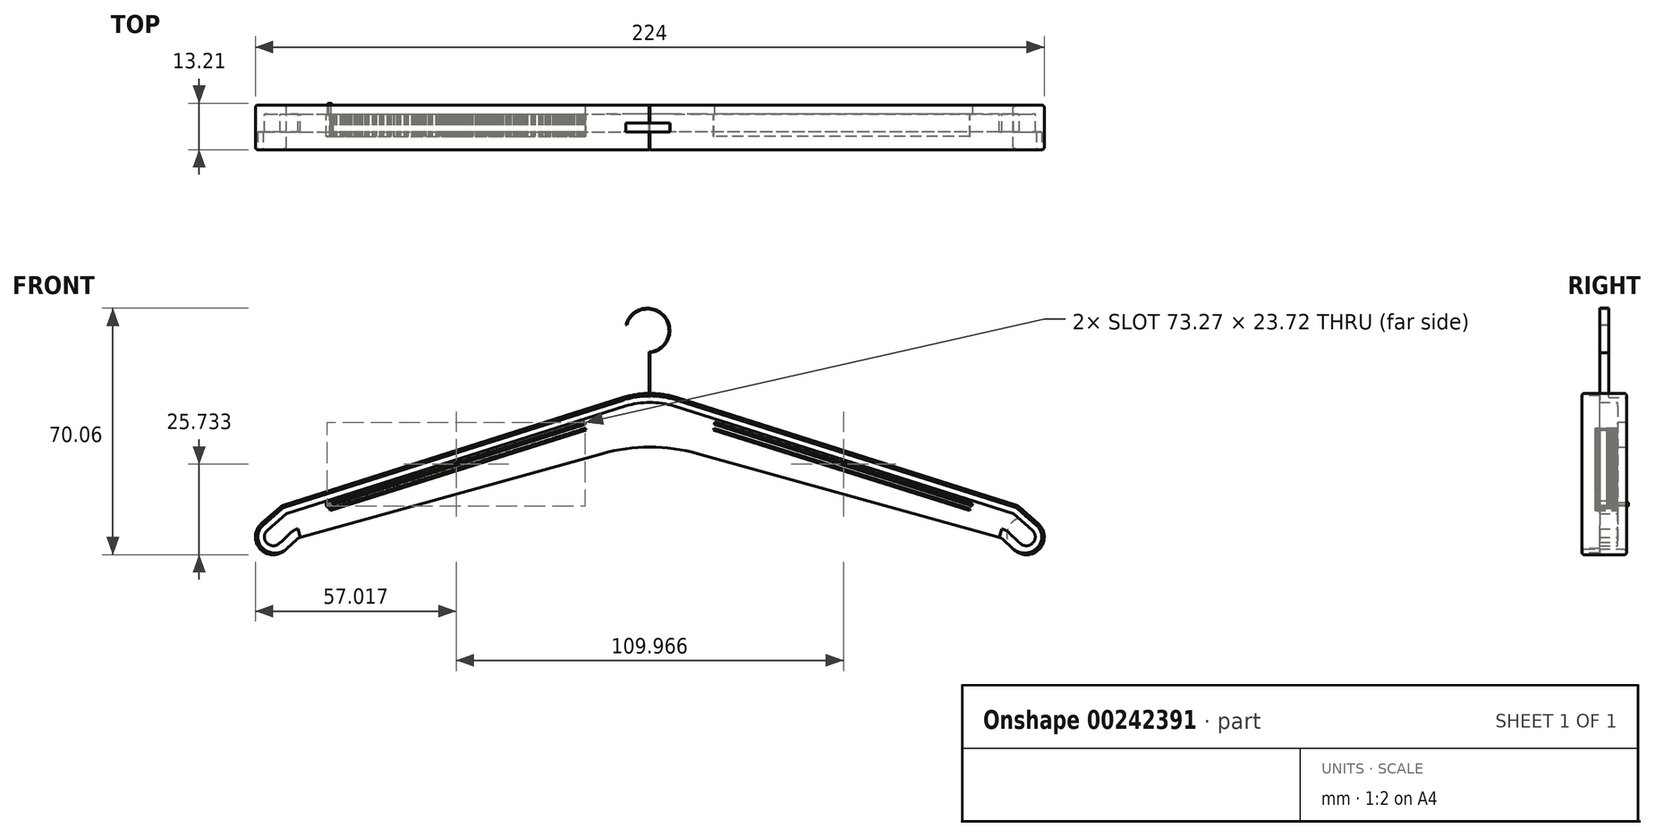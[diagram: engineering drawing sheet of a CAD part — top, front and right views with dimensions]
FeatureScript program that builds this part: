
annotation { "Feature Type Name" : "Feature", "Feature Type Description" : "" }
export const myFeature = defineFeature(function(context is Context, id is Id, definition is map)
    precondition{}
    {
        {
            var Q0;
            Q0=qCreatedBy(makeId("Front.planeOp"),FACE);
            var sketch = newSketch(context, id + "F0", { "sketchPlane" : qUnion([Q0])});
            skLineSegment(sketch, "E0", {"start": v(-104.02, 0.16) * mm, "end": v(-7.68, 30.71) * mm});
            skLineSegment(sketch, "E1", {"start": v(-99.25, -8.96) * mm, "end": v(-13.59, 14.81) * mm});
            skLineSegment(sketch, "E2.MirrorCS", {"start": v(104.52, 0) * mm, "end": v(7.68, 30.71) * mm});
            skLineSegment(sketch, "E3.MirrorCS", {"start": v(99.25, -8.96) * mm, "end": v(13.59, 14.81) * mm});
            skPoint(sketch, "E4.visualSharp", {"position": v(0, 18.58) * mm});
            skArc(sketch, "E5.filletArc", {"start": v(0.38, 28.89) * mm, "mid": v(0, 28.89) * mm, "end": v(-0.38, 28.89) * mm});
            skArc(sketch, "E6.filletArc", {"start": v(7.68, 30.71) * mm, "mid": v(0, 31.9) * mm, "end": v(-7.68, 30.71) * mm});
            skArc(sketch, "E7.filletArc", {"start": v(13.59, 14.81) * mm, "mid": v(0, 16.66) * mm, "end": v(-13.59, 14.81) * mm});
            skPoint(sketch, "E8.endSnap0", {"position": v(0, 31.9) * mm});
            skLineSegment(sketch, "E9", {"start": v(-104.92, -0.35) * mm, "end": v(-110.26, -5) * mm});
            skLineSegment(sketch, "E10", {"start": v(-102.91, -12.04) * mm, "end": v(-100.32, -9.57) * mm});
            skPoint(sketch, "E11.visualSharp", {"position": v(-111.4, -6) * mm});
            skArc(sketch, "E11.filletArc", {"start": v(-110.26, -5) * mm, "mid": v(-103.65, -12.72) * mm, "end": v(-110.13, -4.9) * mm});
            skPoint(sketch, "E12.visualSharp", {"position": v(-104.52, 0) * mm});
            skArc(sketch, "E12.filletArc", {"start": v(-104.02, 0.16) * mm, "mid": v(-104.5, -0.05) * mm, "end": v(-104.92, -0.35) * mm});
            skPoint(sketch, "E13.visualSharp", {"position": v(-107.27, -16.2) * mm});
            skArc(sketch, "E13.filletArc", {"start": v(-107.95, -13.2) * mm, "mid": v(-105.27, -13.31) * mm, "end": v(-102.91, -12.04) * mm});
            skPoint(sketch, "E14.visualSharp", {"position": v(-99.86, -9.13) * mm});
            skArc(sketch, "E14.filletArc", {"start": v(-99.25, -8.96) * mm, "mid": v(-99.82, -9.2) * mm, "end": v(-100.32, -9.57) * mm});
            skLineSegment(sketch, "E15", {"start": v(0, 16.66) * mm, "end": v(0, 31.9) * mm});
            skArc(sketch, "E16.MirrorCS", {"start": v(110.26, -5) * mm, "mid": v(103.65, -12.72) * mm, "end": v(110.13, -4.9) * mm});
            skLineSegment(sketch, "E17.MirrorCS", {"start": v(104.92, -0.35) * mm, "end": v(110.26, -5) * mm});
            skArc(sketch, "E18.MirrorCS", {"start": v(107.95, -13.2) * mm, "mid": v(105.27, -13.31) * mm, "end": v(102.91, -12.04) * mm});
            skLineSegment(sketch, "E19.MirrorCS", {"start": v(102.91, -12.04) * mm, "end": v(100.32, -9.57) * mm});
            skArc(sketch, "E20.MirrorCS", {"start": v(104.02, 0.16) * mm, "mid": v(104.5, -0.05) * mm, "end": v(104.92, -0.35) * mm});
            skArc(sketch, "E21.MirrorCS", {"start": v(99.25, -8.96) * mm, "mid": v(99.82, -9.2) * mm, "end": v(100.32, -9.57) * mm});
            skSolve(sketch);
        }
        {
            var Q0;
            {var subQ0=sQuery(id+"F0.wireOp",EDGE,"E0");Q0=makeQuery(id+"F0.imprint","IMPRINT",FACE,{"disambiguationData":[TD([[makeQuery(id+"F0.imprint","IMPRINT",EDGE,{"derivedFrom":subQ0}),-1.0]])]});}
            var Q1;
            {var subQ1=sQuery(id+"F0.wireOp",EDGE,"E3.MirrorCS");Q1=makeQuery(id+"F0.imprint","IMPRINT",FACE,{"disambiguationData":[TD([[makeQuery(id+"F0.imprint","IMPRINT",EDGE,{"derivedFrom":subQ1}),-1.0]])]});}
            var Q2;
            Q2=makeQuery(id+"F0.imprint","IMPRINT",FACE,{"disambiguationData":[TD([[makeQuery(id+"F0.imprint","IMPRINT",EDGE,{"derivedFrom":sQuery(id+"F0.wireOp",EDGE,"k7vzQUjf-RRhZ-hYac-MGxp-3dl7KEoSQEHl")}),1.0]])]});
            extrude(context, id + "F1", {"entities" : qUnion([Q0, Q1, Q2]), "depth" : 12.7 * mm});
        }
        {
            var Q0;
            Q0=makeQuery(id+"F1.opExtrude","CAP_EDGE",EDGE,{"disambiguationData":[OSD([sQuery(id+"F0.wireOp",EDGE,"E0")])],"isStart":true});
            var Q1;
            Q1=makeQuery(id+"F1.opExtrude","CAP_EDGE",EDGE,{"disambiguationData":[OSD([sQuery(id+"F0.wireOp",EDGE,"E0")])],"isStart":false});
            var Q2;
            Q2=makeQuery(id+"F1.opExtrude","CAP_EDGE",EDGE,{"disambiguationData":[OSD([sQuery(id+"F0.wireOp",EDGE,"E2.MirrorCS")])],"isStart":true});
            var Q3;
            Q3=makeQuery(id+"F1.opExtrude","CAP_EDGE",EDGE,{"disambiguationData":[OSD([sQuery(id+"F0.wireOp",EDGE,"E2.MirrorCS")])],"isStart":false});
            fillet(context, id + "F2", {"entities" : qUnion([Q0, Q1, Q2, Q3]), "radius" : 0.69 * mm, "tangentPropagation" : true, "allowEdgeOverflow" : false});
        }
        {
            var Q0;
            Q0=makeQuery(id+"F1.opExtrude","SWEPT_FACE",FACE,{"disambiguationData":[OSD([sQuery(id+"F0.wireOp",EDGE,"E7.filletArc")])]});
            var Q1;
            Q1=makeQuery(id+"F1.opExtrude","SWEPT_FACE",FACE,{"disambiguationData":[OSD([sQuery(id+"F0.wireOp",EDGE,"E1")])]});
            var Q2;
            Q2=makeQuery(id+"F1.opExtrude","SWEPT_FACE",FACE,{"disambiguationData":[OSD([sQuery(id+"F0.wireOp",EDGE,"E3.MirrorCS")])]});
            shell(context, id + "F3", {"entities" : qUnion([Q0, Q1, Q2]), "thickness" : 2.54 * mm});
        }
        {
            var Q0;
            Q0=qCreatedBy(makeId("Front.planeOp"),FACE);
            var sketch = newSketch(context, id + "F4", { "sketchPlane" : qUnion([Q0])});
            skLineSegment(sketch, "E22", {"start": v(0, 30.78) * mm, "end": v(0, 43.48) * mm});
            skArc(sketch, "E23", {"start": v(0, 43.48) * mm, "mid": v(4.18, 53.9) * mm, "end": v(-6.78, 51.45) * mm});
            skArc(sketch, "E24.0", {"start": v(-0.25, 43.71) * mm, "mid": v(4.06, 53.66) * mm, "end": v(-6.54, 51.39) * mm});
            skLineSegment(sketch, "E24.1", {"start": v(-0.25, 30.78) * mm, "end": v(-0.25, 43.71) * mm});
            skLineSegment(sketch, "E25", {"start": v(-6.78, 51.45) * mm, "end": v(-6.54, 51.39) * mm});
            skLineSegment(sketch, "E26", {"start": v(-0.25, 30.78) * mm, "end": v(0, 30.78) * mm});
            skSolve(sketch);
        }
        {
            var Q0;
            Q0 = qSketchRegion(id + "F4", true);
            extrude(context, id + "F5", {"entities" : qUnion([Q0]), "operationType" : NewBodyOperationType.ADD, "depth" : 12.7 * mm});
        }
        {
            var Q0;
            Q0 = qSketchRegion(id + "F4", true);
            extrude(context, id + "F6", {"entities" : qUnion([Q0]), "operationType" : NewBodyOperationType.REMOVE, "depth" : 5.08 * mm});
        }
        {
            var Q0;
            Q0=makeQuery(id+"F5.boolean.opBoolean","MERGE",FACE,{"derivedFrom":[makeQuery(id+"F1.opExtrude","CAP_FACE",FACE,{"disambiguationData":[OSD([sQuery(id+"F0.wireOp",EDGE,"E0"),sQuery(id+"F0.wireOp",EDGE,"E1"),sQuery(id+"F0.wireOp",EDGE,"E2.MirrorCS"),sQuery(id+"F0.wireOp",EDGE,"E3.MirrorCS"),sQuery(id+"F0.wireOp",EDGE,"E6.filletArc"),sQuery(id+"F0.wireOp",EDGE,"E7.filletArc"),sQuery(id+"F0.wireOp",EDGE,"E9"),sQuery(id+"F0.wireOp",EDGE,"E10"),sQuery(id+"F0.wireOp",EDGE,"E11.filletArc"),sQuery(id+"F0.wireOp",EDGE,"E12.filletArc"),sQuery(id+"F0.wireOp",EDGE,"E13.filletArc"),sQuery(id+"F0.wireOp",EDGE,"E14.filletArc"),sQuery(id+"F0.wireOp",EDGE,"E16.MirrorCS"),sQuery(id+"F0.wireOp",EDGE,"E17.MirrorCS"),sQuery(id+"F0.wireOp",EDGE,"E18.MirrorCS"),sQuery(id+"F0.wireOp",EDGE,"E19.MirrorCS"),sQuery(id+"F0.wireOp",EDGE,"E20.MirrorCS"),sQuery(id+"F0.wireOp",EDGE,"E21.MirrorCS")])],"isStart":false}),makeQuery(id+"F5.opExtrude","CAP_FACE",FACE,{"disambiguationData":[OSD([sQuery(id+"F4.wireOp",EDGE,"E22"),sQuery(id+"F4.wireOp",EDGE,"E23"),sQuery(id+"F4.wireOp",EDGE,"E24.0"),sQuery(id+"F4.wireOp",EDGE,"E24.1"),sQuery(id+"F4.wireOp",EDGE,"E25"),sQuery(id+"F4.wireOp",EDGE,"E26")])],"isStart":false})]});
            extrude(context, id + "F7", {"entities" : qUnion([Q0]), "operationType" : NewBodyOperationType.REMOVE, "oppositeDirection" : true, "depth" : 5.08 * mm});
        }
        {
            var Q0;
            {var subQ0=sQuery(id+"F0.wireOp",EDGE,"E21.MirrorCS");var subQ1=sQuery(id+"F0.wireOp",EDGE,"E20.MirrorCS");var subQ2=sQuery(id+"F0.wireOp",EDGE,"E19.MirrorCS");var subQ3=sQuery(id+"F0.wireOp",EDGE,"E18.MirrorCS");var subQ4=sQuery(id+"F0.wireOp",EDGE,"E17.MirrorCS");var subQ5=sQuery(id+"F0.wireOp",EDGE,"E16.MirrorCS");var subQ6=sQuery(id+"F0.wireOp",EDGE,"E14.filletArc");var subQ7=sQuery(id+"F0.wireOp",EDGE,"E13.filletArc");var subQ8=sQuery(id+"F0.wireOp",EDGE,"E12.filletArc");var subQ9=sQuery(id+"F0.wireOp",EDGE,"E11.filletArc");var subQ10=sQuery(id+"F0.wireOp",EDGE,"E10");var subQ11=sQuery(id+"F0.wireOp",EDGE,"E9");var subQ12=sQuery(id+"F0.wireOp",EDGE,"E7.filletArc");var subQ13=sQuery(id+"F0.wireOp",EDGE,"E6.filletArc");var subQ14=sQuery(id+"F0.wireOp",EDGE,"E3.MirrorCS");var subQ15=sQuery(id+"F0.wireOp",EDGE,"E2.MirrorCS");var subQ16=sQuery(id+"F0.wireOp",EDGE,"E1");var subQ17=sQuery(id+"F0.wireOp",EDGE,"E0");Q0=makeQuery(id+"F3.opShell","OFFSET_FACE",FACE,{"disambiguationData":[OSD([subQ17,subQ16,subQ15,subQ14,subQ13,subQ12,subQ11,subQ10,subQ9,subQ8,subQ7,subQ6,subQ5,subQ4,subQ3,subQ2,subQ1,subQ0]),TDD([makeQuery(id+"F1.opExtrude","CAP_FACE",FACE,{"disambiguationData":[OSD([subQ17,subQ16,subQ15,subQ14,subQ13,subQ12,subQ11,subQ10,subQ9,subQ8,subQ7,subQ6,subQ5,subQ4,subQ3,subQ2,subQ1,subQ0])],"isStart":true})])]});}
            var sketch = newSketch(context, id + "F8", { "sketchPlane" : qUnion([Q0])});
            skLineSegment(sketch, "E27", {"start": v(-90.8, -1.3) * mm, "end": v(-18.08, 21.46) * mm});
            skLineSegment(sketch, "E28.MirrorCS", {"start": v(90.8, -1.3) * mm, "end": v(18.08, 21.46) * mm});
            skLineSegment(sketch, "E29.0", {"start": v(90.95, -0.82) * mm, "end": v(18.23, 21.95) * mm});
            skLineSegment(sketch, "E30.0", {"start": v(-90.95, -0.82) * mm, "end": v(-18.23, 21.95) * mm});
            skLineSegment(sketch, "E31", {"start": v(-90.8, -1.3) * mm, "end": v(-90.95, -0.82) * mm});
            skLineSegment(sketch, "E32", {"start": v(-18.08, 21.46) * mm, "end": v(-18.23, 21.95) * mm});
            skLineSegment(sketch, "E33", {"start": v(18.08, 21.46) * mm, "end": v(18.23, 21.95) * mm});
            skLineSegment(sketch, "E34", {"start": v(90.8, -1.3) * mm, "end": v(90.95, -0.82) * mm});
            skSolve(sketch);
        }
        {
            var Q0;
            Q0 = qSketchRegion(id + "F8", true);
            var Q1;
            Q1=sQuery(id+"F8.wireOp",EDGE,"E27");
            var Q2;
            Q2=sQuery(id+"F8.wireOp",EDGE,"E28.MirrorCS");
            extrude(context, id + "F9", {"entities" : qUnion([Q0]), "surfaceEntities" : qUnion([Q1, Q2]), "depth" : 6.35 * mm});
        }
        {
            var Q0;
            Q0=makeQuery(id+"F9.opExtrude","CAP_FACE",FACE,{"disambiguationData":[OSD([sQuery(id+"F8.wireOp",EDGE,"E27"),sQuery(id+"F8.wireOp",EDGE,"E30.0"),sQuery(id+"F8.wireOp",EDGE,"E31"),sQuery(id+"F8.wireOp",EDGE,"E32")])],"isStart":false});
            var sketch = newSketch(context, id + "F10", { "sketchPlane" : qUnion([Q0])});
            skLineSegment(sketch, "E35", {"start": v(-90.95, -0.82) * mm, "end": v(-90.92, -0.67) * mm});
            skLineSegment(sketch, "E36", {"start": v(-90.92, -0.67) * mm, "end": v(-90.77, -0.63) * mm});
            skLineSegment(sketch, "E37", {"start": v(-90.77, -0.63) * mm, "end": v(-90.66, -0.73) * mm});
            skLineSegment(sketch, "E38", {"start": v(-90.66, -0.73) * mm, "end": v(-90.52, -0.69) * mm});
            skLineSegment(sketch, "E39.MirrorCS", {"start": v(-90.49, -0.54) * mm, "end": v(-90.52, -0.69) * mm});
            skLineSegment(sketch, "E40.MirrorCS", {"start": v(-90.34, -0.5) * mm, "end": v(-90.49, -0.54) * mm});
            skLineSegment(sketch, "E41.MirrorCS", {"start": v(-90.23, -0.6) * mm, "end": v(-90.34, -0.5) * mm});
            skLineSegment(sketch, "E42.MirrorCS", {"start": v(-90.34, -0.5) * mm, "end": v(-90.23, -0.6) * mm});
            skLineSegment(sketch, "E43.MirrorCS", {"start": v(-90.09, -0.55) * mm, "end": v(-90.23, -0.6) * mm});
            skLineSegment(sketch, "E44.MirrorCS", {"start": v(-90.06, -0.4) * mm, "end": v(-90.09, -0.55) * mm});
            skLineSegment(sketch, "E45.MirrorCS", {"start": v(-89.91, -0.36) * mm, "end": v(-90.06, -0.4) * mm});
            skLineSegment(sketch, "E46.MirrorCS", {"start": v(-89.8, -0.46) * mm, "end": v(-89.91, -0.36) * mm});
            skLineSegment(sketch, "E47.MirrorCS", {"start": v(-89.63, -0.27) * mm, "end": v(-89.65, -0.42) * mm});
            skLineSegment(sketch, "E48.MirrorCS", {"start": v(-89.65, -0.42) * mm, "end": v(-89.8, -0.46) * mm});
            skLineSegment(sketch, "E49.MirrorCS", {"start": v(-89.48, -0.22) * mm, "end": v(-89.63, -0.27) * mm});
            skLineSegment(sketch, "E50.MirrorCS", {"start": v(-89.37, -0.33) * mm, "end": v(-89.48, -0.22) * mm});
            skLineSegment(sketch, "E51.MirrorCS", {"start": v(-88.8, -0.15) * mm, "end": v(-88.76, 0) * mm});
            skLineSegment(sketch, "E52.MirrorCS", {"start": v(-88.76, 0) * mm, "end": v(-88.8, -0.15) * mm});
            skLineSegment(sketch, "E53.MirrorCS", {"start": v(-88.94, -0.2) * mm, "end": v(-88.8, -0.15) * mm});
            skLineSegment(sketch, "E54.MirrorCS", {"start": v(-88.76, 0) * mm, "end": v(-88.62, 0.05) * mm});
            skLineSegment(sketch, "E55.MirrorCS", {"start": v(-89.05, -0.09) * mm, "end": v(-88.94, -0.2) * mm});
            skLineSegment(sketch, "E56.MirrorCS", {"start": v(-88.36, -0.01) * mm, "end": v(-88.5, -0.06) * mm});
            skLineSegment(sketch, "E57.MirrorCS", {"start": v(-88.62, 0.05) * mm, "end": v(-88.5, -0.06) * mm});
            skLineSegment(sketch, "E58.MirrorCS", {"start": v(-88.33, 0.14) * mm, "end": v(-88.36, -0.01) * mm});
            skLineSegment(sketch, "E59.MirrorCS", {"start": v(-88.19, 0.18) * mm, "end": v(-88.33, 0.14) * mm});
            skLineSegment(sketch, "E60.MirrorCS", {"start": v(-88.08, 0.08) * mm, "end": v(-88.19, 0.18) * mm});
            skLineSegment(sketch, "E61.MirrorCS", {"start": v(-89.2, -0.13) * mm, "end": v(-89.05, -0.09) * mm});
            skLineSegment(sketch, "E62.MirrorCS", {"start": v(-89.22, -0.28) * mm, "end": v(-89.2, -0.13) * mm});
            skLineSegment(sketch, "E63.MirrorCS", {"start": v(-89.37, -0.33) * mm, "end": v(-89.22, -0.28) * mm});
            skLineSegment(sketch, "E64.MirrorCS", {"start": v(-88.19, 0.18) * mm, "end": v(-88.08, 0.08) * mm});
            skLineSegment(sketch, "E65.MirrorCS", {"start": v(-86.64, 0.53) * mm, "end": v(-86.61, 0.68) * mm});
            skLineSegment(sketch, "E66.MirrorCS", {"start": v(-86.61, 0.68) * mm, "end": v(-86.64, 0.53) * mm});
            skLineSegment(sketch, "E67.MirrorCS", {"start": v(-87.5, 0.26) * mm, "end": v(-87.65, 0.21) * mm});
            skLineSegment(sketch, "E68.MirrorCS", {"start": v(-87.47, 0.4) * mm, "end": v(-87.33, 0.45) * mm});
            skLineSegment(sketch, "E69.MirrorCS", {"start": v(-86.9, 0.59) * mm, "end": v(-86.79, 0.48) * mm});
            skLineSegment(sketch, "E70.MirrorCS", {"start": v(-87.04, 0.54) * mm, "end": v(-86.9, 0.59) * mm});
            skLineSegment(sketch, "E71.MirrorCS", {"start": v(-87.07, 0.4) * mm, "end": v(-87.04, 0.54) * mm});
            skLineSegment(sketch, "E72.MirrorCS", {"start": v(-85.93, 0.75) * mm, "end": v(-86.04, 0.86) * mm});
            skLineSegment(sketch, "E73.MirrorCS", {"start": v(-86.04, 0.86) * mm, "end": v(-86.18, 0.81) * mm});
            skLineSegment(sketch, "E74.MirrorCS", {"start": v(-86.18, 0.81) * mm, "end": v(-86.21, 0.66) * mm});
            skLineSegment(sketch, "E75.MirrorCS", {"start": v(-87.33, 0.45) * mm, "end": v(-87.22, 0.35) * mm});
            skLineSegment(sketch, "E76.MirrorCS", {"start": v(-86.21, 0.66) * mm, "end": v(-86.36, 0.62) * mm});
            skLineSegment(sketch, "E77.MirrorCS", {"start": v(-87.76, 0.32) * mm, "end": v(-87.9, 0.27) * mm});
            skLineSegment(sketch, "E78.MirrorCS", {"start": v(-87.22, 0.35) * mm, "end": v(-87.07, 0.4) * mm});
            skLineSegment(sketch, "E79.MirrorCS", {"start": v(-87.9, 0.27) * mm, "end": v(-87.93, 0.12) * mm});
            skLineSegment(sketch, "E80.MirrorCS", {"start": v(-86.47, 0.72) * mm, "end": v(-86.36, 0.62) * mm});
            skLineSegment(sketch, "E81.MirrorCS", {"start": v(-86.61, 0.68) * mm, "end": v(-86.47, 0.72) * mm});
            skLineSegment(sketch, "E82.MirrorCS", {"start": v(-87.93, 0.12) * mm, "end": v(-88.08, 0.08) * mm});
            skLineSegment(sketch, "E83.MirrorCS", {"start": v(-87.65, 0.21) * mm, "end": v(-87.76, 0.32) * mm});
            skLineSegment(sketch, "E84.MirrorCS", {"start": v(-87.5, 0.26) * mm, "end": v(-87.47, 0.4) * mm});
            skLineSegment(sketch, "E85.MirrorCS", {"start": v(-86.79, 0.48) * mm, "end": v(-86.64, 0.53) * mm});
            skLineSegment(sketch, "E86.MirrorCS", {"start": v(-84.46, 1.35) * mm, "end": v(-84.49, 1.2) * mm});
            skLineSegment(sketch, "E87.MirrorCS", {"start": v(-83.88, 1.53) * mm, "end": v(-83.77, 1.42) * mm});
            skLineSegment(sketch, "E88.MirrorCS", {"start": v(-82.34, 1.87) * mm, "end": v(-82.3, 2.02) * mm});
            skLineSegment(sketch, "E89.MirrorCS", {"start": v(-85.6, 1) * mm, "end": v(-85.75, 0.94) * mm});
            skLineSegment(sketch, "E90.MirrorCS", {"start": v(-84.49, 1.2) * mm, "end": v(-84.46, 1.35) * mm});
            skLineSegment(sketch, "E91.MirrorCS", {"start": v(-86.04, 0.86) * mm, "end": v(-85.93, 0.75) * mm});
            skLineSegment(sketch, "E92.MirrorCS", {"start": v(-82.74, 1.89) * mm, "end": v(-82.6, 1.93) * mm});
            skLineSegment(sketch, "E93.MirrorCS", {"start": v(-84.46, 1.35) * mm, "end": v(-84.31, 1.4) * mm});
            skLineSegment(sketch, "E94.MirrorCS", {"start": v(-81.9, 2) * mm, "end": v(-82.05, 1.96) * mm});
            skLineSegment(sketch, "E95.MirrorCS", {"start": v(-82.3, 2.02) * mm, "end": v(-82.34, 1.87) * mm});
            skLineSegment(sketch, "E96.MirrorCS", {"start": v(-82.91, 1.7) * mm, "end": v(-82.77, 1.74) * mm});
            skLineSegment(sketch, "E97.MirrorCS", {"start": v(-84.2, 1.29) * mm, "end": v(-84.06, 1.33) * mm});
            skLineSegment(sketch, "E98.MirrorCS", {"start": v(-83.77, 1.42) * mm, "end": v(-83.88, 1.53) * mm});
            skLineSegment(sketch, "E99.MirrorCS", {"start": v(-83.88, 1.53) * mm, "end": v(-84.03, 1.48) * mm});
            skLineSegment(sketch, "E100.MirrorCS", {"start": v(-85.18, 1.13) * mm, "end": v(-85.32, 1.08) * mm});
            skLineSegment(sketch, "E101.MirrorCS", {"start": v(-84.64, 1.15) * mm, "end": v(-84.49, 1.2) * mm});
            skLineSegment(sketch, "E102.MirrorCS", {"start": v(-83.17, 1.75) * mm, "end": v(-83.02, 1.8) * mm});
            skLineSegment(sketch, "E103.MirrorCS", {"start": v(-85.35, 0.93) * mm, "end": v(-85.5, 0.88) * mm});
            skLineSegment(sketch, "E104.MirrorCS", {"start": v(-85.78, 0.8) * mm, "end": v(-85.93, 0.75) * mm});
            skLineSegment(sketch, "E105.MirrorCS", {"start": v(-84.31, 1.4) * mm, "end": v(-84.2, 1.29) * mm});
            skLineSegment(sketch, "E106.MirrorCS", {"start": v(-82.48, 1.83) * mm, "end": v(-82.34, 1.87) * mm});
            skLineSegment(sketch, "E107.MirrorCS", {"start": v(-83.63, 1.47) * mm, "end": v(-83.77, 1.42) * mm});
            skLineSegment(sketch, "E108.MirrorCS", {"start": v(-82.3, 2.02) * mm, "end": v(-82.16, 2.07) * mm});
            skLineSegment(sketch, "E109.MirrorCS", {"start": v(-83.34, 1.56) * mm, "end": v(-83.45, 1.66) * mm});
            skLineSegment(sketch, "E110.MirrorCS", {"start": v(-83.02, 1.8) * mm, "end": v(-82.91, 1.7) * mm});
            skLineSegment(sketch, "E111.MirrorCS", {"start": v(-85.07, 1.02) * mm, "end": v(-84.92, 1.06) * mm});
            skLineSegment(sketch, "E112.MirrorCS", {"start": v(-83.45, 1.66) * mm, "end": v(-83.6, 1.62) * mm});
            skLineSegment(sketch, "E113.MirrorCS", {"start": v(-85.75, 0.94) * mm, "end": v(-85.78, 0.8) * mm});
            skLineSegment(sketch, "E114.MirrorCS", {"start": v(-84.9, 1.21) * mm, "end": v(-84.75, 1.26) * mm});
            skLineSegment(sketch, "E115.MirrorCS", {"start": v(-83.6, 1.62) * mm, "end": v(-83.63, 1.47) * mm});
            skLineSegment(sketch, "E116.MirrorCS", {"start": v(-84.75, 1.26) * mm, "end": v(-84.64, 1.15) * mm});
            skLineSegment(sketch, "E117.MirrorCS", {"start": v(-85.5, 0.88) * mm, "end": v(-85.6, 1) * mm});
            skLineSegment(sketch, "E118.MirrorCS", {"start": v(-83.2, 1.6) * mm, "end": v(-83.34, 1.56) * mm});
            skLineSegment(sketch, "E119.MirrorCS", {"start": v(-85.32, 1.08) * mm, "end": v(-85.35, 0.93) * mm});
            skLineSegment(sketch, "E120.MirrorCS", {"start": v(-83.2, 1.6) * mm, "end": v(-83.17, 1.75) * mm});
            skLineSegment(sketch, "E121.MirrorCS", {"start": v(-84.92, 1.06) * mm, "end": v(-84.9, 1.21) * mm});
            skLineSegment(sketch, "E122.MirrorCS", {"start": v(-82.77, 1.74) * mm, "end": v(-82.74, 1.89) * mm});
            skLineSegment(sketch, "E123.MirrorCS", {"start": v(-82.6, 1.93) * mm, "end": v(-82.48, 1.83) * mm});
            skLineSegment(sketch, "E124.MirrorCS", {"start": v(-84.03, 1.48) * mm, "end": v(-84.06, 1.33) * mm});
            skLineSegment(sketch, "E125.MirrorCS", {"start": v(-82.16, 2.07) * mm, "end": v(-82.05, 1.96) * mm});
            skLineSegment(sketch, "E126.MirrorCS", {"start": v(-85.07, 1.02) * mm, "end": v(-85.18, 1.13) * mm});
            skLineSegment(sketch, "E127.MirrorCS", {"start": v(-81.88, 2.16) * mm, "end": v(-81.9, 2) * mm});
            skLineSegment(sketch, "E128.MirrorCS", {"start": v(-81.73, 2.2) * mm, "end": v(-81.88, 2.16) * mm});
            skLineSegment(sketch, "E129", {"start": v(-90.84, -0.65) * mm, "end": v(-90.77, -0.89) * mm, "construction": true});
            skLineSegment(sketch, "E130", {"start": v(-81.8, 2.18) * mm, "end": v(-81.71, 1.88) * mm, "construction": true});
            skLineSegment(sketch, "E131.MirrorCS", {"start": v(-77.57, 3.5) * mm, "end": v(-77.6, 3.36) * mm});
            skLineSegment(sketch, "E132.MirrorCS", {"start": v(-75.45, 4.03) * mm, "end": v(-75.42, 4.18) * mm});
            skLineSegment(sketch, "E133.MirrorCS", {"start": v(-79.04, 2.9) * mm, "end": v(-79.15, 3.01) * mm});
            skLineSegment(sketch, "E134.MirrorCS", {"start": v(-77.6, 3.36) * mm, "end": v(-77.57, 3.5) * mm});
            skLineSegment(sketch, "E135.MirrorCS", {"start": v(-79.15, 3.01) * mm, "end": v(-79.04, 2.9) * mm});
            skLineSegment(sketch, "E136.MirrorCS", {"start": v(-77, 3.69) * mm, "end": v(-76.89, 3.58) * mm});
            skLineSegment(sketch, "E137.MirrorCS", {"start": v(-73.3, 4.7) * mm, "end": v(-73.27, 4.85) * mm});
            skLineSegment(sketch, "E138.MirrorCS", {"start": v(-79.73, 2.83) * mm, "end": v(-79.76, 2.68) * mm});
            skLineSegment(sketch, "E139.MirrorCS", {"start": v(-74.85, 4.36) * mm, "end": v(-74.74, 4.25) * mm});
            skLineSegment(sketch, "E140.MirrorCS", {"start": v(-75.42, 4.18) * mm, "end": v(-75.45, 4.03) * mm});
            skLineSegment(sketch, "E141.MirrorCS", {"start": v(-81.3, 2.34) * mm, "end": v(-81.2, 2.23) * mm});
            skLineSegment(sketch, "E142.MirrorCS", {"start": v(-73.27, 4.85) * mm, "end": v(-73.3, 4.7) * mm});
            skLineSegment(sketch, "E143.MirrorCS", {"start": v(-79.76, 2.68) * mm, "end": v(-79.73, 2.83) * mm});
            skLineSegment(sketch, "E144.MirrorCS", {"start": v(-74.74, 4.25) * mm, "end": v(-74.85, 4.36) * mm});
            skLineSegment(sketch, "E145.MirrorCS", {"start": v(-76.89, 3.58) * mm, "end": v(-77, 3.69) * mm});
            skLineSegment(sketch, "E146.MirrorCS", {"start": v(-79.15, 3.01) * mm, "end": v(-79.3, 2.97) * mm});
            skLineSegment(sketch, "E147.MirrorCS", {"start": v(-81.2, 2.23) * mm, "end": v(-81.3, 2.34) * mm});
            skLineSegment(sketch, "E148.MirrorCS", {"start": v(-77.57, 3.5) * mm, "end": v(-77.43, 3.55) * mm});
            skLineSegment(sketch, "E149.MirrorCS", {"start": v(-75.42, 4.18) * mm, "end": v(-75.28, 4.22) * mm});
            skLineSegment(sketch, "E150.MirrorCS", {"start": v(-77.43, 3.55) * mm, "end": v(-77.32, 3.45) * mm});
            skLineSegment(sketch, "E151.MirrorCS", {"start": v(-75.28, 4.22) * mm, "end": v(-75.17, 4.12) * mm});
            skLineSegment(sketch, "E152.MirrorCS", {"start": v(-79.3, 2.97) * mm, "end": v(-79.32, 2.82) * mm});
            skLineSegment(sketch, "E153.MirrorCS", {"start": v(-81.62, 2.1) * mm, "end": v(-81.48, 2.14) * mm});
            skLineSegment(sketch, "E154.MirrorCS", {"start": v(-74.85, 4.36) * mm, "end": v(-75, 4.31) * mm});
            skLineSegment(sketch, "E155.MirrorCS", {"start": v(-78, 3.37) * mm, "end": v(-77.86, 3.42) * mm});
            skLineSegment(sketch, "E156.MirrorCS", {"start": v(-77.86, 3.42) * mm, "end": v(-77.75, 3.31) * mm});
            skLineSegment(sketch, "E157.MirrorCS", {"start": v(-81.45, 2.3) * mm, "end": v(-81.48, 2.14) * mm});
            skLineSegment(sketch, "E158.MirrorCS", {"start": v(-78.86, 3.1) * mm, "end": v(-78.9, 2.95) * mm});
            skLineSegment(sketch, "E159.MirrorCS", {"start": v(-75.6, 3.98) * mm, "end": v(-75.45, 4.03) * mm});
            skLineSegment(sketch, "E160.MirrorCS", {"start": v(-75.17, 4.12) * mm, "end": v(-75.02, 4.16) * mm});
            skLineSegment(sketch, "E161.MirrorCS", {"start": v(-79.58, 2.88) * mm, "end": v(-79.47, 2.77) * mm});
            skLineSegment(sketch, "E162.MirrorCS", {"start": v(-80.16, 2.7) * mm, "end": v(-80.01, 2.74) * mm});
            skLineSegment(sketch, "E163.MirrorCS", {"start": v(-77, 3.69) * mm, "end": v(-77.14, 3.64) * mm});
            skLineSegment(sketch, "E164.MirrorCS", {"start": v(-74.56, 4.45) * mm, "end": v(-74.6, 4.3) * mm});
            skLineSegment(sketch, "E165.MirrorCS", {"start": v(-78.46, 3.09) * mm, "end": v(-78.6, 3.04) * mm});
            skLineSegment(sketch, "E166.MirrorCS", {"start": v(-81.02, 2.43) * mm, "end": v(-81.05, 2.28) * mm});
            skLineSegment(sketch, "E167.MirrorCS", {"start": v(-74.16, 4.43) * mm, "end": v(-74.13, 4.58) * mm});
            skLineSegment(sketch, "E168.MirrorCS", {"start": v(-76.03, 3.85) * mm, "end": v(-75.88, 3.9) * mm});
            skLineSegment(sketch, "E169.MirrorCS", {"start": v(-77.75, 3.31) * mm, "end": v(-77.6, 3.36) * mm});
            skLineSegment(sketch, "E170.MirrorCS", {"start": v(-79.73, 2.83) * mm, "end": v(-79.58, 2.88) * mm});
            skLineSegment(sketch, "E171.MirrorCS", {"start": v(-80.59, 2.56) * mm, "end": v(-80.62, 2.41) * mm});
            skLineSegment(sketch, "E172.MirrorCS", {"start": v(-80.76, 2.37) * mm, "end": v(-80.87, 2.47) * mm});
            skLineSegment(sketch, "E173.MirrorCS", {"start": v(-74.13, 4.58) * mm, "end": v(-73.98, 4.63) * mm});
            skLineSegment(sketch, "E174.MirrorCS", {"start": v(-74.16, 4.43) * mm, "end": v(-74.3, 4.39) * mm});
            skLineSegment(sketch, "E175.MirrorCS", {"start": v(-80.19, 2.55) * mm, "end": v(-80.16, 2.7) * mm});
            skLineSegment(sketch, "E176.MirrorCS", {"start": v(-78.6, 3.04) * mm, "end": v(-78.72, 3.15) * mm});
            skLineSegment(sketch, "E177.MirrorCS", {"start": v(-74.42, 4.5) * mm, "end": v(-74.56, 4.45) * mm});
            skLineSegment(sketch, "E178.MirrorCS", {"start": v(-76.46, 3.71) * mm, "end": v(-76.57, 3.82) * mm});
            skLineSegment(sketch, "E179.MirrorCS", {"start": v(-73.12, 4.9) * mm, "end": v(-73.01, 4.8) * mm});
            skLineSegment(sketch, "E180.MirrorCS", {"start": v(-75, 4.31) * mm, "end": v(-75.02, 4.16) * mm});
            skLineSegment(sketch, "E181.MirrorCS", {"start": v(-78.43, 3.24) * mm, "end": v(-78.29, 3.28) * mm});
            skLineSegment(sketch, "E182.MirrorCS", {"start": v(-77.32, 3.45) * mm, "end": v(-77.17, 3.5) * mm});
            skLineSegment(sketch, "E183.MirrorCS", {"start": v(-81.05, 2.28) * mm, "end": v(-81.2, 2.23) * mm});
            skLineSegment(sketch, "E184.MirrorCS", {"start": v(-73.27, 4.85) * mm, "end": v(-73.12, 4.9) * mm});
            skLineSegment(sketch, "E185.MirrorCS", {"start": v(-75.88, 3.9) * mm, "end": v(-75.85, 4.04) * mm});
            skLineSegment(sketch, "E186.MirrorCS", {"start": v(-76.14, 3.96) * mm, "end": v(-76.28, 3.9) * mm});
            skLineSegment(sketch, "E187.MirrorCS", {"start": v(-78.03, 3.22) * mm, "end": v(-78, 3.37) * mm});
            skLineSegment(sketch, "E188.MirrorCS", {"start": v(-78.46, 3.09) * mm, "end": v(-78.43, 3.24) * mm});
            skLineSegment(sketch, "E189.MirrorCS", {"start": v(-80.33, 2.5) * mm, "end": v(-80.44, 2.6) * mm});
            skLineSegment(sketch, "E190.MirrorCS", {"start": v(-81.3, 2.34) * mm, "end": v(-81.45, 2.3) * mm});
            skLineSegment(sketch, "E191.MirrorCS", {"start": v(-79.32, 2.82) * mm, "end": v(-79.47, 2.77) * mm});
            skLineSegment(sketch, "E192.MirrorCS", {"start": v(-78.9, 2.95) * mm, "end": v(-79.04, 2.9) * mm});
            skLineSegment(sketch, "E193.MirrorCS", {"start": v(-76.71, 3.77) * mm, "end": v(-76.74, 3.63) * mm});
            skLineSegment(sketch, "E194.MirrorCS", {"start": v(-76.74, 3.63) * mm, "end": v(-76.89, 3.58) * mm});
            skLineSegment(sketch, "E195.MirrorCS", {"start": v(-78.29, 3.28) * mm, "end": v(-78.18, 3.18) * mm});
            skLineSegment(sketch, "E196.MirrorCS", {"start": v(-79.9, 2.64) * mm, "end": v(-79.76, 2.68) * mm});
            skLineSegment(sketch, "E197.MirrorCS", {"start": v(-80.62, 2.41) * mm, "end": v(-80.76, 2.37) * mm});
            skLineSegment(sketch, "E198.MirrorCS", {"start": v(-76.03, 3.85) * mm, "end": v(-76.14, 3.96) * mm});
            skLineSegment(sketch, "E199.MirrorCS", {"start": v(-73.44, 4.66) * mm, "end": v(-73.3, 4.7) * mm});
            skLineSegment(sketch, "E200.MirrorCS", {"start": v(-73.55, 4.76) * mm, "end": v(-73.44, 4.66) * mm});
            skLineSegment(sketch, "E201.MirrorCS", {"start": v(-73.7, 4.72) * mm, "end": v(-73.55, 4.76) * mm});
            skLineSegment(sketch, "E202.MirrorCS", {"start": v(-76.31, 3.76) * mm, "end": v(-76.46, 3.71) * mm});
            skLineSegment(sketch, "E203.MirrorCS", {"start": v(-76.57, 3.82) * mm, "end": v(-76.71, 3.77) * mm});
            skLineSegment(sketch, "E204.MirrorCS", {"start": v(-75.85, 4.04) * mm, "end": v(-75.7, 4.09) * mm});
            skLineSegment(sketch, "E205.MirrorCS", {"start": v(-74.6, 4.3) * mm, "end": v(-74.74, 4.25) * mm});
            skLineSegment(sketch, "E206.MirrorCS", {"start": v(-76.28, 3.9) * mm, "end": v(-76.31, 3.76) * mm});
            skLineSegment(sketch, "E207.MirrorCS", {"start": v(-78.72, 3.15) * mm, "end": v(-78.86, 3.1) * mm});
            skLineSegment(sketch, "E208.MirrorCS", {"start": v(-72.7, 5.03) * mm, "end": v(-72.84, 4.99) * mm});
            skLineSegment(sketch, "E209.MirrorCS", {"start": v(-72.84, 4.99) * mm, "end": v(-72.87, 4.84) * mm});
            skLineSegment(sketch, "E210.MirrorCS", {"start": v(-80.44, 2.6) * mm, "end": v(-80.59, 2.56) * mm});
            skLineSegment(sketch, "E211.MirrorCS", {"start": v(-73.73, 4.57) * mm, "end": v(-73.7, 4.72) * mm});
            skLineSegment(sketch, "E212.MirrorCS", {"start": v(-73.98, 4.63) * mm, "end": v(-73.87, 4.52) * mm});
            skLineSegment(sketch, "E213.MirrorCS", {"start": v(-72.87, 4.84) * mm, "end": v(-73.01, 4.8) * mm});
            skLineSegment(sketch, "E214.MirrorCS", {"start": v(-75.7, 4.09) * mm, "end": v(-75.6, 3.98) * mm});
            skLineSegment(sketch, "E215.MirrorCS", {"start": v(-77.14, 3.64) * mm, "end": v(-77.17, 3.5) * mm});
            skLineSegment(sketch, "E216.MirrorCS", {"start": v(-73.87, 4.52) * mm, "end": v(-73.73, 4.57) * mm});
            skLineSegment(sketch, "E217.MirrorCS", {"start": v(-80.33, 2.5) * mm, "end": v(-80.19, 2.55) * mm});
            skLineSegment(sketch, "E218.MirrorCS", {"start": v(-74.3, 4.39) * mm, "end": v(-74.42, 4.5) * mm});
            skLineSegment(sketch, "E219.MirrorCS", {"start": v(-80.01, 2.74) * mm, "end": v(-79.9, 2.64) * mm});
            skLineSegment(sketch, "E220.MirrorCS", {"start": v(-78.18, 3.18) * mm, "end": v(-78.03, 3.22) * mm});
            skLineSegment(sketch, "E221.MirrorCS", {"start": v(-80.87, 2.47) * mm, "end": v(-81.02, 2.43) * mm});
            skLineSegment(sketch, "E222.MirrorCS", {"start": v(-72.58, 4.93) * mm, "end": v(-72.7, 5.03) * mm});
            skLineSegment(sketch, "E223.MirrorCS", {"start": v(-72.77, 5.01) * mm, "end": v(-72.7, 4.77) * mm, "construction": true});
            skLineSegment(sketch, "E224.MirrorCS", {"start": v(-66.41, 6.86) * mm, "end": v(-66.38, 7) * mm});
            skLineSegment(sketch, "E225.MirrorCS", {"start": v(-59.53, 9.02) * mm, "end": v(-59.5, 9.17) * mm});
            skLineSegment(sketch, "E226.MirrorCS", {"start": v(-70, 5.74) * mm, "end": v(-70.11, 5.84) * mm});
            skLineSegment(sketch, "E227.MirrorCS", {"start": v(-67.96, 6.52) * mm, "end": v(-67.85, 6.41) * mm});
            skLineSegment(sketch, "E228.MirrorCS", {"start": v(-57.37, 9.69) * mm, "end": v(-57.34, 9.84) * mm});
            skLineSegment(sketch, "E229.MirrorCS", {"start": v(-61.07, 8.67) * mm, "end": v(-60.96, 8.57) * mm});
            skLineSegment(sketch, "E230.MirrorCS", {"start": v(-67.85, 6.41) * mm, "end": v(-67.96, 6.52) * mm});
            skLineSegment(sketch, "E231.MirrorCS", {"start": v(-70.11, 5.84) * mm, "end": v(-70, 5.74) * mm});
            skLineSegment(sketch, "E232.MirrorCS", {"start": v(-57.34, 9.84) * mm, "end": v(-57.37, 9.69) * mm});
            skLineSegment(sketch, "E233.MirrorCS", {"start": v(-59.5, 9.17) * mm, "end": v(-59.53, 9.02) * mm});
            skLineSegment(sketch, "E234.MirrorCS", {"start": v(-55.22, 10.36) * mm, "end": v(-55.2, 10.51) * mm});
            skLineSegment(sketch, "E235.MirrorCS", {"start": v(-66.38, 7) * mm, "end": v(-66.41, 6.86) * mm});
            skLineSegment(sketch, "E236.MirrorCS", {"start": v(-60.96, 8.57) * mm, "end": v(-61.07, 8.67) * mm});
            skLineSegment(sketch, "E237.MirrorCS", {"start": v(-57.34, 9.84) * mm, "end": v(-57.2, 9.88) * mm});
            skLineSegment(sketch, "E238.MirrorCS", {"start": v(-68.53, 6.34) * mm, "end": v(-68.56, 6.19) * mm});
            skLineSegment(sketch, "E239.MirrorCS", {"start": v(-72.26, 5.17) * mm, "end": v(-72.15, 5.06) * mm});
            skLineSegment(sketch, "E240.MirrorCS", {"start": v(-67.96, 6.52) * mm, "end": v(-68.1, 6.47) * mm});
            skLineSegment(sketch, "E241.MirrorCS", {"start": v(-66.38, 7) * mm, "end": v(-66.24, 7.05) * mm});
            skLineSegment(sketch, "E242.MirrorCS", {"start": v(-65.8, 7.19) * mm, "end": v(-65.7, 7.08) * mm});
            skLineSegment(sketch, "E243.MirrorCS", {"start": v(-64.23, 7.68) * mm, "end": v(-64.26, 7.53) * mm});
            skLineSegment(sketch, "E244.MirrorCS", {"start": v(-63.22, 8) * mm, "end": v(-63.11, 7.9) * mm});
            skLineSegment(sketch, "E245.MirrorCS", {"start": v(-70.69, 5.66) * mm, "end": v(-70.72, 5.51) * mm});
            skLineSegment(sketch, "E246.MirrorCS", {"start": v(-55.2, 10.51) * mm, "end": v(-55.22, 10.36) * mm});
            skLineSegment(sketch, "E247.MirrorCS", {"start": v(-70.11, 5.84) * mm, "end": v(-70.26, 5.8) * mm});
            skLineSegment(sketch, "E248.MirrorCS", {"start": v(-61.65, 8.5) * mm, "end": v(-61.68, 8.34) * mm});
            skLineSegment(sketch, "E249.MirrorCS", {"start": v(-59.5, 9.17) * mm, "end": v(-59.35, 9.21) * mm});
            skLineSegment(sketch, "E250.MirrorCS", {"start": v(-58.92, 9.35) * mm, "end": v(-58.81, 9.24) * mm});
            skLineSegment(sketch, "E251.MirrorCS", {"start": v(-56.66, 9.91) * mm, "end": v(-56.77, 10.02) * mm});
            skLineSegment(sketch, "E252.MirrorCS", {"start": v(-61.07, 8.67) * mm, "end": v(-61.22, 8.63) * mm});
            skLineSegment(sketch, "E253.MirrorCS", {"start": v(-61.68, 8.34) * mm, "end": v(-61.65, 8.5) * mm});
            skLineSegment(sketch, "E254.MirrorCS", {"start": v(-56.77, 10.02) * mm, "end": v(-56.66, 9.91) * mm});
            skLineSegment(sketch, "E255.MirrorCS", {"start": v(-72.15, 5.06) * mm, "end": v(-72.26, 5.17) * mm});
            skLineSegment(sketch, "E256.MirrorCS", {"start": v(-65.7, 7.08) * mm, "end": v(-65.8, 7.19) * mm});
            skLineSegment(sketch, "E257.MirrorCS", {"start": v(-58.81, 9.24) * mm, "end": v(-58.92, 9.35) * mm});
            skLineSegment(sketch, "E258.MirrorCS", {"start": v(-70.72, 5.51) * mm, "end": v(-70.69, 5.66) * mm});
            skLineSegment(sketch, "E259.MirrorCS", {"start": v(-57.52, 9.64) * mm, "end": v(-57.37, 9.69) * mm});
            skLineSegment(sketch, "E260.MirrorCS", {"start": v(-67.7, 6.46) * mm, "end": v(-67.85, 6.41) * mm});
            skLineSegment(sketch, "E261.MirrorCS", {"start": v(-59.67, 8.97) * mm, "end": v(-59.53, 9.02) * mm});
            skLineSegment(sketch, "E262.MirrorCS", {"start": v(-57.63, 9.75) * mm, "end": v(-57.52, 9.64) * mm});
            skLineSegment(sketch, "E263.MirrorCS", {"start": v(-66.56, 6.81) * mm, "end": v(-66.41, 6.86) * mm});
            skLineSegment(sketch, "E264.MirrorCS", {"start": v(-55.2, 10.51) * mm, "end": v(-55.05, 10.56) * mm});
            skLineSegment(sketch, "E265.MirrorCS", {"start": v(-60.82, 8.61) * mm, "end": v(-60.96, 8.57) * mm});
            skLineSegment(sketch, "E266.MirrorCS", {"start": v(-69.86, 5.78) * mm, "end": v(-70, 5.74) * mm});
            skLineSegment(sketch, "E267.MirrorCS", {"start": v(-65.8, 7.19) * mm, "end": v(-65.95, 7.14) * mm});
            skLineSegment(sketch, "E268.MirrorCS", {"start": v(-64.26, 7.53) * mm, "end": v(-64.23, 7.68) * mm});
            skLineSegment(sketch, "E269.MirrorCS", {"start": v(-62.97, 7.94) * mm, "end": v(-63.11, 7.9) * mm});
            skLineSegment(sketch, "E270.MirrorCS", {"start": v(-58.92, 9.35) * mm, "end": v(-59.07, 9.3) * mm});
            skLineSegment(sketch, "E271.MirrorCS", {"start": v(-61.22, 8.63) * mm, "end": v(-61.25, 8.48) * mm});
            skLineSegment(sketch, "E272.MirrorCS", {"start": v(-70.69, 5.66) * mm, "end": v(-70.54, 5.7) * mm});
            skLineSegment(sketch, "E273.MirrorCS", {"start": v(-72.26, 5.17) * mm, "end": v(-72.4, 5.12) * mm});
            skLineSegment(sketch, "E274.MirrorCS", {"start": v(-68.56, 6.19) * mm, "end": v(-68.53, 6.34) * mm});
            skLineSegment(sketch, "E275.MirrorCS", {"start": v(-56.77, 10.02) * mm, "end": v(-56.91, 9.97) * mm});
            skLineSegment(sketch, "E276.MirrorCS", {"start": v(-61.93, 8.4) * mm, "end": v(-61.82, 8.3) * mm});
            skLineSegment(sketch, "E277.MirrorCS", {"start": v(-64.4, 7.49) * mm, "end": v(-64.26, 7.53) * mm});
            skLineSegment(sketch, "E278.MirrorCS", {"start": v(-72, 5.1) * mm, "end": v(-72.15, 5.06) * mm});
            skLineSegment(sketch, "E279.MirrorCS", {"start": v(-56.51, 9.96) * mm, "end": v(-56.66, 9.91) * mm});
            skLineSegment(sketch, "E280.MirrorCS", {"start": v(-58.66, 9.29) * mm, "end": v(-58.81, 9.24) * mm});
            skLineSegment(sketch, "E281.MirrorCS", {"start": v(-55.37, 10.32) * mm, "end": v(-55.22, 10.36) * mm});
            skLineSegment(sketch, "E282.MirrorCS", {"start": v(-70.86, 5.47) * mm, "end": v(-70.72, 5.51) * mm});
            skLineSegment(sketch, "E283.MirrorCS", {"start": v(-66.24, 7.05) * mm, "end": v(-66.13, 6.95) * mm});
            skLineSegment(sketch, "E284.MirrorCS", {"start": v(-65.55, 7.13) * mm, "end": v(-65.7, 7.08) * mm});
            skLineSegment(sketch, "E285.MirrorCS", {"start": v(-63.11, 7.9) * mm, "end": v(-63.22, 8) * mm});
            skLineSegment(sketch, "E286.MirrorCS", {"start": v(-68.7, 6.14) * mm, "end": v(-68.56, 6.19) * mm});
            skLineSegment(sketch, "E287.MirrorCS", {"start": v(-70.26, 5.8) * mm, "end": v(-70.29, 5.65) * mm});
            skLineSegment(sketch, "E288.MirrorCS", {"start": v(-63.22, 8) * mm, "end": v(-63.37, 7.95) * mm});
            skLineSegment(sketch, "E289.MirrorCS", {"start": v(-68.1, 6.47) * mm, "end": v(-68.13, 6.32) * mm});
            skLineSegment(sketch, "E290.MirrorCS", {"start": v(-61.65, 8.5) * mm, "end": v(-61.5, 8.54) * mm});
            skLineSegment(sketch, "E291.MirrorCS", {"start": v(-68.53, 6.34) * mm, "end": v(-68.39, 6.38) * mm});
            skLineSegment(sketch, "E292.MirrorCS", {"start": v(-61.82, 8.3) * mm, "end": v(-61.68, 8.34) * mm});
            skLineSegment(sketch, "E293.MirrorCS", {"start": v(-57.2, 9.88) * mm, "end": v(-57.09, 9.78) * mm});
            skLineSegment(sketch, "E294.MirrorCS", {"start": v(-59.35, 9.21) * mm, "end": v(-59.24, 9.1) * mm});
            skLineSegment(sketch, "E295.MirrorCS", {"start": v(-64.23, 7.68) * mm, "end": v(-64.09, 7.73) * mm});
            skLineSegment(sketch, "E296.MirrorCS", {"start": v(-56.91, 9.97) * mm, "end": v(-56.94, 9.82) * mm});
            skLineSegment(sketch, "E297.MirrorCS", {"start": v(-61.25, 8.48) * mm, "end": v(-61.4, 8.43) * mm});
            skLineSegment(sketch, "E298.MirrorCS", {"start": v(-66.13, 6.95) * mm, "end": v(-65.98, 7) * mm});
            skLineSegment(sketch, "E299.MirrorCS", {"start": v(-72.4, 5.12) * mm, "end": v(-72.44, 4.97) * mm});
            skLineSegment(sketch, "E300.MirrorCS", {"start": v(-61.5, 8.54) * mm, "end": v(-61.4, 8.43) * mm});
            skLineSegment(sketch, "E301.MirrorCS", {"start": v(-54.62, 10.7) * mm, "end": v(-54.76, 10.65) * mm});
            skLineSegment(sketch, "E302.MirrorCS", {"start": v(-54.76, 10.65) * mm, "end": v(-54.8, 10.5) * mm});
            skLineSegment(sketch, "E303.MirrorCS", {"start": v(-65.95, 7.14) * mm, "end": v(-65.98, 7) * mm});
            skLineSegment(sketch, "E304.MirrorCS", {"start": v(-54.5, 10.59) * mm, "end": v(-54.62, 10.7) * mm});
            skLineSegment(sketch, "E305.MirrorCS", {"start": v(-72.58, 4.93) * mm, "end": v(-72.44, 4.97) * mm});
            skLineSegment(sketch, "E306.MirrorCS", {"start": v(-60.79, 8.76) * mm, "end": v(-60.82, 8.61) * mm});
            skLineSegment(sketch, "E307.MirrorCS", {"start": v(-57.09, 9.78) * mm, "end": v(-56.94, 9.82) * mm});
            skLineSegment(sketch, "E308.MirrorCS", {"start": v(-54.69, 10.67) * mm, "end": v(-54.61, 10.43) * mm, "construction": true});
            skLineSegment(sketch, "E309.MirrorCS", {"start": v(-59.07, 9.3) * mm, "end": v(-59.1, 9.15) * mm});
            skLineSegment(sketch, "E310.MirrorCS", {"start": v(-68.39, 6.38) * mm, "end": v(-68.28, 6.28) * mm});
            skLineSegment(sketch, "E311.MirrorCS", {"start": v(-62.36, 8.27) * mm, "end": v(-62.5, 8.22) * mm});
            skLineSegment(sketch, "E312.MirrorCS", {"start": v(-68.13, 6.32) * mm, "end": v(-68.28, 6.28) * mm});
            skLineSegment(sketch, "E313.MirrorCS", {"start": v(-65.52, 7.28) * mm, "end": v(-65.55, 7.13) * mm});
            skLineSegment(sketch, "E314.MirrorCS", {"start": v(-62.25, 8.16) * mm, "end": v(-62.36, 8.27) * mm});
            skLineSegment(sketch, "E315.MirrorCS", {"start": v(-70.54, 5.7) * mm, "end": v(-70.43, 5.6) * mm});
            skLineSegment(sketch, "E316.MirrorCS", {"start": v(-67.67, 6.6) * mm, "end": v(-67.7, 6.46) * mm});
            skLineSegment(sketch, "E317.MirrorCS", {"start": v(-62.5, 8.22) * mm, "end": v(-62.54, 8.07) * mm});
            skLineSegment(sketch, "E318.MirrorCS", {"start": v(-55.05, 10.56) * mm, "end": v(-54.94, 10.45) * mm});
            skLineSegment(sketch, "E319.MirrorCS", {"start": v(-59.78, 9.08) * mm, "end": v(-59.67, 8.97) * mm});
            skLineSegment(sketch, "E320.MirrorCS", {"start": v(-70.29, 5.65) * mm, "end": v(-70.43, 5.6) * mm});
            skLineSegment(sketch, "E321.MirrorCS", {"start": v(-54.8, 10.5) * mm, "end": v(-54.94, 10.45) * mm});
            skLineSegment(sketch, "E322.MirrorCS", {"start": v(-59.24, 9.1) * mm, "end": v(-59.1, 9.15) * mm});
            skLineSegment(sketch, "E323.MirrorCS", {"start": v(-71.15, 5.38) * mm, "end": v(-71.12, 5.53) * mm});
            skLineSegment(sketch, "E324.MirrorCS", {"start": v(-69.4, 6.07) * mm, "end": v(-69.25, 6.11) * mm});
            skLineSegment(sketch, "E325.MirrorCS", {"start": v(-69.14, 6) * mm, "end": v(-69, 6.05) * mm});
            skLineSegment(sketch, "E326.MirrorCS", {"start": v(-63.54, 7.76) * mm, "end": v(-63.4, 7.8) * mm});
            skLineSegment(sketch, "E327.MirrorCS", {"start": v(-65.12, 7.26) * mm, "end": v(-65.27, 7.22) * mm});
            skLineSegment(sketch, "E328.MirrorCS", {"start": v(-69.57, 5.87) * mm, "end": v(-69.68, 5.98) * mm});
            skLineSegment(sketch, "E329.MirrorCS", {"start": v(-71.83, 5.3) * mm, "end": v(-71.98, 5.26) * mm});
            skLineSegment(sketch, "E330.MirrorCS", {"start": v(-56.48, 10.1) * mm, "end": v(-56.51, 9.96) * mm});
            skLineSegment(sketch, "E331.MirrorCS", {"start": v(-71.58, 5.24) * mm, "end": v(-71.72, 5.2) * mm});
            skLineSegment(sketch, "E332.MirrorCS", {"start": v(-69.43, 5.92) * mm, "end": v(-69.57, 5.87) * mm});
            skLineSegment(sketch, "E333.MirrorCS", {"start": v(-71.98, 5.26) * mm, "end": v(-72, 5.1) * mm});
            skLineSegment(sketch, "E334.MirrorCS", {"start": v(-57.95, 9.5) * mm, "end": v(-57.8, 9.56) * mm});
            skLineSegment(sketch, "E335.MirrorCS", {"start": v(-71.3, 5.33) * mm, "end": v(-71.4, 5.44) * mm});
            skLineSegment(sketch, "E336.MirrorCS", {"start": v(-62.8, 8.13) * mm, "end": v(-62.94, 8.09) * mm});
            skLineSegment(sketch, "E337.MirrorCS", {"start": v(-60.1, 8.84) * mm, "end": v(-59.96, 8.88) * mm});
            skLineSegment(sketch, "E338.MirrorCS", {"start": v(-63.8, 7.82) * mm, "end": v(-63.65, 7.86) * mm});
            skLineSegment(sketch, "E339.MirrorCS", {"start": v(-60.64, 8.8) * mm, "end": v(-60.79, 8.76) * mm});
            skLineSegment(sketch, "E340.MirrorCS", {"start": v(-63.65, 7.86) * mm, "end": v(-63.54, 7.76) * mm});
            skLineSegment(sketch, "E341.MirrorCS", {"start": v(-58.23, 9.42) * mm, "end": v(-58.38, 9.37) * mm});
            skLineSegment(sketch, "E342.MirrorCS", {"start": v(-69.43, 5.92) * mm, "end": v(-69.4, 6.07) * mm});
            skLineSegment(sketch, "E343.MirrorCS", {"start": v(-69.83, 5.93) * mm, "end": v(-69.86, 5.78) * mm});
            skLineSegment(sketch, "E344.MirrorCS", {"start": v(-63.83, 7.67) * mm, "end": v(-63.98, 7.62) * mm});
            skLineSegment(sketch, "E345.MirrorCS", {"start": v(-64.52, 7.6) * mm, "end": v(-64.4, 7.49) * mm});
            skLineSegment(sketch, "E346.MirrorCS", {"start": v(-57.77, 9.7) * mm, "end": v(-57.63, 9.75) * mm});
            skLineSegment(sketch, "E347.MirrorCS", {"start": v(-57.8, 9.56) * mm, "end": v(-57.77, 9.7) * mm});
            skLineSegment(sketch, "E348.MirrorCS", {"start": v(-58.06, 9.62) * mm, "end": v(-58.2, 9.57) * mm});
            skLineSegment(sketch, "E349.MirrorCS", {"start": v(-59.96, 8.88) * mm, "end": v(-59.93, 9.03) * mm});
            skLineSegment(sketch, "E350.MirrorCS", {"start": v(-67.42, 6.54) * mm, "end": v(-67.53, 6.65) * mm});
            skLineSegment(sketch, "E351.MirrorCS", {"start": v(-64.95, 7.46) * mm, "end": v(-64.84, 7.35) * mm});
            skLineSegment(sketch, "E352.MirrorCS", {"start": v(-60.39, 8.75) * mm, "end": v(-60.36, 8.9) * mm});
            skLineSegment(sketch, "E353.MirrorCS", {"start": v(-66.67, 6.92) * mm, "end": v(-66.56, 6.81) * mm});
            skLineSegment(sketch, "E354.MirrorCS", {"start": v(-71.3, 5.33) * mm, "end": v(-71.15, 5.38) * mm});
            skLineSegment(sketch, "E355.MirrorCS", {"start": v(-67.1, 6.79) * mm, "end": v(-67.24, 6.74) * mm});
            skLineSegment(sketch, "E356.MirrorCS", {"start": v(-59.93, 9.03) * mm, "end": v(-59.78, 9.08) * mm});
            skLineSegment(sketch, "E357.MirrorCS", {"start": v(-62.54, 8.07) * mm, "end": v(-62.68, 8.03) * mm});
            skLineSegment(sketch, "E358.MirrorCS", {"start": v(-57.95, 9.5) * mm, "end": v(-58.06, 9.62) * mm});
            skLineSegment(sketch, "E359.MirrorCS", {"start": v(-66.99, 6.68) * mm, "end": v(-66.84, 6.73) * mm});
            skLineSegment(sketch, "E360.MirrorCS", {"start": v(-65.12, 7.26) * mm, "end": v(-65.1, 7.41) * mm});
            skLineSegment(sketch, "E361.MirrorCS", {"start": v(-71.4, 5.44) * mm, "end": v(-71.55, 5.4) * mm});
            skLineSegment(sketch, "E362.MirrorCS", {"start": v(-64.66, 7.55) * mm, "end": v(-64.52, 7.6) * mm});
            skLineSegment(sketch, "E363.MirrorCS", {"start": v(-63.37, 7.95) * mm, "end": v(-63.4, 7.8) * mm});
            skLineSegment(sketch, "E364.MirrorCS", {"start": v(-55.9, 10.29) * mm, "end": v(-55.8, 10.18) * mm});
            skLineSegment(sketch, "E365.MirrorCS", {"start": v(-56.08, 10.1) * mm, "end": v(-56.05, 10.24) * mm});
            skLineSegment(sketch, "E366.MirrorCS", {"start": v(-65.38, 7.32) * mm, "end": v(-65.52, 7.28) * mm});
            skLineSegment(sketch, "E367.MirrorCS", {"start": v(-71.55, 5.4) * mm, "end": v(-71.58, 5.24) * mm});
            skLineSegment(sketch, "E368.MirrorCS", {"start": v(-65.27, 7.22) * mm, "end": v(-65.38, 7.32) * mm});
            skLineSegment(sketch, "E369.MirrorCS", {"start": v(-58.2, 9.57) * mm, "end": v(-58.23, 9.42) * mm});
            skLineSegment(sketch, "E370.MirrorCS", {"start": v(-70.97, 5.57) * mm, "end": v(-70.86, 5.47) * mm});
            skLineSegment(sketch, "E371.MirrorCS", {"start": v(-68.97, 6.2) * mm, "end": v(-68.82, 6.25) * mm});
            skLineSegment(sketch, "E372.MirrorCS", {"start": v(-67.53, 6.65) * mm, "end": v(-67.67, 6.6) * mm});
            skLineSegment(sketch, "E373.MirrorCS", {"start": v(-58.64, 9.44) * mm, "end": v(-58.66, 9.29) * mm});
            skLineSegment(sketch, "E374.MirrorCS", {"start": v(-60.21, 8.94) * mm, "end": v(-60.1, 8.84) * mm});
            skLineSegment(sketch, "E375.MirrorCS", {"start": v(-71.12, 5.53) * mm, "end": v(-70.97, 5.57) * mm});
            skLineSegment(sketch, "E376.MirrorCS", {"start": v(-68.82, 6.25) * mm, "end": v(-68.7, 6.14) * mm});
            skLineSegment(sketch, "E377.MirrorCS", {"start": v(-62.68, 8.03) * mm, "end": v(-62.8, 8.13) * mm});
            skLineSegment(sketch, "E378.MirrorCS", {"start": v(-56.05, 10.24) * mm, "end": v(-55.9, 10.29) * mm});
            skLineSegment(sketch, "E379.MirrorCS", {"start": v(-66.81, 6.87) * mm, "end": v(-66.67, 6.92) * mm});
            skLineSegment(sketch, "E380.MirrorCS", {"start": v(-56.08, 10.1) * mm, "end": v(-56.23, 10.05) * mm});
            skLineSegment(sketch, "E381.MirrorCS", {"start": v(-67.24, 6.74) * mm, "end": v(-67.27, 6.6) * mm});
            skLineSegment(sketch, "E382.MirrorCS", {"start": v(-67.27, 6.6) * mm, "end": v(-67.42, 6.54) * mm});
            skLineSegment(sketch, "E383.MirrorCS", {"start": v(-55.8, 10.18) * mm, "end": v(-55.65, 10.23) * mm});
            skLineSegment(sketch, "E384.MirrorCS", {"start": v(-64.7, 7.4) * mm, "end": v(-64.66, 7.55) * mm});
            skLineSegment(sketch, "E385.MirrorCS", {"start": v(-66.99, 6.68) * mm, "end": v(-67.1, 6.79) * mm});
            skLineSegment(sketch, "E386.MirrorCS", {"start": v(-69, 6.05) * mm, "end": v(-68.97, 6.2) * mm});
            skLineSegment(sketch, "E387.MirrorCS", {"start": v(-62.1, 8.2) * mm, "end": v(-62.08, 8.36) * mm});
            skLineSegment(sketch, "E388.MirrorCS", {"start": v(-60.53, 8.7) * mm, "end": v(-60.64, 8.8) * mm});
            skLineSegment(sketch, "E389.MirrorCS", {"start": v(-65.1, 7.41) * mm, "end": v(-64.95, 7.46) * mm});
            skLineSegment(sketch, "E390.MirrorCS", {"start": v(-71.72, 5.2) * mm, "end": v(-71.83, 5.3) * mm});
            skLineSegment(sketch, "E391.MirrorCS", {"start": v(-56.23, 10.05) * mm, "end": v(-56.34, 10.15) * mm});
            skLineSegment(sketch, "E392.MirrorCS", {"start": v(-69.68, 5.98) * mm, "end": v(-69.83, 5.93) * mm});
            skLineSegment(sketch, "E393.MirrorCS", {"start": v(-62.25, 8.16) * mm, "end": v(-62.1, 8.2) * mm});
            skLineSegment(sketch, "E394.MirrorCS", {"start": v(-55.65, 10.23) * mm, "end": v(-55.62, 10.38) * mm});
            skLineSegment(sketch, "E395.MirrorCS", {"start": v(-60.39, 8.75) * mm, "end": v(-60.53, 8.7) * mm});
            skLineSegment(sketch, "E396.MirrorCS", {"start": v(-62.94, 8.09) * mm, "end": v(-62.97, 7.94) * mm});
            skLineSegment(sketch, "E397.MirrorCS", {"start": v(-66.84, 6.73) * mm, "end": v(-66.81, 6.87) * mm});
            skLineSegment(sketch, "E398.MirrorCS", {"start": v(-62.08, 8.36) * mm, "end": v(-61.93, 8.4) * mm});
            skLineSegment(sketch, "E399.MirrorCS", {"start": v(-64.09, 7.73) * mm, "end": v(-63.98, 7.62) * mm});
            skLineSegment(sketch, "E400.MirrorCS", {"start": v(-55.48, 10.42) * mm, "end": v(-55.37, 10.32) * mm});
            skLineSegment(sketch, "E401.MirrorCS", {"start": v(-58.38, 9.37) * mm, "end": v(-58.49, 9.48) * mm});
            skLineSegment(sketch, "E402.MirrorCS", {"start": v(-58.49, 9.48) * mm, "end": v(-58.64, 9.44) * mm});
            skLineSegment(sketch, "E403.MirrorCS", {"start": v(-60.36, 8.9) * mm, "end": v(-60.21, 8.94) * mm});
            skLineSegment(sketch, "E404.MirrorCS", {"start": v(-64.84, 7.35) * mm, "end": v(-64.7, 7.4) * mm});
            skLineSegment(sketch, "E405.MirrorCS", {"start": v(-69.25, 6.11) * mm, "end": v(-69.14, 6) * mm});
            skLineSegment(sketch, "E406.MirrorCS", {"start": v(-56.34, 10.15) * mm, "end": v(-56.48, 10.1) * mm});
            skLineSegment(sketch, "E407.MirrorCS", {"start": v(-55.62, 10.38) * mm, "end": v(-55.48, 10.42) * mm});
            skLineSegment(sketch, "E408.MirrorCS", {"start": v(-63.73, 7.84) * mm, "end": v(-63.63, 7.54) * mm, "construction": true});
            skLineSegment(sketch, "E409.MirrorCS", {"start": v(-30.26, 18.18) * mm, "end": v(-30.23, 18.33) * mm});
            skLineSegment(sketch, "E410.MirrorCS", {"start": v(-30.23, 18.33) * mm, "end": v(-30.08, 18.38) * mm});
            skLineSegment(sketch, "E411.MirrorCS", {"start": v(-30.23, 18.33) * mm, "end": v(-30.26, 18.18) * mm});
            skLineSegment(sketch, "E412.MirrorCS", {"start": v(-30.08, 18.38) * mm, "end": v(-29.97, 18.27) * mm});
            skLineSegment(sketch, "E413.MirrorCS", {"start": v(-30.51, 18.24) * mm, "end": v(-30.4, 18.13) * mm});
            skLineSegment(sketch, "E414.MirrorCS", {"start": v(-37.11, 16.17) * mm, "end": v(-37.14, 16.02) * mm});
            skLineSegment(sketch, "E415.MirrorCS", {"start": v(-30.4, 18.13) * mm, "end": v(-30.26, 18.18) * mm});
            skLineSegment(sketch, "E416.MirrorCS", {"start": v(-30.66, 18.2) * mm, "end": v(-30.51, 18.24) * mm});
            skLineSegment(sketch, "E417.MirrorCS", {"start": v(-29.97, 18.27) * mm, "end": v(-29.83, 18.32) * mm});
            skLineSegment(sketch, "E418.MirrorCS", {"start": v(-48.33, 12.52) * mm, "end": v(-48.3, 12.67) * mm});
            skLineSegment(sketch, "E419.MirrorCS", {"start": v(-21.22, 21.01) * mm, "end": v(-21.19, 21.16) * mm});
            skLineSegment(sketch, "E420.MirrorCS", {"start": v(-37.14, 16.02) * mm, "end": v(-37.11, 16.17) * mm});
            skLineSegment(sketch, "E421.MirrorCS", {"start": v(-48.3, 12.67) * mm, "end": v(-48.33, 12.52) * mm});
            skLineSegment(sketch, "E422.MirrorCS", {"start": v(-33.85, 17.06) * mm, "end": v(-33.96, 17.16) * mm});
            skLineSegment(sketch, "E423.MirrorCS", {"start": v(-52.03, 11.5) * mm, "end": v(-51.92, 11.4) * mm});
            skLineSegment(sketch, "E424.MirrorCS", {"start": v(-36.97, 16.22) * mm, "end": v(-36.86, 16.11) * mm});
            skLineSegment(sketch, "E425.MirrorCS", {"start": v(-31.8, 17.84) * mm, "end": v(-31.7, 17.73) * mm});
            skLineSegment(sketch, "E426.MirrorCS", {"start": v(-49.88, 12.18) * mm, "end": v(-49.77, 12.07) * mm});
            skLineSegment(sketch, "E427.MirrorCS", {"start": v(-21.19, 21.16) * mm, "end": v(-21.22, 21.01) * mm});
            skLineSegment(sketch, "E428.MirrorCS", {"start": v(-39.27, 15.5) * mm, "end": v(-39.3, 15.35) * mm});
            skLineSegment(sketch, "E429.MirrorCS", {"start": v(-24.92, 20) * mm, "end": v(-24.8, 19.89) * mm});
            skLineSegment(sketch, "E430.MirrorCS", {"start": v(-43, 14.33) * mm, "end": v(-42.88, 14.23) * mm});
            skLineSegment(sketch, "E431.MirrorCS", {"start": v(-41.45, 14.68) * mm, "end": v(-41.42, 14.83) * mm});
            skLineSegment(sketch, "E432.MirrorCS", {"start": v(-23.37, 20.34) * mm, "end": v(-23.34, 20.49) * mm});
            skLineSegment(sketch, "E433.MirrorCS", {"start": v(-37.11, 16.17) * mm, "end": v(-36.97, 16.22) * mm});
            skLineSegment(sketch, "E434.MirrorCS", {"start": v(-36.71, 16.16) * mm, "end": v(-36.86, 16.11) * mm});
            skLineSegment(sketch, "E435.MirrorCS", {"start": v(-41.42, 14.83) * mm, "end": v(-41.45, 14.68) * mm});
            skLineSegment(sketch, "E436.MirrorCS", {"start": v(-34.53, 16.98) * mm, "end": v(-34.56, 16.83) * mm});
            skLineSegment(sketch, "E437.MirrorCS", {"start": v(-43, 14.33) * mm, "end": v(-43.14, 14.29) * mm});
            skLineSegment(sketch, "E438.MirrorCS", {"start": v(-37.54, 16.04) * mm, "end": v(-37.4, 16.08) * mm});
            skLineSegment(sketch, "E439.MirrorCS", {"start": v(-21.04, 21.2) * mm, "end": v(-20.93, 21.1) * mm});
            skLineSegment(sketch, "E440.MirrorCS", {"start": v(-31.7, 17.73) * mm, "end": v(-31.8, 17.84) * mm});
            skLineSegment(sketch, "E441.MirrorCS", {"start": v(-48.3, 12.67) * mm, "end": v(-48.16, 12.72) * mm});
            skLineSegment(sketch, "E442.MirrorCS", {"start": v(-23.34, 20.49) * mm, "end": v(-23.2, 20.53) * mm});
            skLineSegment(sketch, "E443.MirrorCS", {"start": v(-37.29, 15.98) * mm, "end": v(-37.14, 16.02) * mm});
            skLineSegment(sketch, "E444.MirrorCS", {"start": v(-39.3, 15.35) * mm, "end": v(-39.27, 15.5) * mm});
            skLineSegment(sketch, "E445.MirrorCS", {"start": v(-37.4, 16.08) * mm, "end": v(-37.29, 15.98) * mm});
            skLineSegment(sketch, "E446.MirrorCS", {"start": v(-42.88, 14.23) * mm, "end": v(-43, 14.33) * mm});
            skLineSegment(sketch, "E447.MirrorCS", {"start": v(-33.96, 17.16) * mm, "end": v(-33.85, 17.06) * mm});
            skLineSegment(sketch, "E448.MirrorCS", {"start": v(-48.16, 12.72) * mm, "end": v(-48.05, 12.6) * mm});
            skLineSegment(sketch, "E449.MirrorCS", {"start": v(-43.14, 14.29) * mm, "end": v(-43.17, 14.14) * mm});
            skLineSegment(sketch, "E450.MirrorCS", {"start": v(-41.42, 14.83) * mm, "end": v(-41.27, 14.87) * mm});
            skLineSegment(sketch, "E451.MirrorCS", {"start": v(-24.92, 20) * mm, "end": v(-25.06, 19.95) * mm});
            skLineSegment(sketch, "E452.MirrorCS", {"start": v(-27.07, 19.32) * mm, "end": v(-26.96, 19.21) * mm});
            skLineSegment(sketch, "E453.MirrorCS", {"start": v(-32.38, 17.66) * mm, "end": v(-32.4, 17.5) * mm});
            skLineSegment(sketch, "E454.MirrorCS", {"start": v(-43.57, 14.15) * mm, "end": v(-43.6, 14) * mm});
            skLineSegment(sketch, "E455.MirrorCS", {"start": v(-38.7, 15.68) * mm, "end": v(-38.58, 15.57) * mm});
            skLineSegment(sketch, "E456.MirrorCS", {"start": v(-40.84, 15) * mm, "end": v(-40.73, 14.9) * mm});
            skLineSegment(sketch, "E457.MirrorCS", {"start": v(-19.07, 21.68) * mm, "end": v(-19.04, 21.83) * mm});
            skLineSegment(sketch, "E458.MirrorCS", {"start": v(-21.19, 21.16) * mm, "end": v(-21.04, 21.2) * mm});
            skLineSegment(sketch, "E459.MirrorCS", {"start": v(-54.08, 10.72) * mm, "end": v(-54.19, 10.83) * mm});
            skLineSegment(sketch, "E460.MirrorCS", {"start": v(-34.56, 16.83) * mm, "end": v(-34.53, 16.98) * mm});
            skLineSegment(sketch, "E461.MirrorCS", {"start": v(-41.27, 14.87) * mm, "end": v(-41.16, 14.77) * mm});
            skLineSegment(sketch, "E462.MirrorCS", {"start": v(-49.88, 12.18) * mm, "end": v(-50.03, 12.13) * mm});
            skLineSegment(sketch, "E463.MirrorCS", {"start": v(-52.18, 11.46) * mm, "end": v(-52.2, 11.3) * mm});
            skLineSegment(sketch, "E464.MirrorCS", {"start": v(-22.76, 20.67) * mm, "end": v(-22.66, 20.56) * mm});
            skLineSegment(sketch, "E465.MirrorCS", {"start": v(-49.77, 12.07) * mm, "end": v(-49.88, 12.18) * mm});
            skLineSegment(sketch, "E466.MirrorCS", {"start": v(-23.34, 20.49) * mm, "end": v(-23.37, 20.34) * mm});
            skLineSegment(sketch, "E467.MirrorCS", {"start": v(-24.8, 19.89) * mm, "end": v(-24.92, 20) * mm});
            skLineSegment(sketch, "E468.MirrorCS", {"start": v(-48.48, 12.47) * mm, "end": v(-48.33, 12.52) * mm});
            skLineSegment(sketch, "E469.MirrorCS", {"start": v(-21.36, 20.96) * mm, "end": v(-21.22, 21.01) * mm});
            skLineSegment(sketch, "E470.MirrorCS", {"start": v(-20.93, 21.1) * mm, "end": v(-20.79, 21.15) * mm});
            skLineSegment(sketch, "E471.MirrorCS", {"start": v(-48.05, 12.6) * mm, "end": v(-47.9, 12.65) * mm});
            skLineSegment(sketch, "E472.MirrorCS", {"start": v(-25.06, 19.95) * mm, "end": v(-25.1, 19.8) * mm});
            skLineSegment(sketch, "E473.MirrorCS", {"start": v(-21.47, 21.07) * mm, "end": v(-21.36, 20.96) * mm});
            skLineSegment(sketch, "E474.MirrorCS", {"start": v(-21.62, 21.03) * mm, "end": v(-21.47, 21.07) * mm});
            skLineSegment(sketch, "E475.MirrorCS", {"start": v(-52.03, 11.5) * mm, "end": v(-52.18, 11.46) * mm});
            skLineSegment(sketch, "E476.MirrorCS", {"start": v(-28.08, 19) * mm, "end": v(-28.1, 18.85) * mm});
            skLineSegment(sketch, "E477.MirrorCS", {"start": v(-48.6, 12.58) * mm, "end": v(-48.48, 12.47) * mm});
            skLineSegment(sketch, "E478.MirrorCS", {"start": v(-51.92, 11.4) * mm, "end": v(-52.03, 11.5) * mm});
            skLineSegment(sketch, "E479.MirrorCS", {"start": v(-34.1, 17.12) * mm, "end": v(-34.13, 16.97) * mm});
            skLineSegment(sketch, "E480.MirrorCS", {"start": v(-23.63, 20.4) * mm, "end": v(-23.52, 20.3) * mm});
            skLineSegment(sketch, "E481.MirrorCS", {"start": v(-39.12, 15.55) * mm, "end": v(-39.01, 15.44) * mm});
            skLineSegment(sketch, "E482.MirrorCS", {"start": v(-47.73, 12.85) * mm, "end": v(-47.62, 12.74) * mm});
            skLineSegment(sketch, "E483.MirrorCS", {"start": v(-31.8, 17.84) * mm, "end": v(-31.95, 17.8) * mm});
            skLineSegment(sketch, "E484.MirrorCS", {"start": v(-45.15, 13.66) * mm, "end": v(-45.04, 13.55) * mm});
            skLineSegment(sketch, "E485.MirrorCS", {"start": v(-52.6, 11.32) * mm, "end": v(-52.46, 11.37) * mm});
            skLineSegment(sketch, "E486.MirrorCS", {"start": v(-38.58, 15.57) * mm, "end": v(-38.7, 15.68) * mm});
            skLineSegment(sketch, "E487.MirrorCS", {"start": v(-47.87, 12.8) * mm, "end": v(-47.9, 12.65) * mm});
            skLineSegment(sketch, "E488.MirrorCS", {"start": v(-19.04, 21.83) * mm, "end": v(-19.07, 21.68) * mm});
            skLineSegment(sketch, "E489.MirrorCS", {"start": v(-33.96, 17.16) * mm, "end": v(-34.1, 17.12) * mm});
            skLineSegment(sketch, "E490.MirrorCS", {"start": v(-29.54, 18.4) * mm, "end": v(-29.65, 18.51) * mm});
            skLineSegment(sketch, "E491.MirrorCS", {"start": v(-46.15, 13.34) * mm, "end": v(-46.18, 13.2) * mm});
            skLineSegment(sketch, "E492.MirrorCS", {"start": v(-22.66, 20.56) * mm, "end": v(-22.76, 20.67) * mm});
            skLineSegment(sketch, "E493.MirrorCS", {"start": v(-49.6, 12.27) * mm, "end": v(-49.63, 12.12) * mm});
            skLineSegment(sketch, "E494.MirrorCS", {"start": v(-54.33, 10.78) * mm, "end": v(-54.36, 10.63) * mm});
            skLineSegment(sketch, "E495.MirrorCS", {"start": v(-39.27, 15.5) * mm, "end": v(-39.12, 15.55) * mm});
            skLineSegment(sketch, "E496.MirrorCS", {"start": v(-36.1, 16.49) * mm, "end": v(-36, 16.38) * mm});
            skLineSegment(sketch, "E497.MirrorCS", {"start": v(-23.2, 20.53) * mm, "end": v(-23.09, 20.43) * mm});
            skLineSegment(sketch, "E498.MirrorCS", {"start": v(-31.95, 17.8) * mm, "end": v(-31.98, 17.64) * mm});
            skLineSegment(sketch, "E499.MirrorCS", {"start": v(-20.5, 21.23) * mm, "end": v(-20.61, 21.34) * mm});
            skLineSegment(sketch, "E500.MirrorCS", {"start": v(-54.19, 10.83) * mm, "end": v(-54.08, 10.72) * mm});
            skLineSegment(sketch, "E501.MirrorCS", {"start": v(-43.43, 14.2) * mm, "end": v(-43.32, 14.1) * mm});
            skLineSegment(sketch, "E502.MirrorCS", {"start": v(-25.5, 19.81) * mm, "end": v(-25.52, 19.66) * mm});
            skLineSegment(sketch, "E503.MirrorCS", {"start": v(-52.6, 11.32) * mm, "end": v(-52.64, 11.17) * mm});
            skLineSegment(sketch, "E504.MirrorCS", {"start": v(-50.46, 12) * mm, "end": v(-50.49, 11.85) * mm});
            skLineSegment(sketch, "E505.MirrorCS", {"start": v(-40.84, 15) * mm, "end": v(-40.99, 14.96) * mm});
            skLineSegment(sketch, "E506.MirrorCS", {"start": v(-50.03, 12.13) * mm, "end": v(-50.06, 11.98) * mm});
            skLineSegment(sketch, "E507.MirrorCS", {"start": v(-43.17, 14.14) * mm, "end": v(-43.32, 14.1) * mm});
            skLineSegment(sketch, "E508.MirrorCS", {"start": v(-41.16, 14.77) * mm, "end": v(-41.02, 14.81) * mm});
            skLineSegment(sketch, "E509.MirrorCS", {"start": v(-24.63, 20.08) * mm, "end": v(-24.66, 19.93) * mm});
            skLineSegment(sketch, "E510.MirrorCS", {"start": v(-39.55, 15.41) * mm, "end": v(-39.44, 15.3) * mm});
            skLineSegment(sketch, "E511.MirrorCS", {"start": v(-31.55, 17.78) * mm, "end": v(-31.7, 17.73) * mm});
            skLineSegment(sketch, "E512.MirrorCS", {"start": v(-54.19, 10.83) * mm, "end": v(-54.33, 10.78) * mm});
            skLineSegment(sketch, "E513.MirrorCS", {"start": v(-34.53, 16.98) * mm, "end": v(-34.39, 17.03) * mm});
            skLineSegment(sketch, "E514.MirrorCS", {"start": v(-22.91, 20.62) * mm, "end": v(-22.94, 20.47) * mm});
            skLineSegment(sketch, "E515.MirrorCS", {"start": v(-23.52, 20.3) * mm, "end": v(-23.37, 20.34) * mm});
            skLineSegment(sketch, "E516.MirrorCS", {"start": v(-40.99, 14.96) * mm, "end": v(-41.02, 14.81) * mm});
            skLineSegment(sketch, "E517.MirrorCS", {"start": v(-42.74, 14.27) * mm, "end": v(-42.88, 14.23) * mm});
            skLineSegment(sketch, "E518.MirrorCS", {"start": v(-24.49, 20.13) * mm, "end": v(-24.63, 20.08) * mm});
            skLineSegment(sketch, "E519.MirrorCS", {"start": v(-49.45, 12.31) * mm, "end": v(-49.6, 12.27) * mm});
            skLineSegment(sketch, "E520.MirrorCS", {"start": v(-31.98, 17.64) * mm, "end": v(-32.12, 17.6) * mm});
            skLineSegment(sketch, "E521.MirrorCS", {"start": v(-33.67, 17.25) * mm, "end": v(-33.7, 17.1) * mm});
            skLineSegment(sketch, "E522.MirrorCS", {"start": v(-48.74, 12.53) * mm, "end": v(-48.6, 12.58) * mm});
            skLineSegment(sketch, "E523.MirrorCS", {"start": v(-52.2, 11.3) * mm, "end": v(-52.35, 11.26) * mm});
            skLineSegment(sketch, "E524.MirrorCS", {"start": v(-24.66, 19.93) * mm, "end": v(-24.8, 19.89) * mm});
            skLineSegment(sketch, "E525.MirrorCS", {"start": v(-38.4, 15.77) * mm, "end": v(-38.44, 15.62) * mm});
            skLineSegment(sketch, "E526.MirrorCS", {"start": v(-50.06, 11.98) * mm, "end": v(-50.2, 11.94) * mm});
            skLineSegment(sketch, "E527.MirrorCS", {"start": v(-52.46, 11.37) * mm, "end": v(-52.35, 11.26) * mm});
            skLineSegment(sketch, "E528.MirrorCS", {"start": v(-34.39, 17.03) * mm, "end": v(-34.28, 16.92) * mm});
            skLineSegment(sketch, "E529.MirrorCS", {"start": v(-23.77, 20.35) * mm, "end": v(-23.63, 20.4) * mm});
            skLineSegment(sketch, "E530.MirrorCS", {"start": v(-20.61, 21.34) * mm, "end": v(-20.5, 21.23) * mm});
            skLineSegment(sketch, "E531.MirrorCS", {"start": v(-23.09, 20.43) * mm, "end": v(-22.94, 20.47) * mm});
            skLineSegment(sketch, "E532.MirrorCS", {"start": v(-42.7, 14.42) * mm, "end": v(-42.74, 14.27) * mm});
            skLineSegment(sketch, "E533.MirrorCS", {"start": v(-51.75, 11.6) * mm, "end": v(-51.78, 11.44) * mm});
            skLineSegment(sketch, "E534.MirrorCS", {"start": v(-31.37, 17.97) * mm, "end": v(-31.52, 17.93) * mm});
            skLineSegment(sketch, "E535.MirrorCS", {"start": v(-33.53, 17.3) * mm, "end": v(-33.67, 17.25) * mm});
            skLineSegment(sketch, "E536.MirrorCS", {"start": v(-31.52, 17.93) * mm, "end": v(-31.55, 17.78) * mm});
            skLineSegment(sketch, "E537.MirrorCS", {"start": v(-51.6, 11.64) * mm, "end": v(-51.75, 11.6) * mm});
            skLineSegment(sketch, "E538.MirrorCS", {"start": v(-27.07, 19.32) * mm, "end": v(-27.21, 19.27) * mm});
            skLineSegment(sketch, "E539.MirrorCS", {"start": v(-25.1, 19.8) * mm, "end": v(-25.24, 19.75) * mm});
            skLineSegment(sketch, "E540.MirrorCS", {"start": v(-34.7, 16.79) * mm, "end": v(-34.56, 16.83) * mm});
            skLineSegment(sketch, "E541.MirrorCS", {"start": v(-38.84, 15.63) * mm, "end": v(-38.87, 15.48) * mm});
            skLineSegment(sketch, "E542.MirrorCS", {"start": v(-41.7, 14.74) * mm, "end": v(-41.6, 14.63) * mm});
            skLineSegment(sketch, "E543.MirrorCS", {"start": v(-43.57, 14.15) * mm, "end": v(-43.43, 14.2) * mm});
            skLineSegment(sketch, "E544.MirrorCS", {"start": v(-39.01, 15.44) * mm, "end": v(-38.87, 15.48) * mm});
            skLineSegment(sketch, "E545.MirrorCS", {"start": v(-47.73, 12.85) * mm, "end": v(-47.87, 12.8) * mm});
            skLineSegment(sketch, "E546.MirrorCS", {"start": v(-36.71, 16.16) * mm, "end": v(-36.68, 16.3) * mm});
            skLineSegment(sketch, "E547.MirrorCS", {"start": v(-41.6, 14.63) * mm, "end": v(-41.45, 14.68) * mm});
            skLineSegment(sketch, "E548.MirrorCS", {"start": v(-39.44, 15.3) * mm, "end": v(-39.3, 15.35) * mm});
            skLineSegment(sketch, "E549.MirrorCS", {"start": v(-36, 16.38) * mm, "end": v(-36.1, 16.49) * mm});
            skLineSegment(sketch, "E550.MirrorCS", {"start": v(-29.65, 18.51) * mm, "end": v(-29.54, 18.4) * mm});
            skLineSegment(sketch, "E551.MirrorCS", {"start": v(-49.63, 12.12) * mm, "end": v(-49.77, 12.07) * mm});
            skLineSegment(sketch, "E552.MirrorCS", {"start": v(-25.52, 19.66) * mm, "end": v(-25.5, 19.81) * mm});
            skLineSegment(sketch, "E553.MirrorCS", {"start": v(-33.7, 17.1) * mm, "end": v(-33.85, 17.06) * mm});
            skLineSegment(sketch, "E554.MirrorCS", {"start": v(-51.78, 11.44) * mm, "end": v(-51.92, 11.4) * mm});
            skLineSegment(sketch, "E555.MirrorCS", {"start": v(-34.13, 16.97) * mm, "end": v(-34.28, 16.92) * mm});
            skLineSegment(sketch, "E556.MirrorCS", {"start": v(-40.73, 14.9) * mm, "end": v(-40.84, 15) * mm});
            skLineSegment(sketch, "E557.MirrorCS", {"start": v(-40.59, 14.95) * mm, "end": v(-40.73, 14.9) * mm});
            skLineSegment(sketch, "E558.MirrorCS", {"start": v(-35, 16.7) * mm, "end": v(-34.96, 16.85) * mm});
            skLineSegment(sketch, "E559.MirrorCS", {"start": v(-27.39, 19.08) * mm, "end": v(-27.24, 19.12) * mm});
            skLineSegment(sketch, "E560.MirrorCS", {"start": v(-26.81, 19.26) * mm, "end": v(-26.96, 19.21) * mm});
            skLineSegment(sketch, "E561.MirrorCS", {"start": v(-39.7, 15.36) * mm, "end": v(-39.55, 15.41) * mm});
            skLineSegment(sketch, "E562.MirrorCS", {"start": v(-40.56, 15.1) * mm, "end": v(-40.59, 14.95) * mm});
            skLineSegment(sketch, "E563.MirrorCS", {"start": v(-33.42, 17.2) * mm, "end": v(-33.53, 17.3) * mm});
            skLineSegment(sketch, "E564.MirrorCS", {"start": v(-22.76, 20.67) * mm, "end": v(-22.91, 20.62) * mm});
            skLineSegment(sketch, "E565.MirrorCS", {"start": v(-38.26, 15.81) * mm, "end": v(-38.4, 15.77) * mm});
            skLineSegment(sketch, "E566.MirrorCS", {"start": v(-43.6, 14) * mm, "end": v(-43.57, 14.15) * mm});
            skLineSegment(sketch, "E567.MirrorCS", {"start": v(-38.7, 15.68) * mm, "end": v(-38.84, 15.63) * mm});
            skLineSegment(sketch, "E568.MirrorCS", {"start": v(-32.4, 17.5) * mm, "end": v(-32.38, 17.66) * mm});
            skLineSegment(sketch, "E569.MirrorCS", {"start": v(-50.31, 12.04) * mm, "end": v(-50.2, 11.94) * mm});
            skLineSegment(sketch, "E570.MirrorCS", {"start": v(-32.23, 17.7) * mm, "end": v(-32.12, 17.6) * mm});
            skLineSegment(sketch, "E571.MirrorCS", {"start": v(-27.5, 19.18) * mm, "end": v(-27.39, 19.08) * mm});
            skLineSegment(sketch, "E572.MirrorCS", {"start": v(-20.36, 21.28) * mm, "end": v(-20.5, 21.23) * mm});
            skLineSegment(sketch, "E573.MirrorCS", {"start": v(-41.85, 14.7) * mm, "end": v(-41.7, 14.74) * mm});
            skLineSegment(sketch, "E574.MirrorCS", {"start": v(-48.77, 12.39) * mm, "end": v(-48.74, 12.53) * mm});
            skLineSegment(sketch, "E575.MirrorCS", {"start": v(-50.46, 12) * mm, "end": v(-50.31, 12.04) * mm});
            skLineSegment(sketch, "E576.MirrorCS", {"start": v(-38.44, 15.62) * mm, "end": v(-38.58, 15.57) * mm});
            skLineSegment(sketch, "E577.MirrorCS", {"start": v(-33.27, 17.24) * mm, "end": v(-33.24, 17.39) * mm});
            skLineSegment(sketch, "E578.MirrorCS", {"start": v(-40.41, 15.14) * mm, "end": v(-40.56, 15.1) * mm});
            skLineSegment(sketch, "E579.MirrorCS", {"start": v(-50.63, 11.8) * mm, "end": v(-50.49, 11.85) * mm});
            skLineSegment(sketch, "E580.MirrorCS", {"start": v(-52.64, 11.17) * mm, "end": v(-52.6, 11.32) * mm});
            skLineSegment(sketch, "E581.MirrorCS", {"start": v(-34.82, 16.9) * mm, "end": v(-34.7, 16.79) * mm});
            skLineSegment(sketch, "E582.MirrorCS", {"start": v(-27.21, 19.27) * mm, "end": v(-27.24, 19.12) * mm});
            skLineSegment(sketch, "E583.MirrorCS", {"start": v(-36.25, 16.44) * mm, "end": v(-36.28, 16.3) * mm});
            skLineSegment(sketch, "E584.MirrorCS", {"start": v(-32.38, 17.66) * mm, "end": v(-32.23, 17.7) * mm});
            skLineSegment(sketch, "E585.MirrorCS", {"start": v(-25.35, 19.86) * mm, "end": v(-25.24, 19.75) * mm});
            skLineSegment(sketch, "E586.MirrorCS", {"start": v(-43.86, 14.06) * mm, "end": v(-43.75, 13.96) * mm});
            skLineSegment(sketch, "E587.MirrorCS", {"start": v(-25.67, 19.62) * mm, "end": v(-25.52, 19.66) * mm});
            skLineSegment(sketch, "E588.MirrorCS", {"start": v(-19.5, 21.55) * mm, "end": v(-19.47, 21.7) * mm});
            skLineSegment(sketch, "E589.MirrorCS", {"start": v(-52.9, 11.23) * mm, "end": v(-52.78, 11.13) * mm});
            skLineSegment(sketch, "E590.MirrorCS", {"start": v(-18.6, 21.97) * mm, "end": v(-18.64, 21.82) * mm});
            skLineSegment(sketch, "E591.MirrorCS", {"start": v(-18.64, 21.82) * mm, "end": v(-18.78, 21.77) * mm});
            skLineSegment(sketch, "E592.MirrorCS", {"start": v(-18.9, 21.88) * mm, "end": v(-18.78, 21.77) * mm});
            skLineSegment(sketch, "E593.MirrorCS", {"start": v(-19.04, 21.83) * mm, "end": v(-18.9, 21.88) * mm});
            skLineSegment(sketch, "E594.MirrorCS", {"start": v(-22.5, 20.6) * mm, "end": v(-22.66, 20.56) * mm});
            skLineSegment(sketch, "E595.MirrorCS", {"start": v(-22.48, 20.76) * mm, "end": v(-22.5, 20.6) * mm});
            skLineSegment(sketch, "E596.MirrorCS", {"start": v(-19.21, 21.64) * mm, "end": v(-19.07, 21.68) * mm});
            skLineSegment(sketch, "E597.MirrorCS", {"start": v(-19.32, 21.74) * mm, "end": v(-19.21, 21.64) * mm});
            skLineSegment(sketch, "E598.MirrorCS", {"start": v(-19.47, 21.7) * mm, "end": v(-19.32, 21.74) * mm});
            skLineSegment(sketch, "E599.MirrorCS", {"start": v(-51.5, 11.53) * mm, "end": v(-51.6, 11.64) * mm});
            skLineSegment(sketch, "E600.MirrorCS", {"start": v(-41.88, 14.54) * mm, "end": v(-41.85, 14.7) * mm});
            skLineSegment(sketch, "E601.MirrorCS", {"start": v(-26.78, 19.4) * mm, "end": v(-26.81, 19.26) * mm});
            skLineSegment(sketch, "E602.MirrorCS", {"start": v(-34.96, 16.85) * mm, "end": v(-34.82, 16.9) * mm});
            skLineSegment(sketch, "E603.MirrorCS", {"start": v(-32.55, 17.46) * mm, "end": v(-32.4, 17.5) * mm});
            skLineSegment(sketch, "E604.MirrorCS", {"start": v(-26.96, 19.21) * mm, "end": v(-27.07, 19.32) * mm});
            skLineSegment(sketch, "E605.MirrorCS", {"start": v(-45.3, 13.61) * mm, "end": v(-45.32, 13.46) * mm});
            skLineSegment(sketch, "E606.MirrorCS", {"start": v(-53.9, 10.92) * mm, "end": v(-53.93, 10.77) * mm});
            skLineSegment(sketch, "E607.MirrorCS", {"start": v(-29.8, 18.46) * mm, "end": v(-29.83, 18.32) * mm});
            skLineSegment(sketch, "E608.MirrorCS", {"start": v(-25.5, 19.81) * mm, "end": v(-25.35, 19.86) * mm});
            skLineSegment(sketch, "E609.MirrorCS", {"start": v(-22.33, 20.8) * mm, "end": v(-22.48, 20.76) * mm});
            skLineSegment(sketch, "E610.MirrorCS", {"start": v(-22.22, 20.7) * mm, "end": v(-22.33, 20.8) * mm});
            skLineSegment(sketch, "E611.MirrorCS", {"start": v(-24.38, 20.02) * mm, "end": v(-24.49, 20.13) * mm});
            skLineSegment(sketch, "E612.MirrorCS", {"start": v(-36.68, 16.3) * mm, "end": v(-36.54, 16.35) * mm});
            skLineSegment(sketch, "E613.MirrorCS", {"start": v(-20.76, 21.3) * mm, "end": v(-20.79, 21.15) * mm});
            skLineSegment(sketch, "E614.MirrorCS", {"start": v(-45.47, 13.42) * mm, "end": v(-45.32, 13.46) * mm});
            skLineSegment(sketch, "E615.MirrorCS", {"start": v(-50.49, 11.85) * mm, "end": v(-50.46, 12) * mm});
            skLineSegment(sketch, "E616.MirrorCS", {"start": v(-29.65, 18.51) * mm, "end": v(-29.8, 18.46) * mm});
            skLineSegment(sketch, "E617.MirrorCS", {"start": v(-28.1, 18.85) * mm, "end": v(-28.08, 19) * mm});
            skLineSegment(sketch, "E618.MirrorCS", {"start": v(-46.18, 13.2) * mm, "end": v(-46.15, 13.34) * mm});
            skLineSegment(sketch, "E619.MirrorCS", {"start": v(-35.68, 16.62) * mm, "end": v(-35.82, 16.58) * mm});
            skLineSegment(sketch, "E620.MirrorCS", {"start": v(-27.57, 19.16) * mm, "end": v(-27.48, 18.86) * mm, "construction": true});
            skLineSegment(sketch, "E621.MirrorCS", {"start": v(-20.33, 21.43) * mm, "end": v(-20.36, 21.28) * mm});
            skLineSegment(sketch, "E622.MirrorCS", {"start": v(-53.76, 10.96) * mm, "end": v(-53.9, 10.92) * mm});
            skLineSegment(sketch, "E623.MirrorCS", {"start": v(-43.75, 13.96) * mm, "end": v(-43.6, 14) * mm});
            skLineSegment(sketch, "E624.MirrorCS", {"start": v(-33.27, 17.24) * mm, "end": v(-33.42, 17.2) * mm});
            skLineSegment(sketch, "E625.MirrorCS", {"start": v(-36.1, 16.49) * mm, "end": v(-36.25, 16.44) * mm});
            skLineSegment(sketch, "E626.MirrorCS", {"start": v(-35.82, 16.58) * mm, "end": v(-35.85, 16.43) * mm});
            skLineSegment(sketch, "E627.MirrorCS", {"start": v(-20.61, 21.34) * mm, "end": v(-20.76, 21.3) * mm});
            skLineSegment(sketch, "E628.MirrorCS", {"start": v(-53.04, 11.19) * mm, "end": v(-52.9, 11.23) * mm});
            skLineSegment(sketch, "E629.MirrorCS", {"start": v(-45.75, 13.33) * mm, "end": v(-45.9, 13.28) * mm});
            skLineSegment(sketch, "E630.MirrorCS", {"start": v(-25.78, 19.72) * mm, "end": v(-25.67, 19.62) * mm});
            skLineSegment(sketch, "E631.MirrorCS", {"start": v(-27.65, 19.14) * mm, "end": v(-27.5, 19.18) * mm});
            skLineSegment(sketch, "E632.MirrorCS", {"start": v(-50.74, 11.9) * mm, "end": v(-50.63, 11.8) * mm});
            skLineSegment(sketch, "E633.MirrorCS", {"start": v(-28.25, 18.8) * mm, "end": v(-28.1, 18.85) * mm});
            skLineSegment(sketch, "E634.MirrorCS", {"start": v(-35.85, 16.43) * mm, "end": v(-36, 16.38) * mm});
            skLineSegment(sketch, "E635.MirrorCS", {"start": v(-45.72, 13.48) * mm, "end": v(-45.75, 13.33) * mm});
            skLineSegment(sketch, "E636.MirrorCS", {"start": v(-27.67, 18.99) * mm, "end": v(-27.82, 18.94) * mm});
            skLineSegment(sketch, "E637.MirrorCS", {"start": v(-28.36, 18.91) * mm, "end": v(-28.25, 18.8) * mm});
            skLineSegment(sketch, "E638.MirrorCS", {"start": v(-53.93, 10.77) * mm, "end": v(-54.08, 10.72) * mm});
            skLineSegment(sketch, "E639.MirrorCS", {"start": v(-36.43, 16.25) * mm, "end": v(-36.28, 16.3) * mm});
            skLineSegment(sketch, "E640.MirrorCS", {"start": v(-50.89, 11.86) * mm, "end": v(-50.74, 11.9) * mm});
            skLineSegment(sketch, "E641.MirrorCS", {"start": v(-45.58, 13.52) * mm, "end": v(-45.72, 13.48) * mm});
            skLineSegment(sketch, "E642.MirrorCS", {"start": v(-46.33, 13.15) * mm, "end": v(-46.18, 13.2) * mm});
            skLineSegment(sketch, "E643.MirrorCS", {"start": v(-29.4, 18.45) * mm, "end": v(-29.54, 18.4) * mm});
            skLineSegment(sketch, "E644.MirrorCS", {"start": v(-50.92, 11.71) * mm, "end": v(-50.89, 11.86) * mm});
            skLineSegment(sketch, "E645.MirrorCS", {"start": v(-45.04, 13.55) * mm, "end": v(-45.15, 13.66) * mm});
            skLineSegment(sketch, "E646.MirrorCS", {"start": v(-52.78, 11.13) * mm, "end": v(-52.64, 11.17) * mm});
            skLineSegment(sketch, "E647.MirrorCS", {"start": v(-45.15, 13.66) * mm, "end": v(-45.3, 13.61) * mm});
            skLineSegment(sketch, "E648.MirrorCS", {"start": v(-35.57, 16.52) * mm, "end": v(-35.68, 16.62) * mm});
            skLineSegment(sketch, "E649.MirrorCS", {"start": v(-25.92, 19.68) * mm, "end": v(-25.78, 19.72) * mm});
            skLineSegment(sketch, "E650.MirrorCS", {"start": v(-47.04, 12.92) * mm, "end": v(-47.19, 12.88) * mm});
            skLineSegment(sketch, "E651.MirrorCS", {"start": v(-32.81, 17.52) * mm, "end": v(-32.66, 17.57) * mm});
            skLineSegment(sketch, "E652.MirrorCS", {"start": v(-31.26, 17.87) * mm, "end": v(-31.37, 17.97) * mm});
            skLineSegment(sketch, "E653.MirrorCS", {"start": v(-29.37, 18.6) * mm, "end": v(-29.4, 18.45) * mm});
            skLineSegment(sketch, "E654.MirrorCS", {"start": v(-44.86, 13.75) * mm, "end": v(-44.9, 13.6) * mm});
            skLineSegment(sketch, "E655.MirrorCS", {"start": v(-46.61, 13.06) * mm, "end": v(-46.58, 13.2) * mm});
            skLineSegment(sketch, "E656.MirrorCS", {"start": v(-28.54, 18.72) * mm, "end": v(-28.5, 18.87) * mm});
            skLineSegment(sketch, "E657.MirrorCS", {"start": v(-46.15, 13.34) * mm, "end": v(-46, 13.39) * mm});
            skLineSegment(sketch, "E658.MirrorCS", {"start": v(-53.32, 11.1) * mm, "end": v(-53.47, 11.05) * mm});
            skLineSegment(sketch, "E659.MirrorCS", {"start": v(-18.46, 22.01) * mm, "end": v(-18.6, 21.97) * mm});
            skLineSegment(sketch, "E660.MirrorCS", {"start": v(-44.72, 13.8) * mm, "end": v(-44.86, 13.75) * mm});
            skLineSegment(sketch, "E661.MirrorCS", {"start": v(-53.65, 10.86) * mm, "end": v(-53.76, 10.96) * mm});
            skLineSegment(sketch, "E662.MirrorCS", {"start": v(-27.93, 19.05) * mm, "end": v(-27.82, 18.94) * mm});
            skLineSegment(sketch, "E663.MirrorCS", {"start": v(-28.5, 18.87) * mm, "end": v(-28.36, 18.91) * mm});
            skLineSegment(sketch, "E664.MirrorCS", {"start": v(-37.72, 15.84) * mm, "end": v(-37.57, 15.89) * mm});
            skLineSegment(sketch, "E665.MirrorCS", {"start": v(-44.6, 13.69) * mm, "end": v(-44.72, 13.8) * mm});
            skLineSegment(sketch, "E666.MirrorCS", {"start": v(-44.9, 13.6) * mm, "end": v(-45.04, 13.55) * mm});
            skLineSegment(sketch, "E667.MirrorCS", {"start": v(-46.44, 13.25) * mm, "end": v(-46.33, 13.15) * mm});
            skLineSegment(sketch, "E668.MirrorCS", {"start": v(-51.35, 11.58) * mm, "end": v(-51.5, 11.53) * mm});
            skLineSegment(sketch, "E669.MirrorCS", {"start": v(-20.18, 21.47) * mm, "end": v(-20.33, 21.43) * mm});
            skLineSegment(sketch, "E670.MirrorCS", {"start": v(-32.84, 17.37) * mm, "end": v(-32.81, 17.52) * mm});
            skLineSegment(sketch, "E671.MirrorCS", {"start": v(-32.66, 17.57) * mm, "end": v(-32.55, 17.46) * mm});
            skLineSegment(sketch, "E672.MirrorCS", {"start": v(-29.22, 18.64) * mm, "end": v(-29.37, 18.6) * mm});
            skLineSegment(sketch, "E673.MirrorCS", {"start": v(-44.03, 13.87) * mm, "end": v(-44, 14.02) * mm});
            skLineSegment(sketch, "E674.MirrorCS", {"start": v(-46.58, 13.2) * mm, "end": v(-46.44, 13.25) * mm});
            skLineSegment(sketch, "E675.MirrorCS", {"start": v(-46.87, 13.12) * mm, "end": v(-46.76, 13.01) * mm});
            skLineSegment(sketch, "E676.MirrorCS", {"start": v(-24.23, 20.07) * mm, "end": v(-24.38, 20.02) * mm});
            skLineSegment(sketch, "E677.MirrorCS", {"start": v(-33.1, 17.43) * mm, "end": v(-32.99, 17.33) * mm});
            skLineSegment(sketch, "E678.MirrorCS", {"start": v(-46, 13.39) * mm, "end": v(-45.9, 13.28) * mm});
            skLineSegment(sketch, "E679.MirrorCS", {"start": v(-47.62, 12.74) * mm, "end": v(-47.73, 12.85) * mm});
            skLineSegment(sketch, "E680.MirrorCS", {"start": v(-36.61, 16.33) * mm, "end": v(-36.54, 16.1) * mm, "construction": true});
            skLineSegment(sketch, "E681.MirrorCS", {"start": v(-36.54, 16.35) * mm, "end": v(-36.43, 16.25) * mm});
            skLineSegment(sketch, "E682.MirrorCS", {"start": v(-25.95, 19.53) * mm, "end": v(-25.92, 19.68) * mm});
            skLineSegment(sketch, "E683.MirrorCS", {"start": v(-28.08, 19) * mm, "end": v(-27.93, 19.05) * mm});
            skLineSegment(sketch, "E684.MirrorCS", {"start": v(-44, 14.02) * mm, "end": v(-43.86, 14.06) * mm});
            skLineSegment(sketch, "E685.MirrorCS", {"start": v(-47.47, 12.79) * mm, "end": v(-47.62, 12.74) * mm});
            skLineSegment(sketch, "E686.MirrorCS", {"start": v(-47.3, 12.98) * mm, "end": v(-47.44, 12.94) * mm});
            skLineSegment(sketch, "E687.MirrorCS", {"start": v(-47.44, 12.94) * mm, "end": v(-47.47, 12.79) * mm});
            skLineSegment(sketch, "E688.MirrorCS", {"start": v(-39.73, 15.22) * mm, "end": v(-39.7, 15.36) * mm});
            skLineSegment(sketch, "E689.MirrorCS", {"start": v(-33.24, 17.39) * mm, "end": v(-33.1, 17.43) * mm});
            skLineSegment(sketch, "E690.MirrorCS", {"start": v(-32.99, 17.33) * mm, "end": v(-32.84, 17.37) * mm});
            skLineSegment(sketch, "E691.MirrorCS", {"start": v(-45.65, 13.5) * mm, "end": v(-45.56, 13.2) * mm, "construction": true});
            skLineSegment(sketch, "E692.MirrorCS", {"start": v(-47.01, 13.07) * mm, "end": v(-46.87, 13.12) * mm});
            skLineSegment(sketch, "E693.MirrorCS", {"start": v(-44.18, 13.82) * mm, "end": v(-44.03, 13.87) * mm});
            skLineSegment(sketch, "E694.MirrorCS", {"start": v(-53.07, 11.04) * mm, "end": v(-53.04, 11.19) * mm});
            skLineSegment(sketch, "E695.MirrorCS", {"start": v(-18.53, 22) * mm, "end": v(-18.46, 21.75) * mm, "construction": true});
            skLineSegment(sketch, "E696.MirrorCS", {"start": v(-37.57, 15.89) * mm, "end": v(-37.54, 16.04) * mm});
            skLineSegment(sketch, "E697.MirrorCS", {"start": v(-51.35, 11.58) * mm, "end": v(-51.32, 11.73) * mm});
            skLineSegment(sketch, "E698.MirrorCS", {"start": v(-39.87, 15.17) * mm, "end": v(-39.98, 15.28) * mm});
            skLineSegment(sketch, "E699.MirrorCS", {"start": v(-46.76, 13.01) * mm, "end": v(-46.61, 13.06) * mm});
            skLineSegment(sketch, "E700.MirrorCS", {"start": v(-40.13, 15.23) * mm, "end": v(-40.16, 15.08) * mm});
            skLineSegment(sketch, "E701.MirrorCS", {"start": v(-40.16, 15.08) * mm, "end": v(-40.3, 15.04) * mm});
            skLineSegment(sketch, "E702.MirrorCS", {"start": v(-51.06, 11.67) * mm, "end": v(-50.92, 11.71) * mm});
            skLineSegment(sketch, "E703.MirrorCS", {"start": v(-39.98, 15.28) * mm, "end": v(-40.13, 15.23) * mm});
            skLineSegment(sketch, "E704.MirrorCS", {"start": v(-47.19, 12.88) * mm, "end": v(-47.3, 12.98) * mm});
            skLineSegment(sketch, "E705.MirrorCS", {"start": v(-24.23, 20.07) * mm, "end": v(-24.2, 20.22) * mm});
            skLineSegment(sketch, "E706.MirrorCS", {"start": v(-40.3, 15.04) * mm, "end": v(-40.41, 15.14) * mm});
            skLineSegment(sketch, "E707.MirrorCS", {"start": v(-51.17, 11.77) * mm, "end": v(-51.06, 11.67) * mm});
            skLineSegment(sketch, "E708.MirrorCS", {"start": v(-23.8, 20.2) * mm, "end": v(-23.77, 20.35) * mm});
            skLineSegment(sketch, "E709.MirrorCS", {"start": v(-37.98, 15.9) * mm, "end": v(-37.83, 15.95) * mm});
            skLineSegment(sketch, "E710.MirrorCS", {"start": v(-26.38, 19.4) * mm, "end": v(-26.53, 19.35) * mm});
            skLineSegment(sketch, "E711.MirrorCS", {"start": v(-26.1, 19.48) * mm, "end": v(-25.95, 19.53) * mm});
            skLineSegment(sketch, "E712.MirrorCS", {"start": v(-30.83, 18) * mm, "end": v(-30.94, 18.1) * mm});
            skLineSegment(sketch, "E713.MirrorCS", {"start": v(-19.75, 21.6) * mm, "end": v(-19.64, 21.5) * mm});
            skLineSegment(sketch, "E714.MirrorCS", {"start": v(-31.12, 17.91) * mm, "end": v(-31.26, 17.87) * mm});
            skLineSegment(sketch, "E715.MirrorCS", {"start": v(-47.04, 12.92) * mm, "end": v(-47.01, 13.07) * mm});
            skLineSegment(sketch, "E716.MirrorCS", {"start": v(-18.35, 21.9) * mm, "end": v(-18.46, 22.01) * mm});
            skLineSegment(sketch, "E717.MirrorCS", {"start": v(-24.06, 20.26) * mm, "end": v(-23.95, 20.16) * mm});
            skLineSegment(sketch, "E718.MirrorCS", {"start": v(-28.97, 18.58) * mm, "end": v(-28.94, 18.73) * mm});
            skLineSegment(sketch, "E719.MirrorCS", {"start": v(-38, 15.75) * mm, "end": v(-37.98, 15.9) * mm});
            skLineSegment(sketch, "E720.MirrorCS", {"start": v(-19.93, 21.41) * mm, "end": v(-20.07, 21.37) * mm});
            skLineSegment(sketch, "E721.MirrorCS", {"start": v(-53.21, 11) * mm, "end": v(-53.07, 11.04) * mm});
            skLineSegment(sketch, "E722.MirrorCS", {"start": v(-30.69, 18.05) * mm, "end": v(-30.66, 18.2) * mm});
            skLineSegment(sketch, "E723.MirrorCS", {"start": v(-20.07, 21.37) * mm, "end": v(-20.18, 21.47) * mm});
            skLineSegment(sketch, "E724.MirrorCS", {"start": v(-37.83, 15.95) * mm, "end": v(-37.72, 15.84) * mm});
            skLineSegment(sketch, "E725.MirrorCS", {"start": v(-53.5, 10.9) * mm, "end": v(-53.65, 10.86) * mm});
            skLineSegment(sketch, "E726.MirrorCS", {"start": v(-49.34, 12.2) * mm, "end": v(-49.45, 12.31) * mm});
            skLineSegment(sketch, "E727.MirrorCS", {"start": v(-51.32, 11.73) * mm, "end": v(-51.17, 11.77) * mm});
            skLineSegment(sketch, "E728.MirrorCS", {"start": v(-42.56, 14.47) * mm, "end": v(-42.7, 14.42) * mm});
            skLineSegment(sketch, "E729.MirrorCS", {"start": v(-42.13, 14.6) * mm, "end": v(-42.02, 14.5) * mm});
            skLineSegment(sketch, "E730.MirrorCS", {"start": v(-53.21, 11) * mm, "end": v(-53.32, 11.1) * mm});
            skLineSegment(sketch, "E731.MirrorCS", {"start": v(-39.87, 15.17) * mm, "end": v(-39.73, 15.22) * mm});
            skLineSegment(sketch, "E732.MirrorCS", {"start": v(-53.47, 11.05) * mm, "end": v(-53.5, 10.9) * mm});
            skLineSegment(sketch, "E733.MirrorCS", {"start": v(-29.11, 18.54) * mm, "end": v(-29.22, 18.64) * mm});
            skLineSegment(sketch, "E734.MirrorCS", {"start": v(-48.91, 12.34) * mm, "end": v(-48.77, 12.39) * mm});
            skLineSegment(sketch, "E735.MirrorCS", {"start": v(-19.93, 21.41) * mm, "end": v(-19.9, 21.56) * mm});
            skLineSegment(sketch, "E736.MirrorCS", {"start": v(-42.02, 14.5) * mm, "end": v(-41.88, 14.54) * mm});
            skLineSegment(sketch, "E737.MirrorCS", {"start": v(-44.18, 13.82) * mm, "end": v(-44.29, 13.93) * mm});
            skLineSegment(sketch, "E738.MirrorCS", {"start": v(-28.97, 18.58) * mm, "end": v(-29.11, 18.54) * mm});
            skLineSegment(sketch, "E739.MirrorCS", {"start": v(-35.42, 16.56) * mm, "end": v(-35.57, 16.52) * mm});
            skLineSegment(sketch, "E740.MirrorCS", {"start": v(-21.8, 20.83) * mm, "end": v(-21.65, 20.88) * mm});
            skLineSegment(sketch, "E741.MirrorCS", {"start": v(-49.17, 12.4) * mm, "end": v(-49.2, 12.25) * mm});
            skLineSegment(sketch, "E742.MirrorCS", {"start": v(-35.14, 16.65) * mm, "end": v(-35.25, 16.76) * mm});
            skLineSegment(sketch, "E743.MirrorCS", {"start": v(-26.64, 19.45) * mm, "end": v(-26.78, 19.4) * mm});
            skLineSegment(sketch, "E744.MirrorCS", {"start": v(-23.95, 20.16) * mm, "end": v(-23.8, 20.2) * mm});
            skLineSegment(sketch, "E745.MirrorCS", {"start": v(-44.29, 13.93) * mm, "end": v(-44.43, 13.88) * mm});
            skLineSegment(sketch, "E746.MirrorCS", {"start": v(-26.2, 19.59) * mm, "end": v(-26.35, 19.54) * mm});
            skLineSegment(sketch, "E747.MirrorCS", {"start": v(-22.08, 20.74) * mm, "end": v(-22.22, 20.7) * mm});
            skLineSegment(sketch, "E748.MirrorCS", {"start": v(-44.46, 13.73) * mm, "end": v(-44.6, 13.69) * mm});
            skLineSegment(sketch, "E749.MirrorCS", {"start": v(-49.02, 12.45) * mm, "end": v(-49.17, 12.4) * mm});
            skLineSegment(sketch, "E750.MirrorCS", {"start": v(-38.15, 15.7) * mm, "end": v(-38.26, 15.81) * mm});
            skLineSegment(sketch, "E751.MirrorCS", {"start": v(-30.94, 18.1) * mm, "end": v(-31.09, 18.06) * mm});
            skLineSegment(sketch, "E752.MirrorCS", {"start": v(-28.68, 18.67) * mm, "end": v(-28.54, 18.72) * mm});
            skLineSegment(sketch, "E753.MirrorCS", {"start": v(-30.83, 18) * mm, "end": v(-30.69, 18.05) * mm});
            skLineSegment(sketch, "E754.MirrorCS", {"start": v(-38, 15.75) * mm, "end": v(-38.15, 15.7) * mm});
            skLineSegment(sketch, "E755.MirrorCS", {"start": v(-35.4, 16.71) * mm, "end": v(-35.42, 16.56) * mm});
            skLineSegment(sketch, "E756.MirrorCS", {"start": v(-24.2, 20.22) * mm, "end": v(-24.06, 20.26) * mm});
            skLineSegment(sketch, "E757.MirrorCS", {"start": v(-42.3, 14.4) * mm, "end": v(-42.28, 14.56) * mm});
            skLineSegment(sketch, "E758.MirrorCS", {"start": v(-49.2, 12.25) * mm, "end": v(-49.34, 12.2) * mm});
            skLineSegment(sketch, "E759.MirrorCS", {"start": v(-31.09, 18.06) * mm, "end": v(-31.12, 17.91) * mm});
            skLineSegment(sketch, "E760.MirrorCS", {"start": v(-21.65, 20.88) * mm, "end": v(-21.62, 21.03) * mm});
            skLineSegment(sketch, "E761.MirrorCS", {"start": v(-21.9, 20.94) * mm, "end": v(-22.05, 20.9) * mm});
            skLineSegment(sketch, "E762.MirrorCS", {"start": v(-28.8, 18.78) * mm, "end": v(-28.68, 18.67) * mm});
            skLineSegment(sketch, "E763.MirrorCS", {"start": v(-21.8, 20.83) * mm, "end": v(-21.9, 20.94) * mm});
            skLineSegment(sketch, "E764.MirrorCS", {"start": v(-19.64, 21.5) * mm, "end": v(-19.5, 21.55) * mm});
            skLineSegment(sketch, "E765.MirrorCS", {"start": v(-35.25, 16.76) * mm, "end": v(-35.4, 16.71) * mm});
            skLineSegment(sketch, "E766.MirrorCS", {"start": v(-22.05, 20.9) * mm, "end": v(-22.08, 20.74) * mm});
            skLineSegment(sketch, "E767.MirrorCS", {"start": v(-35.14, 16.65) * mm, "end": v(-35, 16.7) * mm});
            skLineSegment(sketch, "E768.MirrorCS", {"start": v(-48.91, 12.34) * mm, "end": v(-49.02, 12.45) * mm});
            skLineSegment(sketch, "E769.MirrorCS", {"start": v(-26.35, 19.54) * mm, "end": v(-26.38, 19.4) * mm});
            skLineSegment(sketch, "E770.MirrorCS", {"start": v(-26.1, 19.48) * mm, "end": v(-26.2, 19.59) * mm});
            skLineSegment(sketch, "E771.MirrorCS", {"start": v(-44.43, 13.88) * mm, "end": v(-44.46, 13.73) * mm});
            skLineSegment(sketch, "E772.MirrorCS", {"start": v(-42.45, 14.36) * mm, "end": v(-42.56, 14.47) * mm});
            skLineSegment(sketch, "E773.MirrorCS", {"start": v(-26.53, 19.35) * mm, "end": v(-26.64, 19.45) * mm});
            skLineSegment(sketch, "E774.MirrorCS", {"start": v(-28.94, 18.73) * mm, "end": v(-28.8, 18.78) * mm});
            skLineSegment(sketch, "E775.MirrorCS", {"start": v(-19.9, 21.56) * mm, "end": v(-19.75, 21.6) * mm});
            skLineSegment(sketch, "E776.MirrorCS", {"start": v(-42.3, 14.4) * mm, "end": v(-42.45, 14.36) * mm});
            skLineSegment(sketch, "E777.MirrorCS", {"start": v(-42.28, 14.56) * mm, "end": v(-42.13, 14.6) * mm});
            skLineSegment(sketch, "E778", {"start": v(-81.73, 2.2) * mm, "end": v(-81.62, 2.1) * mm});
            skLineSegment(sketch, "E779", {"start": v(-63.8, 7.82) * mm, "end": v(-63.83, 7.67) * mm});
            skLineSegment(sketch, "E780", {"start": v(-27.67, 18.99) * mm, "end": v(-27.65, 19.14) * mm});
            skLineSegment(sketch, "E781", {"start": v(-45.58, 13.52) * mm, "end": v(-45.47, 13.42) * mm});
            skSolve(sketch);
        }
        {
            var Q0;
            {var subQ0=sQuery(id+"F10.wireOp",EDGE,"E35");Q0=makeQuery(id+"F10.imprint","IMPRINT",FACE,{"disambiguationData":[TD([[makeQuery(id+"F10.imprint","IMPRINT",EDGE,{"derivedFrom":subQ0}),-1.0]])]});}
            var Q1;
            {var subQ0=sQuery(id+"F10.wireOp",EDGE,"E39.MirrorCS");Q1=makeQuery(id+"F10.imprint","IMPRINT",FACE,{"disambiguationData":[TD([[makeQuery(id+"F10.imprint","IMPRINT",EDGE,{"derivedFrom":subQ0}),1.0]])]});}
            var Q2;
            {var subQ0=sQuery(id+"F10.wireOp",EDGE,"E44.MirrorCS");Q2=makeQuery(id+"F10.imprint","IMPRINT",FACE,{"disambiguationData":[TD([[makeQuery(id+"F10.imprint","IMPRINT",EDGE,{"derivedFrom":subQ0}),1.0]])]});}
            var Q3;
            {var subQ0=sQuery(id+"F10.wireOp",EDGE,"E47.MirrorCS");Q3=makeQuery(id+"F10.imprint","IMPRINT",FACE,{"disambiguationData":[TD([[makeQuery(id+"F10.imprint","IMPRINT",EDGE,{"derivedFrom":subQ0}),1.0]])]});}
            var Q4;
            {var subQ0=sQuery(id+"F10.wireOp",EDGE,"E55.MirrorCS");Q4=makeQuery(id+"F10.imprint","IMPRINT",FACE,{"disambiguationData":[TD([[makeQuery(id+"F10.imprint","IMPRINT",EDGE,{"derivedFrom":subQ0}),-1.0]])]});}
            var Q5;
            {var subQ0=sQuery(id+"F10.wireOp",EDGE,"E52.MirrorCS");Q5=makeQuery(id+"F10.imprint","IMPRINT",FACE,{"disambiguationData":[TD([[makeQuery(id+"F10.imprint","IMPRINT",EDGE,{"derivedFrom":subQ0}),1.0]])]});}
            var Q6;
            {var subQ0=sQuery(id+"F10.wireOp",EDGE,"E64.MirrorCS");Q6=makeQuery(id+"F10.imprint","IMPRINT",FACE,{"disambiguationData":[TD([[makeQuery(id+"F10.imprint","IMPRINT",EDGE,{"derivedFrom":subQ0}),-1.0]])]});}
            var Q7;
            Q7=makeQuery(id+"F10.imprint","IMPRINT",FACE,{"disambiguationData":[TD([[makeQuery(id+"F10.imprint","IMPRINT",EDGE,{"derivedFrom":sQuery(id+"F10.wireOp",EDGE,"E77.MirrorCS")}),1.0]])]});
            var Q8;
            Q8=makeQuery(id+"F10.imprint","IMPRINT",FACE,{"disambiguationData":[TD([[makeQuery(id+"F10.imprint","IMPRINT",EDGE,{"derivedFrom":sQuery(id+"F10.wireOp",EDGE,"E68.MirrorCS")}),-1.0]])]});
            var Q9;
            {var subQ0=sQuery(id+"F10.wireOp",EDGE,"E69.MirrorCS");Q9=makeQuery(id+"F10.imprint","IMPRINT",FACE,{"disambiguationData":[TD([[makeQuery(id+"F10.imprint","IMPRINT",EDGE,{"derivedFrom":subQ0}),-1.0]])]});}
            var Q10;
            {var subQ0=sQuery(id+"F10.wireOp",EDGE,"E80.MirrorCS");Q10=makeQuery(id+"F10.imprint","IMPRINT",FACE,{"disambiguationData":[TD([[makeQuery(id+"F10.imprint","IMPRINT",EDGE,{"derivedFrom":subQ0}),-1.0]])]});}
            var Q11;
            Q11=makeQuery(id+"F10.imprint","IMPRINT",FACE,{"disambiguationData":[TD([[makeQuery(id+"F10.imprint","IMPRINT",EDGE,{"derivedFrom":sQuery(id+"F10.wireOp",EDGE,"E73.MirrorCS")}),1.0]])]});
            var Q12;
            Q12=makeQuery(id+"F10.imprint","IMPRINT",FACE,{"disambiguationData":[TD([[makeQuery(id+"F10.imprint","IMPRINT",EDGE,{"derivedFrom":sQuery(id+"F10.wireOp",EDGE,"E89.MirrorCS")}),1.0]])]});
            var Q13;
            Q13=makeQuery(id+"F10.imprint","IMPRINT",FACE,{"disambiguationData":[TD([[makeQuery(id+"F10.imprint","IMPRINT",EDGE,{"derivedFrom":sQuery(id+"F10.wireOp",EDGE,"E100.MirrorCS")}),1.0]])]});
            var Q14;
            Q14=makeQuery(id+"F10.imprint","IMPRINT",FACE,{"disambiguationData":[TD([[makeQuery(id+"F10.imprint","IMPRINT",EDGE,{"derivedFrom":sQuery(id+"F10.wireOp",EDGE,"E114.MirrorCS")}),-1.0]])]});
            var Q15;
            Q15=makeQuery(id+"F10.imprint","IMPRINT",FACE,{"disambiguationData":[TD([[makeQuery(id+"F10.imprint","IMPRINT",EDGE,{"derivedFrom":sQuery(id+"F10.wireOp",EDGE,"E93.MirrorCS")}),-1.0]])]});
            var Q16;
            Q16=makeQuery(id+"F10.imprint","IMPRINT",FACE,{"disambiguationData":[TD([[makeQuery(id+"F10.imprint","IMPRINT",EDGE,{"derivedFrom":sQuery(id+"F10.wireOp",EDGE,"E99.MirrorCS")}),1.0]])]});
            var Q17;
            {var subQ0=sQuery(id+"F10.wireOp",EDGE,"E109.MirrorCS");Q17=makeQuery(id+"F10.imprint","IMPRINT",FACE,{"disambiguationData":[TD([[makeQuery(id+"F10.imprint","IMPRINT",EDGE,{"derivedFrom":subQ0}),1.0]])]});}
            var Q18;
            Q18=makeQuery(id+"F10.imprint","IMPRINT",FACE,{"disambiguationData":[TD([[makeQuery(id+"F10.imprint","IMPRINT",EDGE,{"derivedFrom":sQuery(id+"F10.wireOp",EDGE,"E102.MirrorCS")}),-1.0]])]});
            var Q19;
            Q19=makeQuery(id+"F10.imprint","IMPRINT",FACE,{"disambiguationData":[TD([[makeQuery(id+"F10.imprint","IMPRINT",EDGE,{"derivedFrom":sQuery(id+"F10.wireOp",EDGE,"E92.MirrorCS")}),-1.0]])]});
            var Q20;
            Q20=makeQuery(id+"F10.imprint","IMPRINT",FACE,{"disambiguationData":[TD([[makeQuery(id+"F10.imprint","IMPRINT",EDGE,{"derivedFrom":sQuery(id+"F10.wireOp",EDGE,"E108.MirrorCS")}),-1.0]])]});
            var Q21;
            {var subQ0=sQuery(id+"F10.wireOp",EDGE,"E147.MirrorCS");Q21=makeQuery(id+"F10.imprint","IMPRINT",FACE,{"disambiguationData":[TD([[makeQuery(id+"F10.imprint","IMPRINT",EDGE,{"derivedFrom":subQ0}),1.0]])]});}
            var Q22;
            {var subQ0=sQuery(id+"F10.wireOp",EDGE,"E166.MirrorCS");Q22=makeQuery(id+"F10.imprint","IMPRINT",FACE,{"disambiguationData":[TD([[makeQuery(id+"F10.imprint","IMPRINT",EDGE,{"derivedFrom":subQ0}),1.0]])]});}
            var Q23;
            {var subQ0=sQuery(id+"F10.wireOp",EDGE,"E171.MirrorCS");Q23=makeQuery(id+"F10.imprint","IMPRINT",FACE,{"disambiguationData":[TD([[makeQuery(id+"F10.imprint","IMPRINT",EDGE,{"derivedFrom":subQ0}),1.0]])]});}
            var Q24;
            Q24=makeQuery(id+"F10.imprint","IMPRINT",FACE,{"disambiguationData":[TD([[makeQuery(id+"F10.imprint","IMPRINT",EDGE,{"derivedFrom":sQuery(id+"F10.wireOp",EDGE,"E162.MirrorCS")}),-1.0]])]});
            var Q25;
            {var subQ0=sQuery(id+"F10.wireOp",EDGE,"E138.MirrorCS");Q25=makeQuery(id+"F10.imprint","IMPRINT",FACE,{"disambiguationData":[TD([[makeQuery(id+"F10.imprint","IMPRINT",EDGE,{"derivedFrom":subQ0}),1.0]])]});}
            var Q26;
            {var subQ0=sQuery(id+"F10.wireOp",EDGE,"E135.MirrorCS");Q26=makeQuery(id+"F10.imprint","IMPRINT",FACE,{"disambiguationData":[TD([[makeQuery(id+"F10.imprint","IMPRINT",EDGE,{"derivedFrom":subQ0}),-1.0]])]});}
            var Q27;
            {var subQ0=sQuery(id+"F10.wireOp",EDGE,"E158.MirrorCS");Q27=makeQuery(id+"F10.imprint","IMPRINT",FACE,{"disambiguationData":[TD([[makeQuery(id+"F10.imprint","IMPRINT",EDGE,{"derivedFrom":subQ0}),1.0]])]});}
            var Q28;
            Q28=makeQuery(id+"F10.imprint","IMPRINT",FACE,{"disambiguationData":[TD([[makeQuery(id+"F10.imprint","IMPRINT",EDGE,{"derivedFrom":sQuery(id+"F10.wireOp",EDGE,"E181.MirrorCS")}),-1.0]])]});
            var Q29;
            Q29=makeQuery(id+"F10.imprint","IMPRINT",FACE,{"disambiguationData":[TD([[makeQuery(id+"F10.imprint","IMPRINT",EDGE,{"derivedFrom":sQuery(id+"F10.wireOp",EDGE,"E155.MirrorCS")}),-1.0]])]});
            var Q30;
            {var subQ0=sQuery(id+"F10.wireOp",EDGE,"E131.MirrorCS");Q30=makeQuery(id+"F10.imprint","IMPRINT",FACE,{"disambiguationData":[TD([[makeQuery(id+"F10.imprint","IMPRINT",EDGE,{"derivedFrom":subQ0}),1.0]])]});}
            var Q31;
            {var subQ0=sQuery(id+"F10.wireOp",EDGE,"E145.MirrorCS");Q31=makeQuery(id+"F10.imprint","IMPRINT",FACE,{"disambiguationData":[TD([[makeQuery(id+"F10.imprint","IMPRINT",EDGE,{"derivedFrom":subQ0}),1.0]])]});}
            var Q32;
            {var subQ0=sQuery(id+"F10.wireOp",EDGE,"E178.MirrorCS");Q32=makeQuery(id+"F10.imprint","IMPRINT",FACE,{"disambiguationData":[TD([[makeQuery(id+"F10.imprint","IMPRINT",EDGE,{"derivedFrom":subQ0}),1.0]])]});}
            var Q33;
            Q33=makeQuery(id+"F10.imprint","IMPRINT",FACE,{"disambiguationData":[TD([[makeQuery(id+"F10.imprint","IMPRINT",EDGE,{"derivedFrom":sQuery(id+"F10.wireOp",EDGE,"E186.MirrorCS")}),1.0]])]});
            var Q34;
            {var subQ0=sQuery(id+"F10.wireOp",EDGE,"E185.MirrorCS");Q34=makeQuery(id+"F10.imprint","IMPRINT",FACE,{"disambiguationData":[TD([[makeQuery(id+"F10.imprint","IMPRINT",EDGE,{"derivedFrom":subQ0}),-1.0]])]});}
            var Q35;
            {var subQ0=sQuery(id+"F10.wireOp",EDGE,"E140.MirrorCS");Q35=makeQuery(id+"F10.imprint","IMPRINT",FACE,{"disambiguationData":[TD([[makeQuery(id+"F10.imprint","IMPRINT",EDGE,{"derivedFrom":subQ0}),1.0]])]});}
            var Q36;
            {var subQ0=sQuery(id+"F10.wireOp",EDGE,"E139.MirrorCS");Q36=makeQuery(id+"F10.imprint","IMPRINT",FACE,{"disambiguationData":[TD([[makeQuery(id+"F10.imprint","IMPRINT",EDGE,{"derivedFrom":subQ0}),-1.0]])]});}
            var Q37;
            {var subQ0=sQuery(id+"F10.wireOp",EDGE,"E164.MirrorCS");Q37=makeQuery(id+"F10.imprint","IMPRINT",FACE,{"disambiguationData":[TD([[makeQuery(id+"F10.imprint","IMPRINT",EDGE,{"derivedFrom":subQ0}),1.0]])]});}
            var Q38;
            {var subQ0=sQuery(id+"F10.wireOp",EDGE,"E167.MirrorCS");Q38=makeQuery(id+"F10.imprint","IMPRINT",FACE,{"disambiguationData":[TD([[makeQuery(id+"F10.imprint","IMPRINT",EDGE,{"derivedFrom":subQ0}),-1.0]])]});}
            var Q39;
            {var subQ0=sQuery(id+"F10.wireOp",EDGE,"E239.MirrorCS");Q39=makeQuery(id+"F10.imprint","IMPRINT",FACE,{"disambiguationData":[TD([[makeQuery(id+"F10.imprint","IMPRINT",EDGE,{"derivedFrom":subQ0}),-1.0]])]});}
            var Q40;
            Q40=makeQuery(id+"F10.imprint","IMPRINT",FACE,{"disambiguationData":[TD([[makeQuery(id+"F10.imprint","IMPRINT",EDGE,{"derivedFrom":sQuery(id+"F10.wireOp",EDGE,"E208.MirrorCS")}),1.0]])]});
            var Q41;
            {var subQ0=sQuery(id+"F10.wireOp",EDGE,"E142.MirrorCS");Q41=makeQuery(id+"F10.imprint","IMPRINT",FACE,{"disambiguationData":[TD([[makeQuery(id+"F10.imprint","IMPRINT",EDGE,{"derivedFrom":subQ0}),1.0]])]});}
            var Q42;
            {var subQ0=sQuery(id+"F10.wireOp",EDGE,"E200.MirrorCS");Q42=makeQuery(id+"F10.imprint","IMPRINT",FACE,{"disambiguationData":[TD([[makeQuery(id+"F10.imprint","IMPRINT",EDGE,{"derivedFrom":subQ0}),-1.0]])]});}
            var Q43;
            Q43=makeQuery(id+"F10.imprint","IMPRINT",FACE,{"disambiguationData":[TD([[makeQuery(id+"F10.imprint","IMPRINT",EDGE,{"derivedFrom":sQuery(id+"F10.wireOp",EDGE,"E329.MirrorCS")}),1.0]])]});
            var Q44;
            {var subQ0=sQuery(id+"F10.wireOp",EDGE,"E335.MirrorCS");Q44=makeQuery(id+"F10.imprint","IMPRINT",FACE,{"disambiguationData":[TD([[makeQuery(id+"F10.imprint","IMPRINT",EDGE,{"derivedFrom":subQ0}),1.0]])]});}
            var Q45;
            {var subQ0=sQuery(id+"F10.wireOp",EDGE,"E323.MirrorCS");Q45=makeQuery(id+"F10.imprint","IMPRINT",FACE,{"disambiguationData":[TD([[makeQuery(id+"F10.imprint","IMPRINT",EDGE,{"derivedFrom":subQ0}),-1.0]])]});}
            var Q46;
            {var subQ0=sQuery(id+"F10.wireOp",EDGE,"E245.MirrorCS");Q46=makeQuery(id+"F10.imprint","IMPRINT",FACE,{"disambiguationData":[TD([[makeQuery(id+"F10.imprint","IMPRINT",EDGE,{"derivedFrom":subQ0}),1.0]])]});}
            var Q47;
            Q47=makeQuery(id+"F10.imprint","IMPRINT",FACE,{"disambiguationData":[TD([[makeQuery(id+"F10.imprint","IMPRINT",EDGE,{"derivedFrom":sQuery(id+"F10.wireOp",EDGE,"E247.MirrorCS")}),1.0]])]});
            var Q48;
            {var subQ0=sQuery(id+"F10.wireOp",EDGE,"E328.MirrorCS");Q48=makeQuery(id+"F10.imprint","IMPRINT",FACE,{"disambiguationData":[TD([[makeQuery(id+"F10.imprint","IMPRINT",EDGE,{"derivedFrom":subQ0}),1.0]])]});}
            var Q49;
            Q49=makeQuery(id+"F10.imprint","IMPRINT",FACE,{"disambiguationData":[TD([[makeQuery(id+"F10.imprint","IMPRINT",EDGE,{"derivedFrom":sQuery(id+"F10.wireOp",EDGE,"E324.MirrorCS")}),-1.0]])]});
            var Q50;
            Q50=makeQuery(id+"F10.imprint","IMPRINT",FACE,{"disambiguationData":[TD([[makeQuery(id+"F10.imprint","IMPRINT",EDGE,{"derivedFrom":sQuery(id+"F10.wireOp",EDGE,"E371.MirrorCS")}),-1.0]])]});
            var Q51;
            {var subQ0=sQuery(id+"F10.wireOp",EDGE,"E274.MirrorCS");Q51=makeQuery(id+"F10.imprint","IMPRINT",FACE,{"disambiguationData":[TD([[makeQuery(id+"F10.imprint","IMPRINT",EDGE,{"derivedFrom":subQ0}),-1.0]])]});}
            var Q52;
            {var subQ0=sQuery(id+"F10.wireOp",EDGE,"E227.MirrorCS");Q52=makeQuery(id+"F10.imprint","IMPRINT",FACE,{"disambiguationData":[TD([[makeQuery(id+"F10.imprint","IMPRINT",EDGE,{"derivedFrom":subQ0}),-1.0]])]});}
            var Q53;
            {var subQ0=sQuery(id+"F10.wireOp",EDGE,"E316.MirrorCS");Q53=makeQuery(id+"F10.imprint","IMPRINT",FACE,{"disambiguationData":[TD([[makeQuery(id+"F10.imprint","IMPRINT",EDGE,{"derivedFrom":subQ0}),1.0]])]});}
            var Q54;
            Q54=makeQuery(id+"F10.imprint","IMPRINT",FACE,{"disambiguationData":[TD([[makeQuery(id+"F10.imprint","IMPRINT",EDGE,{"derivedFrom":sQuery(id+"F10.wireOp",EDGE,"E355.MirrorCS")}),1.0]])]});
            var Q55;
            {var subQ0=sQuery(id+"F10.wireOp",EDGE,"E353.MirrorCS");Q55=makeQuery(id+"F10.imprint","IMPRINT",FACE,{"disambiguationData":[TD([[makeQuery(id+"F10.imprint","IMPRINT",EDGE,{"derivedFrom":subQ0}),-1.0]])]});}
            var Q56;
            Q56=makeQuery(id+"F10.imprint","IMPRINT",FACE,{"disambiguationData":[TD([[makeQuery(id+"F10.imprint","IMPRINT",EDGE,{"derivedFrom":sQuery(id+"F10.wireOp",EDGE,"E241.MirrorCS")}),-1.0]])]});
            var Q57;
            Q57=makeQuery(id+"F10.imprint","IMPRINT",FACE,{"disambiguationData":[TD([[makeQuery(id+"F10.imprint","IMPRINT",EDGE,{"derivedFrom":sQuery(id+"F10.wireOp",EDGE,"E267.MirrorCS")}),1.0]])]});
            var Q58;
            {var subQ0=sQuery(id+"F10.wireOp",EDGE,"E313.MirrorCS");Q58=makeQuery(id+"F10.imprint","IMPRINT",FACE,{"disambiguationData":[TD([[makeQuery(id+"F10.imprint","IMPRINT",EDGE,{"derivedFrom":subQ0}),1.0]])]});}
            var Q59;
            {var subQ0=sQuery(id+"F10.wireOp",EDGE,"E351.MirrorCS");Q59=makeQuery(id+"F10.imprint","IMPRINT",FACE,{"disambiguationData":[TD([[makeQuery(id+"F10.imprint","IMPRINT",EDGE,{"derivedFrom":subQ0}),-1.0]])]});}
            var Q60;
            {var subQ0=sQuery(id+"F10.wireOp",EDGE,"E345.MirrorCS");Q60=makeQuery(id+"F10.imprint","IMPRINT",FACE,{"disambiguationData":[TD([[makeQuery(id+"F10.imprint","IMPRINT",EDGE,{"derivedFrom":subQ0}),-1.0]])]});}
            var Q61;
            {var subQ0=sQuery(id+"F10.wireOp",EDGE,"E268.MirrorCS");Q61=makeQuery(id+"F10.imprint","IMPRINT",FACE,{"disambiguationData":[TD([[makeQuery(id+"F10.imprint","IMPRINT",EDGE,{"derivedFrom":subQ0}),-1.0]])]});}
            var Q62;
            {var subQ0=sQuery(id+"F10.wireOp",EDGE,"E285.MirrorCS");Q62=makeQuery(id+"F10.imprint","IMPRINT",FACE,{"disambiguationData":[TD([[makeQuery(id+"F10.imprint","IMPRINT",EDGE,{"derivedFrom":subQ0}),1.0]])]});}
            var Q63;
            Q63=makeQuery(id+"F10.imprint","IMPRINT",FACE,{"disambiguationData":[TD([[makeQuery(id+"F10.imprint","IMPRINT",EDGE,{"derivedFrom":sQuery(id+"F10.wireOp",EDGE,"E338.MirrorCS")}),-1.0]])]});
            var Q64;
            Q64=makeQuery(id+"F10.imprint","IMPRINT",FACE,{"disambiguationData":[TD([[makeQuery(id+"F10.imprint","IMPRINT",EDGE,{"derivedFrom":sQuery(id+"F10.wireOp",EDGE,"E336.MirrorCS")}),1.0]])]});
            var Q65;
            Q65=makeQuery(id+"F10.imprint","IMPRINT",FACE,{"disambiguationData":[TD([[makeQuery(id+"F10.imprint","IMPRINT",EDGE,{"derivedFrom":sQuery(id+"F10.wireOp",EDGE,"E311.MirrorCS")}),1.0]])]});
            var Q66;
            {var subQ0=sQuery(id+"F10.wireOp",EDGE,"E276.MirrorCS");Q66=makeQuery(id+"F10.imprint","IMPRINT",FACE,{"disambiguationData":[TD([[makeQuery(id+"F10.imprint","IMPRINT",EDGE,{"derivedFrom":subQ0}),-1.0]])]});}
            var Q67;
            {var subQ0=sQuery(id+"F10.wireOp",EDGE,"E248.MirrorCS");Q67=makeQuery(id+"F10.imprint","IMPRINT",FACE,{"disambiguationData":[TD([[makeQuery(id+"F10.imprint","IMPRINT",EDGE,{"derivedFrom":subQ0}),1.0]])]});}
            var Q68;
            Q68=makeQuery(id+"F10.imprint","IMPRINT",FACE,{"disambiguationData":[TD([[makeQuery(id+"F10.imprint","IMPRINT",EDGE,{"derivedFrom":sQuery(id+"F10.wireOp",EDGE,"E252.MirrorCS")}),1.0]])]});
            var Q69;
            {var subQ0=sQuery(id+"F10.wireOp",EDGE,"E306.MirrorCS");Q69=makeQuery(id+"F10.imprint","IMPRINT",FACE,{"disambiguationData":[TD([[makeQuery(id+"F10.imprint","IMPRINT",EDGE,{"derivedFrom":subQ0}),1.0]])]});}
            var Q70;
            {var subQ0=sQuery(id+"F10.wireOp",EDGE,"E352.MirrorCS");Q70=makeQuery(id+"F10.imprint","IMPRINT",FACE,{"disambiguationData":[TD([[makeQuery(id+"F10.imprint","IMPRINT",EDGE,{"derivedFrom":subQ0}),-1.0]])]});}
            var Q71;
            {var subQ0=sQuery(id+"F10.wireOp",EDGE,"E319.MirrorCS");Q71=makeQuery(id+"F10.imprint","IMPRINT",FACE,{"disambiguationData":[TD([[makeQuery(id+"F10.imprint","IMPRINT",EDGE,{"derivedFrom":subQ0}),-1.0]])]});}
            var Q72;
            {var subQ0=sQuery(id+"F10.wireOp",EDGE,"E233.MirrorCS");Q72=makeQuery(id+"F10.imprint","IMPRINT",FACE,{"disambiguationData":[TD([[makeQuery(id+"F10.imprint","IMPRINT",EDGE,{"derivedFrom":subQ0}),1.0]])]});}
            var Q73;
            Q73=makeQuery(id+"F10.imprint","IMPRINT",FACE,{"disambiguationData":[TD([[makeQuery(id+"F10.imprint","IMPRINT",EDGE,{"derivedFrom":sQuery(id+"F10.wireOp",EDGE,"E270.MirrorCS")}),1.0]])]});
            var Q74;
            {var subQ0=sQuery(id+"F10.wireOp",EDGE,"E127.MirrorCS");Q74=makeQuery(id+"F10.imprint","IMPRINT",FACE,{"disambiguationData":[TD([[makeQuery(id+"F10.imprint","IMPRINT",EDGE,{"derivedFrom":subQ0}),1.0]])]});}
            var Q75;
            {var subQ0=sQuery(id+"F10.wireOp",EDGE,"E569.MirrorCS");Q75=makeQuery(id+"F10.imprint","IMPRINT",FACE,{"disambiguationData":[TD([[makeQuery(id+"F10.imprint","IMPRINT",EDGE,{"derivedFrom":subQ0}),-1.0]])]});}
            var Q76;
            {var subQ0=sQuery(id+"F10.wireOp",EDGE,"E632.MirrorCS");Q76=makeQuery(id+"F10.imprint","IMPRINT",FACE,{"disambiguationData":[TD([[makeQuery(id+"F10.imprint","IMPRINT",EDGE,{"derivedFrom":subQ0}),-1.0]])]});}
            var Q77;
            {var subQ0=sQuery(id+"F10.wireOp",EDGE,"E697.MirrorCS");Q77=makeQuery(id+"F10.imprint","IMPRINT",FACE,{"disambiguationData":[TD([[makeQuery(id+"F10.imprint","IMPRINT",EDGE,{"derivedFrom":subQ0}),-1.0]])]});}
            var Q78;
            {var subQ0=sQuery(id+"F10.wireOp",EDGE,"E533.MirrorCS");Q78=makeQuery(id+"F10.imprint","IMPRINT",FACE,{"disambiguationData":[TD([[makeQuery(id+"F10.imprint","IMPRINT",EDGE,{"derivedFrom":subQ0}),1.0]])]});}
            var Q79;
            {var subQ0=sQuery(id+"F10.wireOp",EDGE,"E463.MirrorCS");Q79=makeQuery(id+"F10.imprint","IMPRINT",FACE,{"disambiguationData":[TD([[makeQuery(id+"F10.imprint","IMPRINT",EDGE,{"derivedFrom":subQ0}),1.0]])]});}
            var Q80;
            Q80=makeQuery(id+"F10.imprint","IMPRINT",FACE,{"disambiguationData":[TD([[makeQuery(id+"F10.imprint","IMPRINT",EDGE,{"derivedFrom":sQuery(id+"F10.wireOp",EDGE,"E485.MirrorCS")}),-1.0]])]});
            var Q81;
            {var subQ0=sQuery(id+"F10.wireOp",EDGE,"E589.MirrorCS");Q81=makeQuery(id+"F10.imprint","IMPRINT",FACE,{"disambiguationData":[TD([[makeQuery(id+"F10.imprint","IMPRINT",EDGE,{"derivedFrom":subQ0}),-1.0]])]});}
            var Q82;
            Q82=makeQuery(id+"F10.imprint","IMPRINT",FACE,{"disambiguationData":[TD([[makeQuery(id+"F10.imprint","IMPRINT",EDGE,{"derivedFrom":sQuery(id+"F10.wireOp",EDGE,"E658.MirrorCS")}),1.0]])]});
            var Q83;
            {var subQ0=sQuery(id+"F10.wireOp",EDGE,"E606.MirrorCS");Q83=makeQuery(id+"F10.imprint","IMPRINT",FACE,{"disambiguationData":[TD([[makeQuery(id+"F10.imprint","IMPRINT",EDGE,{"derivedFrom":subQ0}),1.0]])]});}
            var Q84;
            {var subQ0=sQuery(id+"F10.wireOp",EDGE,"E494.MirrorCS");Q84=makeQuery(id+"F10.imprint","IMPRINT",FACE,{"disambiguationData":[TD([[makeQuery(id+"F10.imprint","IMPRINT",EDGE,{"derivedFrom":subQ0}),1.0]])]});}
            var Q85;
            Q85=makeQuery(id+"F10.imprint","IMPRINT",FACE,{"disambiguationData":[TD([[makeQuery(id+"F10.imprint","IMPRINT",EDGE,{"derivedFrom":sQuery(id+"F10.wireOp",EDGE,"E301.MirrorCS")}),1.0]])]});
            var Q86;
            Q86=makeQuery(id+"F10.imprint","IMPRINT",FACE,{"disambiguationData":[TD([[makeQuery(id+"F10.imprint","IMPRINT",EDGE,{"derivedFrom":sQuery(id+"F10.wireOp",EDGE,"E264.MirrorCS")}),-1.0]])]});
            var Q87;
            {var subQ0=sQuery(id+"F10.wireOp",EDGE,"E394.MirrorCS");Q87=makeQuery(id+"F10.imprint","IMPRINT",FACE,{"disambiguationData":[TD([[makeQuery(id+"F10.imprint","IMPRINT",EDGE,{"derivedFrom":subQ0}),-1.0]])]});}
            var Q88;
            {var subQ0=sQuery(id+"F10.wireOp",EDGE,"E364.MirrorCS");Q88=makeQuery(id+"F10.imprint","IMPRINT",FACE,{"disambiguationData":[TD([[makeQuery(id+"F10.imprint","IMPRINT",EDGE,{"derivedFrom":subQ0}),-1.0]])]});}
            var Q89;
            {var subQ0=sQuery(id+"F10.wireOp",EDGE,"E330.MirrorCS");Q89=makeQuery(id+"F10.imprint","IMPRINT",FACE,{"disambiguationData":[TD([[makeQuery(id+"F10.imprint","IMPRINT",EDGE,{"derivedFrom":subQ0}),1.0]])]});}
            var Q90;
            Q90=makeQuery(id+"F10.imprint","IMPRINT",FACE,{"disambiguationData":[TD([[makeQuery(id+"F10.imprint","IMPRINT",EDGE,{"derivedFrom":sQuery(id+"F10.wireOp",EDGE,"E275.MirrorCS")}),1.0]])]});
            var Q91;
            Q91=makeQuery(id+"F10.imprint","IMPRINT",FACE,{"disambiguationData":[TD([[makeQuery(id+"F10.imprint","IMPRINT",EDGE,{"derivedFrom":sQuery(id+"F10.wireOp",EDGE,"E237.MirrorCS")}),-1.0]])]});
            var Q92;
            {var subQ0=sQuery(id+"F10.wireOp",EDGE,"E262.MirrorCS");Q92=makeQuery(id+"F10.imprint","IMPRINT",FACE,{"disambiguationData":[TD([[makeQuery(id+"F10.imprint","IMPRINT",EDGE,{"derivedFrom":subQ0}),-1.0]])]});}
            var Q93;
            Q93=makeQuery(id+"F10.imprint","IMPRINT",FACE,{"disambiguationData":[TD([[makeQuery(id+"F10.imprint","IMPRINT",EDGE,{"derivedFrom":sQuery(id+"F10.wireOp",EDGE,"E348.MirrorCS")}),1.0]])]});
            var Q94;
            {var subQ0=sQuery(id+"F10.wireOp",EDGE,"E373.MirrorCS");Q94=makeQuery(id+"F10.imprint","IMPRINT",FACE,{"disambiguationData":[TD([[makeQuery(id+"F10.imprint","IMPRINT",EDGE,{"derivedFrom":subQ0}),1.0]])]});}
            var Q95;
            Q95=makeQuery(id+"F10.imprint","IMPRINT",FACE,{"disambiguationData":[TD([[makeQuery(id+"F10.imprint","IMPRINT",EDGE,{"derivedFrom":sQuery(id+"F10.wireOp",EDGE,"E462.MirrorCS")}),1.0]])]});
            var Q96;
            {var subQ0=sQuery(id+"F10.wireOp",EDGE,"E493.MirrorCS");Q96=makeQuery(id+"F10.imprint","IMPRINT",FACE,{"disambiguationData":[TD([[makeQuery(id+"F10.imprint","IMPRINT",EDGE,{"derivedFrom":subQ0}),1.0]])]});}
            var Q97;
            {var subQ0=sQuery(id+"F10.wireOp",EDGE,"E741.MirrorCS");Q97=makeQuery(id+"F10.imprint","IMPRINT",FACE,{"disambiguationData":[TD([[makeQuery(id+"F10.imprint","IMPRINT",EDGE,{"derivedFrom":subQ0}),1.0]])]});}
            var Q98;
            {var subQ0=sQuery(id+"F10.wireOp",EDGE,"E477.MirrorCS");Q98=makeQuery(id+"F10.imprint","IMPRINT",FACE,{"disambiguationData":[TD([[makeQuery(id+"F10.imprint","IMPRINT",EDGE,{"derivedFrom":subQ0}),-1.0]])]});}
            var Q99;
            {var subQ0=sQuery(id+"F10.wireOp",EDGE,"E605.MirrorCS");Q99=makeQuery(id+"F10.imprint","IMPRINT",FACE,{"disambiguationData":[TD([[makeQuery(id+"F10.imprint","IMPRINT",EDGE,{"derivedFrom":subQ0}),1.0]])]});}
            var Q100;
            {var subQ0=sQuery(id+"F10.wireOp",EDGE,"E618.MirrorCS");Q100=makeQuery(id+"F10.imprint","IMPRINT",FACE,{"disambiguationData":[TD([[makeQuery(id+"F10.imprint","IMPRINT",EDGE,{"derivedFrom":subQ0}),-1.0]])]});}
            var Q101;
            {var subQ0=sQuery(id+"F10.wireOp",EDGE,"E655.MirrorCS");Q101=makeQuery(id+"F10.imprint","IMPRINT",FACE,{"disambiguationData":[TD([[makeQuery(id+"F10.imprint","IMPRINT",EDGE,{"derivedFrom":subQ0}),-1.0]])]});}
            var Q102;
            {var subQ0=sQuery(id+"F10.wireOp",EDGE,"E675.MirrorCS");Q102=makeQuery(id+"F10.imprint","IMPRINT",FACE,{"disambiguationData":[TD([[makeQuery(id+"F10.imprint","IMPRINT",EDGE,{"derivedFrom":subQ0}),-1.0]])]});}
            var Q103;
            Q103=makeQuery(id+"F10.imprint","IMPRINT",FACE,{"disambiguationData":[TD([[makeQuery(id+"F10.imprint","IMPRINT",EDGE,{"derivedFrom":sQuery(id+"F10.wireOp",EDGE,"E686.MirrorCS")}),1.0]])]});
            var Q104;
            {var subQ0=sQuery(id+"F10.wireOp",EDGE,"E487.MirrorCS");Q104=makeQuery(id+"F10.imprint","IMPRINT",FACE,{"disambiguationData":[TD([[makeQuery(id+"F10.imprint","IMPRINT",EDGE,{"derivedFrom":subQ0}),1.0]])]});}
            var Q105;
            Q105=makeQuery(id+"F10.imprint","IMPRINT",FACE,{"disambiguationData":[TD([[makeQuery(id+"F10.imprint","IMPRINT",EDGE,{"derivedFrom":sQuery(id+"F10.wireOp",EDGE,"E441.MirrorCS")}),-1.0]])]});
            var Q106;
            {var subQ0=sQuery(id+"F10.wireOp",EDGE,"E546.MirrorCS");Q106=makeQuery(id+"F10.imprint","IMPRINT",FACE,{"disambiguationData":[TD([[makeQuery(id+"F10.imprint","IMPRINT",EDGE,{"derivedFrom":subQ0}),-1.0]])]});}
            var Q107;
            {var subQ0=sQuery(id+"F10.wireOp",EDGE,"E424.MirrorCS");Q107=makeQuery(id+"F10.imprint","IMPRINT",FACE,{"disambiguationData":[TD([[makeQuery(id+"F10.imprint","IMPRINT",EDGE,{"derivedFrom":subQ0}),-1.0]])]});}
            var Q108;
            Q108=makeQuery(id+"F10.imprint","IMPRINT",FACE,{"disambiguationData":[TD([[makeQuery(id+"F10.imprint","IMPRINT",EDGE,{"derivedFrom":sQuery(id+"F10.wireOp",EDGE,"E438.MirrorCS")}),-1.0]])]});
            var Q109;
            Q109=makeQuery(id+"F10.imprint","IMPRINT",FACE,{"disambiguationData":[TD([[makeQuery(id+"F10.imprint","IMPRINT",EDGE,{"derivedFrom":sQuery(id+"F10.wireOp",EDGE,"E709.MirrorCS")}),-1.0]])]});
            var Q110;
            {var subQ0=sQuery(id+"F10.wireOp",EDGE,"E525.MirrorCS");Q110=makeQuery(id+"F10.imprint","IMPRINT",FACE,{"disambiguationData":[TD([[makeQuery(id+"F10.imprint","IMPRINT",EDGE,{"derivedFrom":subQ0}),1.0]])]});}
            var Q111;
            {var subQ0=sQuery(id+"F10.wireOp",EDGE,"E541.MirrorCS");Q111=makeQuery(id+"F10.imprint","IMPRINT",FACE,{"disambiguationData":[TD([[makeQuery(id+"F10.imprint","IMPRINT",EDGE,{"derivedFrom":subQ0}),1.0]])]});}
            var Q112;
            {var subQ0=sQuery(id+"F10.wireOp",EDGE,"E428.MirrorCS");Q112=makeQuery(id+"F10.imprint","IMPRINT",FACE,{"disambiguationData":[TD([[makeQuery(id+"F10.imprint","IMPRINT",EDGE,{"derivedFrom":subQ0}),1.0]])]});}
            var Q113;
            {var subQ0=sQuery(id+"F10.wireOp",EDGE,"E510.MirrorCS");Q113=makeQuery(id+"F10.imprint","IMPRINT",FACE,{"disambiguationData":[TD([[makeQuery(id+"F10.imprint","IMPRINT",EDGE,{"derivedFrom":subQ0}),-1.0]])]});}
            var Q114;
            {var subQ0=sQuery(id+"F10.wireOp",EDGE,"E698.MirrorCS");Q114=makeQuery(id+"F10.imprint","IMPRINT",FACE,{"disambiguationData":[TD([[makeQuery(id+"F10.imprint","IMPRINT",EDGE,{"derivedFrom":subQ0}),1.0]])]});}
            var Q115;
            {var subQ0=sQuery(id+"F10.wireOp",EDGE,"E562.MirrorCS");Q115=makeQuery(id+"F10.imprint","IMPRINT",FACE,{"disambiguationData":[TD([[makeQuery(id+"F10.imprint","IMPRINT",EDGE,{"derivedFrom":subQ0}),1.0]])]});}
            var Q116;
            Q116=makeQuery(id+"F10.imprint","IMPRINT",FACE,{"disambiguationData":[TD([[makeQuery(id+"F10.imprint","IMPRINT",EDGE,{"derivedFrom":sQuery(id+"F10.wireOp",EDGE,"E505.MirrorCS")}),1.0]])]});
            var Q117;
            {var subQ0=sQuery(id+"F10.wireOp",EDGE,"E461.MirrorCS");Q117=makeQuery(id+"F10.imprint","IMPRINT",FACE,{"disambiguationData":[TD([[makeQuery(id+"F10.imprint","IMPRINT",EDGE,{"derivedFrom":subQ0}),-1.0]])]});}
            var Q118;
            {var subQ0=sQuery(id+"F10.wireOp",EDGE,"E542.MirrorCS");Q118=makeQuery(id+"F10.imprint","IMPRINT",FACE,{"disambiguationData":[TD([[makeQuery(id+"F10.imprint","IMPRINT",EDGE,{"derivedFrom":subQ0}),-1.0]])]});}
            var Q119;
            {var subQ0=sQuery(id+"F10.wireOp",EDGE,"E729.MirrorCS");Q119=makeQuery(id+"F10.imprint","IMPRINT",FACE,{"disambiguationData":[TD([[makeQuery(id+"F10.imprint","IMPRINT",EDGE,{"derivedFrom":subQ0}),-1.0]])]});}
            var Q120;
            {var subQ0=sQuery(id+"F10.wireOp",EDGE,"E532.MirrorCS");Q120=makeQuery(id+"F10.imprint","IMPRINT",FACE,{"disambiguationData":[TD([[makeQuery(id+"F10.imprint","IMPRINT",EDGE,{"derivedFrom":subQ0}),1.0]])]});}
            var Q121;
            {var subQ0=sQuery(id+"F10.wireOp",EDGE,"E449.MirrorCS");Q121=makeQuery(id+"F10.imprint","IMPRINT",FACE,{"disambiguationData":[TD([[makeQuery(id+"F10.imprint","IMPRINT",EDGE,{"derivedFrom":subQ0}),1.0]])]});}
            var Q122;
            {var subQ0=sQuery(id+"F10.wireOp",EDGE,"E501.MirrorCS");Q122=makeQuery(id+"F10.imprint","IMPRINT",FACE,{"disambiguationData":[TD([[makeQuery(id+"F10.imprint","IMPRINT",EDGE,{"derivedFrom":subQ0}),-1.0]])]});}
            var Q123;
            {var subQ0=sQuery(id+"F10.wireOp",EDGE,"E586.MirrorCS");Q123=makeQuery(id+"F10.imprint","IMPRINT",FACE,{"disambiguationData":[TD([[makeQuery(id+"F10.imprint","IMPRINT",EDGE,{"derivedFrom":subQ0}),-1.0]])]});}
            var Q124;
            {var subQ0=sQuery(id+"F10.wireOp",EDGE,"E737.MirrorCS");Q124=makeQuery(id+"F10.imprint","IMPRINT",FACE,{"disambiguationData":[TD([[makeQuery(id+"F10.imprint","IMPRINT",EDGE,{"derivedFrom":subQ0}),1.0]])]});}
            var Q125;
            {var subQ0=sQuery(id+"F10.wireOp",EDGE,"E654.MirrorCS");Q125=makeQuery(id+"F10.imprint","IMPRINT",FACE,{"disambiguationData":[TD([[makeQuery(id+"F10.imprint","IMPRINT",EDGE,{"derivedFrom":subQ0}),1.0]])]});}
            var Q126;
            {var subQ0=sQuery(id+"F10.wireOp",EDGE,"E583.MirrorCS");Q126=makeQuery(id+"F10.imprint","IMPRINT",FACE,{"disambiguationData":[TD([[makeQuery(id+"F10.imprint","IMPRINT",EDGE,{"derivedFrom":subQ0}),1.0]])]});}
            var Q127;
            Q127=makeQuery(id+"F10.imprint","IMPRINT",FACE,{"disambiguationData":[TD([[makeQuery(id+"F10.imprint","IMPRINT",EDGE,{"derivedFrom":sQuery(id+"F10.wireOp",EDGE,"E619.MirrorCS")}),1.0]])]});
            var Q128;
            {var subQ0=sQuery(id+"F10.wireOp",EDGE,"E742.MirrorCS");Q128=makeQuery(id+"F10.imprint","IMPRINT",FACE,{"disambiguationData":[TD([[makeQuery(id+"F10.imprint","IMPRINT",EDGE,{"derivedFrom":subQ0}),1.0]])]});}
            var Q129;
            {var subQ0=sQuery(id+"F10.wireOp",EDGE,"E558.MirrorCS");Q129=makeQuery(id+"F10.imprint","IMPRINT",FACE,{"disambiguationData":[TD([[makeQuery(id+"F10.imprint","IMPRINT",EDGE,{"derivedFrom":subQ0}),-1.0]])]});}
            var Q130;
            {var subQ0=sQuery(id+"F10.wireOp",EDGE,"E436.MirrorCS");Q130=makeQuery(id+"F10.imprint","IMPRINT",FACE,{"disambiguationData":[TD([[makeQuery(id+"F10.imprint","IMPRINT",EDGE,{"derivedFrom":subQ0}),1.0]])]});}
            var Q131;
            {var subQ0=sQuery(id+"F10.wireOp",EDGE,"E479.MirrorCS");Q131=makeQuery(id+"F10.imprint","IMPRINT",FACE,{"disambiguationData":[TD([[makeQuery(id+"F10.imprint","IMPRINT",EDGE,{"derivedFrom":subQ0}),1.0]])]});}
            var Q132;
            {var subQ0=sQuery(id+"F10.wireOp",EDGE,"E521.MirrorCS");Q132=makeQuery(id+"F10.imprint","IMPRINT",FACE,{"disambiguationData":[TD([[makeQuery(id+"F10.imprint","IMPRINT",EDGE,{"derivedFrom":subQ0}),1.0]])]});}
            var Q133;
            {var subQ0=sQuery(id+"F10.wireOp",EDGE,"E577.MirrorCS");Q133=makeQuery(id+"F10.imprint","IMPRINT",FACE,{"disambiguationData":[TD([[makeQuery(id+"F10.imprint","IMPRINT",EDGE,{"derivedFrom":subQ0}),-1.0]])]});}
            var Q134;
            Q134=makeQuery(id+"F10.imprint","IMPRINT",FACE,{"disambiguationData":[TD([[makeQuery(id+"F10.imprint","IMPRINT",EDGE,{"derivedFrom":sQuery(id+"F10.wireOp",EDGE,"E651.MirrorCS")}),-1.0]])]});
            var Q135;
            {var subQ0=sQuery(id+"F10.wireOp",EDGE,"E568.MirrorCS");Q135=makeQuery(id+"F10.imprint","IMPRINT",FACE,{"disambiguationData":[TD([[makeQuery(id+"F10.imprint","IMPRINT",EDGE,{"derivedFrom":subQ0}),-1.0]])]});}
            var Q136;
            {var subQ0=sQuery(id+"F10.wireOp",EDGE,"E425.MirrorCS");Q136=makeQuery(id+"F10.imprint","IMPRINT",FACE,{"disambiguationData":[TD([[makeQuery(id+"F10.imprint","IMPRINT",EDGE,{"derivedFrom":subQ0}),-1.0]])]});}
            var Q137;
            Q137=makeQuery(id+"F10.imprint","IMPRINT",FACE,{"disambiguationData":[TD([[makeQuery(id+"F10.imprint","IMPRINT",EDGE,{"derivedFrom":sQuery(id+"F10.wireOp",EDGE,"E534.MirrorCS")}),1.0]])]});
            var Q138;
            {var subQ0=sQuery(id+"F10.wireOp",EDGE,"E712.MirrorCS");Q138=makeQuery(id+"F10.imprint","IMPRINT",FACE,{"disambiguationData":[TD([[makeQuery(id+"F10.imprint","IMPRINT",EDGE,{"derivedFrom":subQ0}),1.0]])]});}
            var Q139;
            {var subQ0=sQuery(id+"F10.wireOp",EDGE,"E413.MirrorCS");Q139=makeQuery(id+"F10.imprint","IMPRINT",FACE,{"disambiguationData":[TD([[makeQuery(id+"F10.imprint","IMPRINT",EDGE,{"derivedFrom":subQ0}),-1.0]])]});}
            var Q140;
            {var subQ0=sQuery(id+"F10.wireOp",EDGE,"E412.MirrorCS");Q140=makeQuery(id+"F10.imprint","IMPRINT",FACE,{"disambiguationData":[TD([[makeQuery(id+"F10.imprint","IMPRINT",EDGE,{"derivedFrom":subQ0}),-1.0]])]});}
            var Q141;
            {var subQ0=sQuery(id+"F10.wireOp",EDGE,"E607.MirrorCS");Q141=makeQuery(id+"F10.imprint","IMPRINT",FACE,{"disambiguationData":[TD([[makeQuery(id+"F10.imprint","IMPRINT",EDGE,{"derivedFrom":subQ0}),1.0]])]});}
            var Q142;
            {var subQ0=sQuery(id+"F10.wireOp",EDGE,"E653.MirrorCS");Q142=makeQuery(id+"F10.imprint","IMPRINT",FACE,{"disambiguationData":[TD([[makeQuery(id+"F10.imprint","IMPRINT",EDGE,{"derivedFrom":subQ0}),1.0]])]});}
            var Q143;
            {var subQ0=sQuery(id+"F10.wireOp",EDGE,"E718.MirrorCS");Q143=makeQuery(id+"F10.imprint","IMPRINT",FACE,{"disambiguationData":[TD([[makeQuery(id+"F10.imprint","IMPRINT",EDGE,{"derivedFrom":subQ0}),-1.0]])]});}
            var Q144;
            {var subQ0=sQuery(id+"F10.wireOp",EDGE,"E637.MirrorCS");Q144=makeQuery(id+"F10.imprint","IMPRINT",FACE,{"disambiguationData":[TD([[makeQuery(id+"F10.imprint","IMPRINT",EDGE,{"derivedFrom":subQ0}),-1.0]])]});}
            var Q145;
            {var subQ0=sQuery(id+"F10.wireOp",EDGE,"E617.MirrorCS");Q145=makeQuery(id+"F10.imprint","IMPRINT",FACE,{"disambiguationData":[TD([[makeQuery(id+"F10.imprint","IMPRINT",EDGE,{"derivedFrom":subQ0}),-1.0]])]});}
            var Q146;
            Q146=makeQuery(id+"F10.imprint","IMPRINT",FACE,{"disambiguationData":[TD([[makeQuery(id+"F10.imprint","IMPRINT",EDGE,{"derivedFrom":sQuery(id+"F10.wireOp",EDGE,"E538.MirrorCS")}),1.0]])]});
            var Q147;
            {var subQ0=sQuery(id+"F10.wireOp",EDGE,"E601.MirrorCS");Q147=makeQuery(id+"F10.imprint","IMPRINT",FACE,{"disambiguationData":[TD([[makeQuery(id+"F10.imprint","IMPRINT",EDGE,{"derivedFrom":subQ0}),1.0]])]});}
            var Q148;
            Q148=makeQuery(id+"F10.imprint","IMPRINT",FACE,{"disambiguationData":[TD([[makeQuery(id+"F10.imprint","IMPRINT",EDGE,{"derivedFrom":sQuery(id+"F10.wireOp",EDGE,"E746.MirrorCS")}),1.0]])]});
            var Q149;
            {var subQ0=sQuery(id+"F10.wireOp",EDGE,"E630.MirrorCS");Q149=makeQuery(id+"F10.imprint","IMPRINT",FACE,{"disambiguationData":[TD([[makeQuery(id+"F10.imprint","IMPRINT",EDGE,{"derivedFrom":subQ0}),-1.0]])]});}
            var Q150;
            {var subQ0=sQuery(id+"F10.wireOp",EDGE,"E585.MirrorCS");Q150=makeQuery(id+"F10.imprint","IMPRINT",FACE,{"disambiguationData":[TD([[makeQuery(id+"F10.imprint","IMPRINT",EDGE,{"derivedFrom":subQ0}),-1.0]])]});}
            var Q151;
            {var subQ0=sQuery(id+"F10.wireOp",EDGE,"E472.MirrorCS");Q151=makeQuery(id+"F10.imprint","IMPRINT",FACE,{"disambiguationData":[TD([[makeQuery(id+"F10.imprint","IMPRINT",EDGE,{"derivedFrom":subQ0}),1.0]])]});}
            var Q152;
            {var subQ0=sQuery(id+"F10.wireOp",EDGE,"E509.MirrorCS");Q152=makeQuery(id+"F10.imprint","IMPRINT",FACE,{"disambiguationData":[TD([[makeQuery(id+"F10.imprint","IMPRINT",EDGE,{"derivedFrom":subQ0}),1.0]])]});}
            var Q153;
            {var subQ0=sQuery(id+"F10.wireOp",EDGE,"E705.MirrorCS");Q153=makeQuery(id+"F10.imprint","IMPRINT",FACE,{"disambiguationData":[TD([[makeQuery(id+"F10.imprint","IMPRINT",EDGE,{"derivedFrom":subQ0}),-1.0]])]});}
            var Q154;
            {var subQ0=sQuery(id+"F10.wireOp",EDGE,"E480.MirrorCS");Q154=makeQuery(id+"F10.imprint","IMPRINT",FACE,{"disambiguationData":[TD([[makeQuery(id+"F10.imprint","IMPRINT",EDGE,{"derivedFrom":subQ0}),-1.0]])]});}
            var Q155;
            Q155=makeQuery(id+"F10.imprint","IMPRINT",FACE,{"disambiguationData":[TD([[makeQuery(id+"F10.imprint","IMPRINT",EDGE,{"derivedFrom":sQuery(id+"F10.wireOp",EDGE,"E442.MirrorCS")}),-1.0]])]});
            var Q156;
            {var subQ0=sQuery(id+"F10.wireOp",EDGE,"E514.MirrorCS");Q156=makeQuery(id+"F10.imprint","IMPRINT",FACE,{"disambiguationData":[TD([[makeQuery(id+"F10.imprint","IMPRINT",EDGE,{"derivedFrom":subQ0}),1.0]])]});}
            var Q157;
            {var subQ0=sQuery(id+"F10.wireOp",EDGE,"E595.MirrorCS");Q157=makeQuery(id+"F10.imprint","IMPRINT",FACE,{"disambiguationData":[TD([[makeQuery(id+"F10.imprint","IMPRINT",EDGE,{"derivedFrom":subQ0}),1.0]])]});}
            var Q158;
            Q158=makeQuery(id+"F10.imprint","IMPRINT",FACE,{"disambiguationData":[TD([[makeQuery(id+"F10.imprint","IMPRINT",EDGE,{"derivedFrom":sQuery(id+"F10.wireOp",EDGE,"E761.MirrorCS")}),1.0]])]});
            var Q159;
            {var subQ0=sQuery(id+"F10.wireOp",EDGE,"E473.MirrorCS");Q159=makeQuery(id+"F10.imprint","IMPRINT",FACE,{"disambiguationData":[TD([[makeQuery(id+"F10.imprint","IMPRINT",EDGE,{"derivedFrom":subQ0}),-1.0]])]});}
            var Q160;
            {var subQ0=sQuery(id+"F10.wireOp",EDGE,"E439.MirrorCS");Q160=makeQuery(id+"F10.imprint","IMPRINT",FACE,{"disambiguationData":[TD([[makeQuery(id+"F10.imprint","IMPRINT",EDGE,{"derivedFrom":subQ0}),-1.0]])]});}
            var Q161;
            {var subQ0=sQuery(id+"F10.wireOp",EDGE,"E613.MirrorCS");Q161=makeQuery(id+"F10.imprint","IMPRINT",FACE,{"disambiguationData":[TD([[makeQuery(id+"F10.imprint","IMPRINT",EDGE,{"derivedFrom":subQ0}),1.0]])]});}
            var Q162;
            {var subQ0=sQuery(id+"F10.wireOp",EDGE,"E621.MirrorCS");Q162=makeQuery(id+"F10.imprint","IMPRINT",FACE,{"disambiguationData":[TD([[makeQuery(id+"F10.imprint","IMPRINT",EDGE,{"derivedFrom":subQ0}),1.0]])]});}
            var Q163;
            {var subQ0=sQuery(id+"F10.wireOp",EDGE,"E713.MirrorCS");Q163=makeQuery(id+"F10.imprint","IMPRINT",FACE,{"disambiguationData":[TD([[makeQuery(id+"F10.imprint","IMPRINT",EDGE,{"derivedFrom":subQ0}),-1.0]])]});}
            var Q164;
            {var subQ0=sQuery(id+"F10.wireOp",EDGE,"E588.MirrorCS");Q164=makeQuery(id+"F10.imprint","IMPRINT",FACE,{"disambiguationData":[TD([[makeQuery(id+"F10.imprint","IMPRINT",EDGE,{"derivedFrom":subQ0}),-1.0]])]});}
            var Q165;
            {var subQ0=sQuery(id+"F10.wireOp",EDGE,"E592.MirrorCS");Q165=makeQuery(id+"F10.imprint","IMPRINT",FACE,{"disambiguationData":[TD([[makeQuery(id+"F10.imprint","IMPRINT",EDGE,{"derivedFrom":subQ0}),-1.0]])]});}
            var Q166;
            {var subQ0=sQuery(id+"F10.wireOp",EDGE,"E590.MirrorCS");Q166=makeQuery(id+"F10.imprint","IMPRINT",FACE,{"disambiguationData":[TD([[makeQuery(id+"F10.imprint","IMPRINT",EDGE,{"derivedFrom":subQ0}),1.0]])]});}
            var Q167;
            {var subQ0=sQuery(id+"F10.wireOp",EDGE,"E635.MirrorCS");Q167=makeQuery(id+"F10.imprint","IMPRINT",FACE,{"disambiguationData":[TD([[makeQuery(id+"F10.imprint","IMPRINT",EDGE,{"derivedFrom":subQ0}),1.0]])]});}
            var Q168;
            {var subQ0=sQuery(id+"F10.wireOp",EDGE,"E571.MirrorCS");Q168=makeQuery(id+"F10.imprint","IMPRINT",FACE,{"disambiguationData":[TD([[makeQuery(id+"F10.imprint","IMPRINT",EDGE,{"derivedFrom":subQ0}),-1.0]])]});}
            extrude(context, id + "F11", {"entities" : qUnion([Q0, Q1, Q2, Q3, Q4, Q5, Q6, Q7, Q8, Q9, Q10, Q11, Q12, Q13, Q14, Q15, Q16, Q17, Q18, Q19, Q20, Q21, Q22, Q23, Q24, Q25, Q26, Q27, Q28, Q29, Q30, Q31, Q32, Q33, Q34, Q35, Q36, Q37, Q38, Q39, Q40, Q41, Q42, Q43, Q44, Q45, Q46, Q47, Q48, Q49, Q50, Q51, Q52, Q53, Q54, Q55, Q56, Q57, Q58, Q59, Q60, Q61, Q62, Q63, Q64, Q65, Q66, Q67, Q68, Q69, Q70, Q71, Q72, Q73, Q74, Q75, Q76, Q77, Q78, Q79, Q80, Q81, Q82, Q83, Q84, Q85, Q86, Q87, Q88, Q89, Q90, Q91, Q92, Q93, Q94, Q95, Q96, Q97, Q98, Q99, Q100, Q101, Q102, Q103, Q104, Q105, Q106, Q107, Q108, Q109, Q110, Q111, Q112, Q113, Q114, Q115, Q116, Q117, Q118, Q119, Q120, Q121, Q122, Q123, Q124, Q125, Q126, Q127, Q128, Q129, Q130, Q131, Q132, Q133, Q134, Q135, Q136, Q137, Q138, Q139, Q140, Q141, Q142, Q143, Q144, Q145, Q146, Q147, Q148, Q149, Q150, Q151, Q152, Q153, Q154, Q155, Q156, Q157, Q158, Q159, Q160, Q161, Q162, Q163, Q164, Q165, Q166, Q167, Q168]), "oppositeDirection" : true, "depth" : 6.1 * mm});
        }
        {
            var Q0;
            {var subQ0=sQuery(id+"F0.wireOp",EDGE,"E21.MirrorCS");var subQ1=sQuery(id+"F0.wireOp",EDGE,"E20.MirrorCS");var subQ2=sQuery(id+"F0.wireOp",EDGE,"E19.MirrorCS");var subQ3=sQuery(id+"F0.wireOp",EDGE,"E18.MirrorCS");var subQ4=sQuery(id+"F0.wireOp",EDGE,"E17.MirrorCS");var subQ5=sQuery(id+"F0.wireOp",EDGE,"E16.MirrorCS");var subQ6=sQuery(id+"F0.wireOp",EDGE,"E14.filletArc");var subQ7=sQuery(id+"F0.wireOp",EDGE,"E13.filletArc");var subQ8=sQuery(id+"F0.wireOp",EDGE,"E12.filletArc");var subQ9=sQuery(id+"F0.wireOp",EDGE,"E11.filletArc");var subQ10=sQuery(id+"F0.wireOp",EDGE,"E10");var subQ11=sQuery(id+"F0.wireOp",EDGE,"E9");var subQ12=sQuery(id+"F0.wireOp",EDGE,"E7.filletArc");var subQ13=sQuery(id+"F0.wireOp",EDGE,"E6.filletArc");var subQ14=sQuery(id+"F0.wireOp",EDGE,"E3.MirrorCS");var subQ15=sQuery(id+"F0.wireOp",EDGE,"E2.MirrorCS");var subQ16=sQuery(id+"F0.wireOp",EDGE,"E1");var subQ17=sQuery(id+"F0.wireOp",EDGE,"E0");Q0=makeQuery(id+"F3.opShell","OFFSET_FACE",FACE,{"disambiguationData":[OSD([subQ17,subQ16,subQ15,subQ14,subQ13,subQ12,subQ11,subQ10,subQ9,subQ8,subQ7,subQ6,subQ5,subQ4,subQ3,subQ2,subQ1,subQ0]),TDD([makeQuery(id+"F1.opExtrude","CAP_FACE",FACE,{"disambiguationData":[OSD([subQ17,subQ16,subQ15,subQ14,subQ13,subQ12,subQ11,subQ10,subQ9,subQ8,subQ7,subQ6,subQ5,subQ4,subQ3,subQ2,subQ1,subQ0])],"isStart":true})])]});}
            var sketch = newSketch(context, id + "F12", { "sketchPlane" : qUnion([Q0])});
            skLineSegment(sketch, "E782", {"start": v(-18.6, 23) * mm, "end": v(-18.8, 23.67) * mm});
            skLineSegment(sketch, "E783", {"start": v(-91.16, -0.02) * mm, "end": v(-91.37, 0.65) * mm});
            skPoint(sketch, "E784.endSnap0", {"position": v(-18.66, 23.19) * mm});
            skLineSegment(sketch, "E785", {"start": v(-91.37, 0.65) * mm, "end": v(-18.8, 23.67) * mm});
            skLineSegment(sketch, "E786.MirrorCS", {"start": v(-91.16, -0.02) * mm, "end": v(-18.6, 23) * mm});
            skPoint(sketch, "E787.orphan", {"position": v(-19.05, 24.44) * mm});
            skPoint(sketch, "E788.orphan", {"position": v(-18.26, 21.93) * mm});
            skArc(sketch, "E789", {"start": v(-91.37, 0.65) * mm, "mid": v(-91.6, 0.2) * mm, "end": v(-91.16, -0.02) * mm});
            skArc(sketch, "E790", {"start": v(-18.6, 23) * mm, "mid": v(-18.36, 23.44) * mm, "end": v(-18.8, 23.67) * mm});
            skArc(sketch, "E791.MirrorCS", {"start": v(18.6, 23) * mm, "mid": v(18.36, 23.44) * mm, "end": v(18.8, 23.67) * mm});
            skLineSegment(sketch, "E792.MirrorCS", {"start": v(18.6, 23) * mm, "end": v(18.8, 23.67) * mm});
            skLineSegment(sketch, "E793.MirrorCS", {"start": v(91.37, 0.65) * mm, "end": v(18.8, 23.67) * mm});
            skLineSegment(sketch, "E794.MirrorCS", {"start": v(91.16, -0.02) * mm, "end": v(18.6, 23) * mm});
            skArc(sketch, "E795.MirrorCS", {"start": v(91.37, 0.65) * mm, "mid": v(91.6, 0.2) * mm, "end": v(91.16, -0.02) * mm});
            skLineSegment(sketch, "E796.MirrorCS", {"start": v(91.16, -0.02) * mm, "end": v(91.37, 0.65) * mm});
            skSolve(sketch);
        }
        {
            var Q0;
            Q0 = qSketchRegion(id + "F12", true);
            extrude(context, id + "F13", {"entities" : qUnion([Q0]), "operationType" : NewBodyOperationType.REMOVE, "oppositeDirection" : true, "depth" : 25.4 * mm});
        }
        {
            var Q0;
            {var subQ0=sQuery(id+"F0.wireOp",EDGE,"E21.MirrorCS");var subQ1=sQuery(id+"F0.wireOp",EDGE,"E20.MirrorCS");var subQ2=sQuery(id+"F0.wireOp",EDGE,"E19.MirrorCS");var subQ3=sQuery(id+"F0.wireOp",EDGE,"E18.MirrorCS");var subQ4=sQuery(id+"F0.wireOp",EDGE,"E17.MirrorCS");var subQ5=sQuery(id+"F0.wireOp",EDGE,"E16.MirrorCS");var subQ6=sQuery(id+"F0.wireOp",EDGE,"E14.filletArc");var subQ7=sQuery(id+"F0.wireOp",EDGE,"E13.filletArc");var subQ8=sQuery(id+"F0.wireOp",EDGE,"E12.filletArc");var subQ9=sQuery(id+"F0.wireOp",EDGE,"E11.filletArc");var subQ10=sQuery(id+"F0.wireOp",EDGE,"E10");var subQ11=sQuery(id+"F0.wireOp",EDGE,"E9");var subQ12=sQuery(id+"F0.wireOp",EDGE,"E7.filletArc");var subQ13=sQuery(id+"F0.wireOp",EDGE,"E6.filletArc");var subQ14=sQuery(id+"F0.wireOp",EDGE,"E3.MirrorCS");var subQ15=sQuery(id+"F0.wireOp",EDGE,"E2.MirrorCS");var subQ16=sQuery(id+"F0.wireOp",EDGE,"E1");var subQ17=sQuery(id+"F0.wireOp",EDGE,"E0");Q0=makeQuery(id+"F3.opShell","OFFSET_FACE",FACE,{"disambiguationData":[OSD([subQ17,subQ16,subQ15,subQ14,subQ13,subQ12,subQ11,subQ10,subQ9,subQ8,subQ7,subQ6,subQ5,subQ4,subQ3,subQ2,subQ1,subQ0]),TDD([makeQuery(id+"F1.opExtrude","CAP_FACE",FACE,{"disambiguationData":[OSD([subQ17,subQ16,subQ15,subQ14,subQ13,subQ12,subQ11,subQ10,subQ9,subQ8,subQ7,subQ6,subQ5,subQ4,subQ3,subQ2,subQ1,subQ0])],"isStart":true})])]});}
            var sketch = newSketch(context, id + "F14", { "sketchPlane" : qUnion([Q0])});
            skCircle(sketch, "E797", {"center": v(-90.93, 0.42) * mm, "radius": 0.31 * mm});
            skSolve(sketch);
        }
        {
            var Q0;
            Q0 = qSketchRegion(id + "F14", true);
            extrude(context, id + "F15", {"entities" : qUnion([Q0]), "depth" : 0.25 * mm});
        }
        {
            var Q0;
            Q0=makeQuery(id+"F15.opExtrude","CAP_FACE",FACE,{"disambiguationData":[OSD([sQuery(id+"F14.wireOp",EDGE,"E797")])],"isStart":true});
            var sketch = newSketch(context, id + "F16", { "sketchPlane" : qUnion([Q0])});
            skCircle(sketch, "E798", {"center": v(90.93, 0.42) * mm, "radius": 0.32 * mm});
            skSolve(sketch);
        }
        {
            var Q0;
            Q0 = qSketchRegion(id + "F16", true);
            extrude(context, id + "F17", {"entities" : qUnion([Q0]), "operationType" : NewBodyOperationType.ADD, "depth" : 2.8 * mm});
        }
        {
            var Q0;
            Q0=makeQuery(id+"F17.opExtrude","CAP_FACE",FACE,{"disambiguationData":[OSD([sQuery(id+"F16.wireOp",EDGE,"E798")])],"isStart":false});
            var sketch = newSketch(context, id + "F18", { "sketchPlane" : qUnion([Q0])});
            skCircle(sketch, "E799", {"center": v(90.93, 0.42) * mm, "radius": 0.52 * mm});
            skSolve(sketch);
        }
        {
            var Q0;
            Q0 = qSketchRegion(id + "F18", true);
            extrude(context, id + "F19", {"entities" : qUnion([Q0]), "operationType" : NewBodyOperationType.ADD, "depth" : 0.25 * mm});
        }
        {
            var Q0;
            Q0=makeQuery(id+"F19.opExtrude","CAP_EDGE",EDGE,{"disambiguationData":[OSD([sQuery(id+"F18.wireOp",EDGE,"E799")])],"isStart":false});
            var Q1;
            Q1=makeQuery(id+"F19.opExtrude","CAP_EDGE",EDGE,{"disambiguationData":[OSD([sQuery(id+"F18.wireOp",EDGE,"E799")])],"isStart":true});
            fillet(context, id + "F20", {"entities" : qUnion([Q0, Q1]), "radius" : 0.13 * mm, "tangentPropagation" : true, "allowEdgeOverflow" : false});
        }
        {
            var Q0;
            Q0=makeQuery(id+"F15.opExtrude","CAP_FACE",FACE,{"disambiguationData":[OSD([sQuery(id+"F14.wireOp",EDGE,"E797")])],"isStart":false});
            var sketch = newSketch(context, id + "F21", { "sketchPlane" : qUnion([Q0])});
            skCircle(sketch, "E800", {"center": v(-90.93, 0.42) * mm, "radius": 1.02 * mm});
            skLineSegment(sketch, "E801", {"start": v(-90.6, -0.66) * mm, "end": v(-90.55, -0.64) * mm});
            skLineSegment(sketch, "E802", {"start": v(-90.6, -0.66) * mm, "end": v(-90.67, -0.68) * mm});
            skLineSegment(sketch, "E803", {"start": v(-90.67, -0.68) * mm, "end": v(-90.79, -0.58) * mm});
            skLineSegment(sketch, "E804", {"start": v(-90.55, -0.64) * mm, "end": v(-90.5, -0.5) * mm});
            skLineSegment(sketch, "E805", {"start": v(-90.79, -0.58) * mm, "end": v(-90.5, -0.5) * mm});
            skLineSegment(sketch, "E806", {"start": v(-90.5, -0.5) * mm, "end": v(-90.36, -0.42) * mm});
            skLineSegment(sketch, "E807", {"start": v(-90.36, -0.42) * mm, "end": v(-90.22, -0.46) * mm});
            skLineSegment(sketch, "E808", {"start": v(-90.22, -0.46) * mm, "end": v(-90.12, -0.38) * mm});
            skLineSegment(sketch, "E809", {"start": v(-90.12, -0.38) * mm, "end": v(-90.15, -0.23) * mm});
            skLineSegment(sketch, "E810", {"start": v(-90.36, -0.42) * mm, "end": v(-90.15, -0.23) * mm});
            skLineSegment(sketch, "E811", {"start": v(-90.15, -0.23) * mm, "end": v(-90.06, -0.1) * mm});
            skLineSegment(sketch, "E812", {"start": v(-90.06, -0.1) * mm, "end": v(-89.91, -0.1) * mm});
            skLineSegment(sketch, "E813", {"start": v(-89.91, -0.1) * mm, "end": v(-89.86, 0.04) * mm});
            skLineSegment(sketch, "E814", {"start": v(-89.86, 0.04) * mm, "end": v(-89.95, 0.16) * mm});
            skSolve(sketch);
        }
        {
            var Q0;
            Q0 = qSketchRegion(id + "F21", true);
            extrude(context, id + "F22", {"entities" : qUnion([Q0]), "depth" : 6.1 * mm});
        }
    });
